FCSTD DOCUMENT  (FreeCAD 0.18R16146 (Git))
Label: Marlon
License: All rights reserved
LicenseURL: http://en.wikipedia.org/wiki/All_rights_reserved
objects: Part::Feature×142, Part::Cylinder×83, Part::FeaturePython×81, Sketcher::SketchObject×72, Part::Compound×70, App::Part×62, Part::Cut×46, PartDesign::Pocket×41, Part::Box×41, PartDesign::FeatureBase×30, PartDesign::Pad×28, Part::MultiFuse×23, App::DocumentObjectGroup×23, Part::Chamfer×6, Part::Fillet×5, PartDesign::PolarPattern×3, Part::Helix×3, Part::Sweep×3, PartDesign::LinearPattern×2, PartDesign::Chamfer×2, +4 more types
note: 751 computed .brp shape members not serialized (recipe doc carries the construction recipe); baked Part::Feature solids carry a one-line shape summary decoded from their .brp

FEATURE [Part::Compound] Compound038  label="3x4-male-pin-header"
  Placement = pos=(-9.21766,-28.5253,0) rot=(0,0,1;0rad)
FEATURE [Part::Compound] Compound040  label="1x8-female-pin-header"
  Placement = pos=(0.513,5.274,0) rot=(0,0,1;0rad)
FEATURE [Part::Compound] Compound021  label="2x18-male-pin-header"
  Placement = pos=(42.6284,-15.145,-2) rot=(0.707107,0.707107,0;3.14159rad)
FEATURE [Part::Compound] Compound045  label="1x8-female-pin-header005"
  Placement = pos=(20.89,-4.94,0) rot=(0,0,1;0rad)
FEATURE [Part::Cylinder] Cylinder003
  Angle = 360
  AttacherType = Attacher::AttachEngine3D
  Height = 10
  Placement = pos=(-27.818,28.246,-6) rot=(0,0,1;0rad)
  Radius = 0.45
FEATURE [Part::FeaturePython] Array003  label="1x8-male-pins-header-1"  # Draft array (typed FeaturePython)
  Angle = 360
  ArrayType = 0
  Axis = (0,0,1)
  Base = -> Cylinder003
  Center = (0,0,0)
  IntervalX = (2.55,0,0)
  IntervalY = (0,1,0)
  IntervalZ = (0,0,1)
  NumberPolar = 1
  NumberX = 8
  NumberY = 1
  NumberZ = 1
FEATURE [Part::Compound] Compound030  label="2x3-male-pin-header001"
  Placement = pos=(13.2632,-10.0364,0) rot=(0,0,1;1.5708rad)
FEATURE [Part::Compound] Compound042  label="1x8-female-pin-header002"
  Placement = pos=(20.89,-17.7,0) rot=(0,0,1;0rad)
FEATURE [Part::Cylinder] Cylinder012005  label="Cylinder017"
  Angle = 360
  AttacherType = Attacher::AttachEngine3D
  Height = 10
  Placement = pos=(-12.5549,-24.4231,-10) rot=(0,0,1;0rad)
  Radius = 0.75
FEATURE [Part::Compound] Compound037  label="2x5-male-pin-header"
  Placement = pos=(22.2091,-27.7375,0) rot=(0,0,1;0rad)
FEATURE [Part::Compound] Compound010  label="capsmd6_3x3-002"
  Placement = pos=(-17.5775,12.9976,0.64) rot=(0,0,1;1.5708rad)
FEATURE [Part::Compound] Compound004  label="Mosfet-P55NF06L002"
  Placement = pos=(-28.19,12.6,3.0595) rot=(0,0,1;3.14159rad)
FEATURE [Part::Cylinder] Cylinder012004  label="Cylinder016"
  Angle = 360
  AttacherType = Attacher::AttachEngine3D
  Height = 10
  Placement = pos=(-13.8056,-26.9244,-10) rot=(0,0,1;0rad)
  Radius = 0.45
FEATURE [Part::Feature] Array003008004001001  label="2x3-male-pins-003"
  Placement = pos=(-1.0239e-06,22.9718,0) rot=(0,0,1;0rad)
  shape: bbox 6 x 3.45 x 10 mm, 18 faces, 6 solids (baked)
FEATURE [Part::Compound] Compound019  label="1x8-male-pin-header003"
  Placement = pos=(-5.867,28.406,-2) rot=(1,0,0;3.14159rad)
FEATURE [Part::Compound] Compound001  label="pcb-terminal-block-female-1x6"
  Placement = pos=(-38.4593,9.365,0) rot=(0,0,1;3.14159rad)
FEATURE [Part::Compound] Compound031  label="2x3-male-pin-header002"
  Placement = pos=(33.6874,-10.0364,0) rot=(0,0,1;1.5708rad)
FEATURE [Sketcher::SketchObject] Sketch  label="ramps_pcb_main_sketch"
  MapMode = 5
  Placement = pos=(0,0,-2) rot=(0,0,1;0rad)
  sketch-geometry (4):
    g0: LineSegment StartX=-51.9275 StartY=30.8824 StartZ=0 EndX=51.9275 EndY=30.8824 EndZ=0
    g1: LineSegment StartX=51.9275 StartY=30.8824 StartZ=0 EndX=51.9275 EndY=-30.8824 EndZ=0
    g2: LineSegment StartX=51.9275 StartY=-30.8824 StartZ=0 EndX=-51.9275 EndY=-30.8824 EndZ=0
    g3: LineSegment StartX=-51.9275 StartY=-30.8824 StartZ=0 EndX=-51.9275 EndY=30.8824 EndZ=0
  constraints (11):
    c: Coincident(g0,g1)
    c: Coincident(g1,g2)
    c: Coincident(g2,g3)
    c: Coincident(g3,g0)
    c: Horizontal(g0)
    c: Horizontal(g2)
    c: Vertical(g1)
    c: Vertical(g3)
    c: Symmetric(g0,g1,g-1)
    c: DistanceX(g0) = 103.855
    c: DistanceY(g1) = -61.7649
FEATURE [Part::Compound] Compound013  label="capsmd6_3x3-005"
  Placement = pos=(-18.7775,0.15555,0.64) rot=(0,0,1;1.5708rad)
FEATURE [Part::Feature] Array003004  label="1x8-male-pins-header-005"
  Placement = pos=(50.0271,-48.4959,0) rot=(0,0,1;0rad)
  shape: bbox 18.75 x 0.9 x 10 mm, 24 faces, 8 solids (baked)
FEATURE [Part::Compound] Compound039  label="3x6-male-pin-header"
  Placement = pos=(22.8472,18.535,0) rot=(0,0,1;0rad)
FEATURE [Part::Compound] Compound043  label="1x8-female-pin-header003"
  Placement = pos=(-19.91,-4.94,0) rot=(0,0,1;0rad)
FEATURE [Part::Compound] Compound012  label="capsmd6_3x3-004"
  Placement = pos=(23.3715,-10.1425,0.64) rot=(0,0,1;1.5708rad)
FEATURE [Part::Compound] Compound035  label="2x4-male-pin-header001"
  Placement = pos=(26.0377,-2.3729,0) rot=(0,0,1;0rad)
FEATURE [Part::Compound] Compound008  label="capsmd4x3-003"
  Placement = pos=(25.4875,12.4224,0.64) rot=(0,0,1;0rad)
FEATURE [Part::Feature] Array003008004001001001  label="2x3-male-pins-004"
  Placement = pos=(20.4194,22.9718,0) rot=(0,0,1;0rad)
  shape: bbox 6 x 3.45 x 10 mm, 18 faces, 6 solids (baked)
FEATURE [Part::Feature] Array003008004001001001002001001  label="1x4-male-pins003"
  Placement = pos=(-3.19063,22.972,0) rot=(0,0,1;0rad)
  shape: bbox 8.55 x 0.9 x 10 mm, 12 faces, 4 solids (baked)
FEATURE [Part::Compound] Compound023  label="1x6-male-pin-header001"
  Placement = pos=(26.0377,5.27434,0) rot=(0,0,1;0rad)
FEATURE [Part::Compound] Compound020  label="1x8-male-pin-header004"
  Placement = pos=(17.1048,28.246,-2) rot=(1,0,0;3.14159rad)
FEATURE [Part::Cylinder] Cylinder002
  Angle = 360
  AttacherType = Attacher::AttachEngine3D
  Height = 10
  Placement = pos=(0.513,5.274,-6) rot=(0,0,1;0rad)
  Radius = 0.45
FEATURE [Part::Compound] Compound028  label="1x18-male-pin-header"
  Placement = pos=(47.7284,-15.145,0) rot=(0,0,1;1.5708rad)
FEATURE [Part::Feature] Array003008004001001001002001  label="1x4-male-pins002"
  Placement = pos=(17.8669,0.000102212,1) rot=(0,0,1;0rad)
  shape: bbox 8.55 x 0.9 x 10 mm, 12 faces, 4 solids (baked)
FEATURE [Part::Compound] Compound022  label="1x3-male-pin-header"
  Placement = pos=(-22.4583,-28.2517,0) rot=(0,0,1;1.5708rad)
FEATURE [Part::Compound] Compound015  label="1x6-male-pin-header"
  Placement = pos=(-18.6297,-20.2499,-2) rot=(1,0,0;3.14159rad)
FEATURE [Part::Feature] Array003008001001  label="2x4-male-pins-003"
  Placement = pos=(19.7813,25.3647,2) rot=(0,0,1;0rad)
  shape: bbox 8.55 x 3.45 x 10 mm, 24 faces, 8 solids (baked)
FEATURE [Part::Feature] Pad001  label="fuse-MF-R1100-final"
  Placement = pos=(-32.826,-15.9347,-3) rot=(0,0,1;1.30969rad)
  shape: bbox 7.645 x 23.57 x 35.78 mm, 54 faces (baked)
FEATURE [Part::Cylinder] Cylinder010
  Angle = 360
  AttacherType = Attacher::AttachEngine3D
  Height = 10
  Placement = pos=(-9.69619,-11.3164,-5) rot=(0,0,1;0rad)
  Radius = 0.45
FEATURE [Part::Feature] Pad002  label="fuse-MR-R500-final"
  Placement = pos=(-29.318,-16.5686,-3) rot=(0,0,1;1.30969rad)
  shape: bbox 5.941 x 17.2 x 29.18 mm, 56 faces (baked)
FEATURE [Part::Feature] Array003001  label="1x8-male-pins-header-2"
  Placement = pos=(21.951,0,0) rot=(0,0,1;0rad)
  shape: bbox 18.75 x 0.9 x 10 mm, 24 faces, 8 solids (baked)
FEATURE [Part::Compound] Compound018  label="1x8-male-pin-header002"
  Placement = pos=(-27.818,28.246,-2) rot=(1,0,0;3.14159rad)
FEATURE [Part::Compound] Compound009  label="capsmd6_3x3-1"
  Placement = pos=(-17.4705,-10.1425,0.64) rot=(0,0,1;1.5708rad)
FEATURE [Part::Compound] Compound017  label="1x8-male-pin-header001"
  Placement = pos=(22.2091,-20.2499,-2) rot=(1,0,0;3.14159rad)
FEATURE [Part::Compound] Compound014  label="capsmd6_3x3-006"
  Placement = pos=(3.5575,12.9976,0.64) rot=(0,0,1;1.5708rad)
FEATURE [Part::Compound] Compound026  label="1x4-male-pin-header002"
  Placement = pos=(-12.8868,23.1413,0) rot=(0,0,1;0rad)
FEATURE [Part::Cylinder] Cylinder007
  Angle = 360
  AttacherType = Attacher::AttachEngine3D
  Height = 10
  Placement = pos=(6.25643,-27.7476,-7) rot=(0,0,1;0rad)
  Radius = 0.45
FEATURE [Part::FeaturePython] Array003008  label="2x4-male-pins-1"  # Draft array (typed FeaturePython)
  Angle = 360
  ArrayType = 0
  Axis = (0,0,1)
  Base = -> Cylinder007
  Center = (0,0,0)
  IntervalX = (2.55,0,0)
  IntervalY = (0,2.55,0)
  IntervalZ = (0,0,1)
  NumberPolar = 1
  NumberX = 4
  NumberY = 2
  NumberZ = 1
FEATURE [Part::Cylinder] Cylinder
  Angle = 360
  AttacherType = Attacher::AttachEngine3D
  Height = 10
  Placement = pos=(-19.91,-17.7,-6) rot=(0,0,1;0rad)
  Radius = 0.45
FEATURE [Part::FeaturePython] Array  label="pololus-xyz-pads-cylinders"  # Draft array (typed FeaturePython)
  Angle = 360
  ArrayType = 0
  Axis = (0,0,1)
  Base = -> Cylinder
  Center = (0,0,0)
  IntervalX = (2.55,0,0)
  IntervalY = (0,12.76,0)
  IntervalZ = (0,0,1)
  NumberPolar = 1
  NumberX = 24
  NumberY = 2
  NumberZ = 1
FEATURE [Part::Compound] Compound003  label="Mosfet-P55NF06L001"
  Placement = pos=(-28.0607,19.4769,3.0595) rot=(0,0,1;3.14159rad)
FEATURE [Part::Feature] Array003008004001001001001  label="2x3-male-pins-005"
  Placement = pos=(40.8436,1.43086e-05,0) rot=(0,0,1;0rad)
  shape: bbox 6 x 3.45 x 10 mm, 18 faces, 6 solids (baked)
FEATURE [Part::Compound] Compound029  label="2x3-male-pin-header"
  Placement = pos=(-7.15619,-10.0464,0) rot=(0,0,1;1.5708rad)
FEATURE [Part::Compound] Compound036  label="2x4-male-pin-header002"
  Placement = pos=(40.2354,-27.7375,0) rot=(0,0,1;0rad)
FEATURE [Part::Compound] Compound006  label="capsmd4x3-1"
  Placement = pos=(35.6275,12.4224,0.64) rot=(0,0,1;0rad)
FEATURE [Part::Feature] Array003008004001001001002001001001  label="1x4-male-pins004"
  Placement = pos=(17.2288,22.972,0) rot=(0,0,1;0rad)
  shape: bbox 8.55 x 0.9 x 10 mm, 12 faces, 4 solids (baked)
FEATURE [Part::Compound] Compound044  label="1x8-female-pin-header004"
  Placement = pos=(0.49,-4.94,0) rot=(0,0,1;0rad)
FEATURE [Part::Feature] Array003003  label="1x8-male-pins-header-004"
  Placement = pos=(27.0553,-48.4959,0) rot=(0,0,1;0rad)
  shape: bbox 18.75 x 0.9 x 10 mm, 24 faces, 8 solids (baked)
FEATURE [Part::Compound] Compound041  label="1x8-female-pin-header001"
  Placement = pos=(0.49,-17.7,0) rot=(0,0,1;0rad)
FEATURE [Part::Compound] Compound032  label="2x3-male-pin-header003"
  Placement = pos=(-7.15619,12.9354,0) rot=(0,0,1;1.5708rad)
FEATURE [Part::Compound] Compound049  label="1x8-female-pin-header009"
  Placement = pos=(0.513,18.034,0) rot=(0,0,1;0rad)
FEATURE [Part::Compound] Compound046  label="1x8-female-pin-header006"
  Placement = pos=(-20.544,5.274,0) rot=(0,0,1;0rad)
FEATURE [Part::Cylinder] Cylinder004
  Angle = 360
  AttacherType = Attacher::AttachEngine3D
  Height = 10
  Placement = pos=(-18.6297,-20.2499,-4) rot=(0,0,1;0rad)
  Radius = 0.45
FEATURE [Part::FeaturePython] Array003005  label="1x6-male-pins-header-6"  # Draft array (typed FeaturePython)
  Angle = 360
  ArrayType = 0
  Axis = (0,0,1)
  Base = -> Cylinder004
  Center = (0,0,0)
  IntervalX = (2.55,0,0)
  IntervalY = (0,1,0)
  IntervalZ = (0,0,1)
  NumberPolar = 1
  NumberX = 6
  NumberY = 1
  NumberZ = 1
FEATURE [Part::Cylinder] Cylinder012
  Angle = 360
  AttacherType = Attacher::AttachEngine3D
  Height = 10
  Placement = pos=(26.0377,5.27434,-3) rot=(0,0,1;0rad)
  Radius = 0.45
FEATURE [Part::FeaturePython] Array003008004001001001002001001002  label="1x6-male-pins"  # Draft array (typed FeaturePython)
  Angle = 360
  ArrayType = 0
  Axis = (0,0,1)
  Base = -> Cylinder012
  Center = (0,0,0)
  IntervalX = (2.55,0,0)
  IntervalY = (0,1,0)
  IntervalZ = (0,0,1)
  NumberPolar = 1
  NumberX = 6
  NumberY = 1
  NumberZ = 1
FEATURE [PartDesign::Pad] Pad  label="ramps_pcb_main"
  Length = 2
  Length2 = 100
  Placement = pos=(0,0,-2) rot=(0,0,1;0rad)
  Profile = -> Sketch
  Type = 0
FEATURE [Sketcher::SketchObject] Sketch001  label="ramps-drills-sketch"
  MapMode = 5
  Support = -> [Pad]
  sketch-geometry (4):
    g0: Circle CenterX=-36.5 CenterY=28.25 CenterZ=0 NormalX=0 NormalY=0 NormalZ=1 AngleXU=0 Radius=1.61
    g1: Circle CenterX=-37.77 CenterY=-20.25 CenterZ=0 NormalX=0 NormalY=0 NormalZ=1 AngleXU=0 Radius=1.61
    g2: Circle CenterX=45.18 CenterY=-20.25 CenterZ=0 NormalX=0 NormalY=0 NormalZ=1 AngleXU=0 Radius=1.61
    g3: LineSegment [constr] StartX=-37.77 StartY=-20.25 StartZ=0 EndX=45.18 EndY=-20.25 EndZ=0
  constraints (11):
    c: Radius(g0) = 1.61
    c: DistanceX(g-1,g0) = -36.5
    c: DistanceY(g-1,g0) = 28.25
    c: Equal(g0,g2)
    c: Equal(g1,g2)
    c: DistanceX(g-1,g1) = -37.77
    c: DistanceY(g-1,g1) = -20.25
    c: Horizontal(g3)
    c: Coincident(g3,g1)
    c: Coincident(g3,g2)
    c: DistanceX(g-1,g2) = 45.18
FEATURE [PartDesign::Pocket] Pocket  label="ramps-drills"
  Length = 5
  Length2 = 100
  Placement = pos=(0,0,-2) rot=(0,0,1;0rad)
  Profile = -> Sketch001
  Type = 1
FEATURE [Sketcher::SketchObject] Sketch002  label="power-connector-pads-sketch"
  MapMode = 5
  Support = -> [Pocket]
  sketch-geometry (7):
    g0: Circle CenterX=-44.473 CenterY=-24.877 CenterZ=0 NormalX=0 NormalY=0 NormalZ=1 AngleXU=0 Radius=0.7
    g1: Circle CenterX=-44.473 CenterY=-9.562 CenterZ=0 NormalX=0 NormalY=0 NormalZ=1 AngleXU=0 Radius=0.7
    g2: Circle CenterX=-44.473 CenterY=-14.667 CenterZ=0 NormalX=0 NormalY=0 NormalZ=1 AngleXU=0 Radius=0.7
    g3: Circle CenterX=-44.473 CenterY=-19.772 CenterZ=0 NormalX=0 NormalY=0 NormalZ=1 AngleXU=0 Radius=0.7
    g4: LineSegment [constr] StartX=-44.473 StartY=-9.562 StartZ=0 EndX=-44.473 EndY=-14.667 EndZ=0
    g5: LineSegment [constr] StartX=-44.473 StartY=-14.667 StartZ=0 EndX=-44.473 EndY=-19.772 EndZ=0
    g6: LineSegment [constr] StartX=-44.473 StartY=-19.772 StartZ=0 EndX=-44.473 EndY=-24.877 EndZ=0
  constraints (18):
    c: Radius(g1) = 0.7
    c: Equal(g1,g3)
    c: Equal(g3,g2)
    c: Equal(g2,g0)
    c: DistanceX(g-1,g1) = -44.473
    c: DistanceY(g-1,g1) = -9.562
    c: Vertical(g4)
    c: Coincident(g4,g1)
    c: Coincident(g4,g2)
    c: DistanceY(g4) = -5.105
    c: Vertical(g5)
    c: Coincident(g5,g2)
    c: Coincident(g5,g3)
    c: Equal(g4,g5)
    c: Coincident(g3,g6)
    c: Vertical(g6)
    c: Coincident(g6,g0)
    c: Equal(g5,g6)
FEATURE [PartDesign::Pocket] Pocket001  label="power-connector-pads"
  Length = 5
  Length2 = 100
  Placement = pos=(0,0,-2) rot=(0,0,1;0rad)
  Profile = -> Sketch002
  Type = 1
FEATURE [Sketcher::SketchObject] Sketch003  label="terminal-pads-sketch"
  MapMode = 5
  Support = -> [Pocket001]
  sketch-geometry (11):
    g0: Circle CenterX=-38.41 CenterY=21.865 CenterZ=0 NormalX=0 NormalY=0 NormalZ=1 AngleXU=0 Radius=0.6
    g1: Circle CenterX=-38.41 CenterY=16.76 CenterZ=0 NormalX=0 NormalY=0 NormalZ=1 AngleXU=0 Radius=0.6
    g2: Circle CenterX=-38.41 CenterY=11.655 CenterZ=0 NormalX=0 NormalY=0 NormalZ=1 AngleXU=0 Radius=0.6
    g3: Circle CenterX=-38.41 CenterY=6.55 CenterZ=0 NormalX=0 NormalY=0 NormalZ=1 AngleXU=0 Radius=0.6
    g4: Circle CenterX=-38.41 CenterY=1.445 CenterZ=0 NormalX=0 NormalY=0 NormalZ=1 AngleXU=0 Radius=0.6
    g5: Circle CenterX=-38.41 CenterY=-3.66 CenterZ=0 NormalX=0 NormalY=0 NormalZ=1 AngleXU=0 Radius=0.6
    g6: LineSegment [constr] StartX=-38.41 StartY=-3.66 StartZ=0 EndX=-38.41 EndY=1.445 EndZ=0
    g7: LineSegment [constr] StartX=-38.41 StartY=6.55 StartZ=0 EndX=-38.41 EndY=1.445 EndZ=0
    g8: LineSegment [constr] StartX=-38.41 StartY=11.655 StartZ=0 EndX=-38.41 EndY=6.55 EndZ=0
    g9: LineSegment [constr] StartX=-38.41 StartY=16.76 StartZ=0 EndX=-38.41 EndY=11.655 EndZ=0
    g10: LineSegment [constr] StartX=-38.41 StartY=21.865 StartZ=0 EndX=-38.41 EndY=16.76 EndZ=0
  constraints (28):
    c: Radius(g5) = 0.6
    c: Equal(g5,g4)
    c: Equal(g4,g3)
    c: Equal(g3,g2)
    c: Equal(g2,g1)
    c: Equal(g1,g0)
    c: DistanceX(g-1,g5) = -38.41
    c: DistanceY(g-1,g5) = -3.66
    c: Vertical(g6)
    c: Coincident(g5,g6)
    c: Coincident(g4,g6)
    c: DistanceY(g6) = 5.105
    c: Vertical(g7)
    c: Coincident(g7,g4)
    c: Coincident(g3,g7)
    c: Vertical(g8)
    c: Equal(g6,g7)
    c: Coincident(g8,g3)
    c: Coincident(g2,g8)
    c: Equal(g7,g8)
    c: Vertical(g9)
    c: Coincident(g9,g2)
    c: Coincident(g1,g9)
    c: Vertical(g10)
    c: Coincident(g10,g1)
    c: Coincident(g0,g10)
    c: Equal(g10,g8)
    c: Equal(g9,g8)
FEATURE [PartDesign::Pocket] Pocket002  label="terminal-pads"
  Length = 5
  Length2 = 100
  Placement = pos=(0,0,-2) rot=(0,0,1;0rad)
  Profile = -> Sketch003
  Type = 1
FEATURE [Sketcher::SketchObject] Sketch004  label="fuse-pads-sketch"
  MapMode = 5
  Support = -> [Pocket002]
  sketch-geometry (6):
    g0: Circle CenterX=-32.826 CenterY=-21.048 CenterZ=0 NormalX=0 NormalY=0 NormalZ=1 AngleXU=0 Radius=0.6
    g1: Circle CenterX=-29.318 CenterY=-21.526 CenterZ=0 NormalX=0 NormalY=0 NormalZ=1 AngleXU=0 Radius=0.6
    g2: Circle CenterX=-29.318 CenterY=-11.316 CenterZ=0 NormalX=0 NormalY=0 NormalZ=1 AngleXU=0 Radius=0.6
    g3: Circle CenterX=-32.826 CenterY=-10.838 CenterZ=0 NormalX=0 NormalY=0 NormalZ=1 AngleXU=0 Radius=0.6
    g4: LineSegment [constr] StartX=-32.826 StartY=-21.048 StartZ=0 EndX=-32.826 EndY=-10.838 EndZ=0
    g5: LineSegment [constr] StartX=-29.318 StartY=-11.316 StartZ=0 EndX=-29.318 EndY=-21.526 EndZ=0
  constraints (16):
    c: Radius(g0) = 0.6
    c: Equal(g0,g1)
    c: Equal(g1,g2)
    c: Equal(g2,g3)
    c: DistanceX(g-1,g0) = -32.826
    c: DistanceY(g-1,g0) = -21.048
    c: Vertical(g4)
    c: Coincident(g4,g0)
    c: Coincident(g4,g3)
    c: Vertical(g5)
    c: Coincident(g5,g2)
    c: Coincident(g1,g5)
    c: DistanceY(g4) = 10.21
    c: DistanceX(g-1,g1) = -29.318
    c: DistanceY(g-1,g1) = -21.526
    c: DistanceY(g5) = -10.21
FEATURE [PartDesign::Pocket] Pocket003  label="fuse-pads"
  Length = 5
  Length2 = 100
  Placement = pos=(0,0,-2) rot=(0,0,1;0rad)
  Profile = -> Sketch004
  Type = 1
FEATURE [Part::Compound] Compound005  label="pushbutton-right-angle"
  Placement = pos=(-16.0943,-24.4244,0) rot=(0,0,1;0rad)
FEATURE [Part::Compound] Compound007  label="capsmd4x3-002"
  Placement = pos=(30.5575,12.4224,0.64) rot=(0,0,1;0rad)
FEATURE [Sketcher::SketchObject] Sketch005  label="mosfet-pads-sketch"
  MapMode = 5
  Support = -> [Pocket003]
  sketch-geometry (15):
    g0: Circle CenterX=-30.754 CenterY=1.765 CenterZ=0 NormalX=0 NormalY=0 NormalZ=1 AngleXU=0 Radius=0.5
    g1: Circle CenterX=-30.754 CenterY=4.305 CenterZ=0 NormalX=0 NormalY=0 NormalZ=1 AngleXU=0 Radius=0.5
    g2: Circle CenterX=-30.754 CenterY=6.845 CenterZ=0 NormalX=0 NormalY=0 NormalZ=1 AngleXU=0 Radius=0.5
    g3: Circle CenterX=-30.73 CenterY=14.85 CenterZ=0 NormalX=0 NormalY=0 NormalZ=1 AngleXU=0 Radius=0.5
    g4: Circle CenterX=-28.19 CenterY=14.85 CenterZ=0 NormalX=0 NormalY=0 NormalZ=1 AngleXU=0 Radius=0.5
    g5: Circle CenterX=-25.65 CenterY=14.85 CenterZ=0 NormalX=0 NormalY=0 NormalZ=1 AngleXU=0 Radius=0.5
    g6: Circle CenterX=-30.73 CenterY=21.87 CenterZ=0 NormalX=0 NormalY=0 NormalZ=1 AngleXU=0 Radius=0.5
    g7: Circle CenterX=-28.19 CenterY=21.87 CenterZ=0 NormalX=0 NormalY=0 NormalZ=1 AngleXU=0 Radius=0.5
    g8: Circle CenterX=-25.65 CenterY=21.87 CenterZ=0 NormalX=0 NormalY=0 NormalZ=1 AngleXU=0 Radius=0.5
    g9: LineSegment [constr] StartX=-30.754 StartY=4.305 StartZ=0 EndX=-30.754 EndY=1.765 EndZ=0
    g10: LineSegment [constr] StartX=-30.754 StartY=6.845 StartZ=0 EndX=-30.754 EndY=4.305 EndZ=0
    g11: LineSegment [constr] StartX=-30.73 StartY=14.85 StartZ=0 EndX=-28.19 EndY=14.85 EndZ=0
    g12: LineSegment [constr] StartX=-28.19 StartY=14.85 StartZ=0 EndX=-25.65 EndY=14.85 EndZ=0
    g13: LineSegment [constr] StartX=-30.73 StartY=21.87 StartZ=0 EndX=-28.19 EndY=21.87 EndZ=0
    g14: LineSegment [constr] StartX=-28.19 StartY=21.87 StartZ=0 EndX=-25.65 EndY=21.87 EndZ=0
  constraints (39):
    c: Radius(g0) = 0.5
    c: Equal(g0,g1)
    c: Equal(g1,g2)
    c: Equal(g2,g3)
    c: Equal(g3,g4)
    c: Equal(g4,g5)
    c: Equal(g5,g8)
    c: Equal(g8,g7)
    c: Equal(g7,g6)
    c: Coincident(g0,g9)
    c: Vertical(g9)
    c: Coincident(g1,g9)
    c: Vertical(g10)
    c: Coincident(g10,g1)
    c: Coincident(g2,g10)
    c: Equal(g9,g10)
    c: Horizontal(g11)
    c: Horizontal(g12)
    c: Coincident(g3,g11)
    c: Coincident(g4,g11)
    c: Coincident(g12,g4)
    c: Coincident(g5,g12)
    c: Equal(g11,g12)
    c: Horizontal(g13)
    c: Coincident(g13,g6)
    c: Coincident(g7,g13)
    c: Horizontal(g14)
    c: Coincident(g14,g7)
    c: Coincident(g14,g8)
    c: DistanceY(g9) = -2.54
    c: DistanceX(g11) = 2.54
    c: DistanceX(g-1,g0) = -30.754
    c: DistanceY(g-1,g0) = 1.765
    c: DistanceX(g13) = 2.54
    c: Equal(g13,g14)
    c: DistanceX(g-1,g5) = -25.65
    c: DistanceY(g-1,g5) = 14.85
    c: DistanceX(g-1,g8) = -25.65
    c: DistanceY(g-1,g8) = 21.87
FEATURE [PartDesign::Pocket] Pocket004  label="mosfet-pads"
  Length = 5
  Length2 = 100
  Placement = pos=(0,0,-2) rot=(0,0,1;0rad)
  Profile = -> Sketch005
  Type = 1
FEATURE [Part::FeaturePython] Array002  label="pololu-E1"  # Draft array (typed FeaturePython)
  Angle = 360
  ArrayType = 0
  Axis = (0,0,1)
  Base = -> Cylinder002
  Center = (0,0,0)
  IntervalX = (2.55,0,0)
  IntervalY = (0,12.76,0)
  IntervalZ = (0,0,1)
  NumberPolar = 1
  NumberX = 8
  NumberY = 2
  NumberZ = 1
FEATURE [Part::Compound] Compound027  label="1x4-male-pin-header003"
  Placement = pos=(7.53261,23.1413,0) rot=(0,0,1;0rad)
FEATURE [Part::Feature] Cut001  label="ramps-1.4-pcb"
  shape: bbox 103.9 x 61.76 x 2 mm, 335 faces (baked)
FEATURE [Part::Cylinder] Cylinder008
  Angle = 360
  AttacherType = Attacher::AttachEngine3D
  Height = 10
  Placement = pos=(22.2091,-25.1951,-10) rot=(0,0,1;0rad)
  Radius = 0.45
FEATURE [Part::FeaturePython] Array003008002  label="2x5-male-pins"  # Draft array (typed FeaturePython)
  Angle = 360
  ArrayType = 0
  Axis = (0,0,1)
  Base = -> Cylinder008
  Center = (0,0,0)
  IntervalX = (2.55,0,0)
  IntervalY = (0,2.55,0)
  IntervalZ = (0,0,1)
  NumberPolar = 1
  NumberX = 5
  NumberY = 2
  NumberZ = 1
  Placement = pos=(1.8577e-11,-2.55242,4) rot=(0,0,1;0rad)
FEATURE [Part::Cylinder] Cylinder009
  Angle = 360
  AttacherType = Attacher::AttachEngine3D
  Height = 10
  Placement = pos=(42.6284,-15.145,-5) rot=(0,0,1;0rad)
  Radius = 0.45
FEATURE [Part::FeaturePython] Array003008003  label="3x18-male-pins"  # Draft array (typed FeaturePython)
  Angle = 360
  ArrayType = 0
  Axis = (0,0,1)
  Base = -> Cylinder009
  Center = (0,0,0)
  IntervalX = (2.55,0,0)
  IntervalY = (0,2.55,0)
  IntervalZ = (0,0,1)
  NumberPolar = 1
  NumberX = 3
  NumberY = 18
  NumberZ = 1
FEATURE [Part::Compound] Compound002  label="Mosfet-P55NF06L"
  Placement = pos=(-33.004,4.305,3.0595) rot=(0,0,1;1.5708rad)
FEATURE [Part::Compound] Compound  label="terminal-block-male-straight-4-ways"
  Links = -> [Compound002]
  Placement = pos=(-43.998,-17.207,0) rot=(0,0,-1;1.5708rad)
FEATURE [Part::Compound] Compound048  label="1x8-female-pin-header008"
  Placement = pos=(-20.544,18.034,0) rot=(0,0,1;0rad)
FEATURE [Part::Compound] Compound034  label="2x4-male-pin-header"
  Placement = pos=(6.25643,-27.7376,0) rot=(0,0,1;0rad)
FEATURE [Part::Cylinder] Cylinder012003  label="Cylinder015"
  Angle = 360
  AttacherType = Attacher::AttachEngine3D
  Height = 10
  Placement = pos=(-18.3489,-26.9244,-10) rot=(0,0,1;0rad)
  Radius = 0.45
FEATURE [Part::Compound] Compound047  label="1x8-female-pin-header007"
  Placement = pos=(-19.91,-17.7,0) rot=(0,0,1;0rad)
FEATURE [Part::Feature] Array003008004001  label="2x3-male-pins-002"
  Placement = pos=(20.4194,1.43086e-05,0) rot=(0,0,1;0rad)
  shape: bbox 6 x 3.45 x 10 mm, 18 faces, 6 solids (baked)
FEATURE [Part::Compound] Compound025  label="1x4-male-pin-header001"
  Placement = pos=(8.17071,0.169402,0) rot=(0,0,1;0rad)
FEATURE [Part::Cylinder] Cylinder011
  Angle = 360
  AttacherType = Attacher::AttachEngine3D
  Height = 10
  Placement = pos=(-9.69619,0.1693,-4) rot=(0,0,1;0rad)
  Radius = 0.45
FEATURE [Part::FeaturePython] Array003008004001001001002  label="1x4-male-pins001"  # Draft array (typed FeaturePython)
  Angle = 360
  ArrayType = 0
  Axis = (0,0,1)
  Base = -> Cylinder011
  Center = (0,0,0)
  IntervalX = (2.55,0,0)
  IntervalY = (0,1,0)
  IntervalZ = (0,0,1)
  NumberPolar = 1
  NumberX = 4
  NumberY = 1
  NumberZ = 1
FEATURE [Part::Feature] Cylinder012001  label="Cylinder013"
  Placement = pos=(22.8472,18.515,-4) rot=(0,0,1;0rad)
  shape: bbox 0.9 x 0.9 x 10 mm, 3 faces (baked)
FEATURE [Part::Cylinder] Cylinder001
  Angle = 360
  AttacherType = Attacher::AttachEngine3D
  Height = 10
  Placement = pos=(-20.544,5.274,-6) rot=(0,0,1;0rad)
  Radius = 0.45
FEATURE [Part::FeaturePython] Array001  label="pololu-E0"  # Draft array (typed FeaturePython)
  Angle = 360
  ArrayType = 0
  Axis = (0,0,1)
  Base = -> Cylinder001
  Center = (0,0,0)
  IntervalX = (2.55,0,0)
  IntervalY = (0,12.76,0)
  IntervalZ = (0,0,1)
  NumberPolar = 1
  NumberX = 8
  NumberY = 2
  NumberZ = 1
FEATURE [Part::Cylinder] Cylinder012002  label="Cylinder014"
  Angle = 360
  AttacherType = Attacher::AttachEngine3D
  Height = 10
  Placement = pos=(-19.5996,-24.4231,-10) rot=(0,0,1;0rad)
  Radius = 0.75
FEATURE [Part::MultiFuse] Fusion  label="push-button-pads"
  Placement = pos=(0,0,4) rot=(0,0,1;0rad)
  Shapes = -> [Cylinder012002,Cylinder012003,Cylinder012005,Cylinder012004]
FEATURE [Part::Feature] Array003008001  label="2x4-male-pins-002"
  Placement = pos=(33.979,6.1607e-05,0) rot=(0,0,1;0rad)
  shape: bbox 8.55 x 3.45 x 10 mm, 24 faces, 8 solids (baked)
FEATURE [Part::Compound] Compound011  label="capsmd6_3x3-003"
  Placement = pos=(2.9505,-10.1425,0.64) rot=(0,0,1;1.5708rad)
FEATURE [Part::Compound] Compound024  label="1x4-male-pin-header"
  Placement = pos=(-9.69619,0.1693,0) rot=(0,0,1;0rad)
FEATURE [Part::FeaturePython] Array003008004001001001002001001003  label="3x6-male-pins"  # Draft array (typed FeaturePython)
  Angle = 360
  ArrayType = 0
  Axis = (0,0,1)
  Base = -> Cylinder012001
  Center = (0,0,0)
  IntervalX = (2.55,0,0)
  IntervalY = (0,2.55,0)
  IntervalZ = (0,0,1)
  NumberPolar = 1
  NumberX = 6
  NumberY = 3
  NumberZ = 1
FEATURE [Part::Cylinder] Cylinder006
  Angle = 360
  AttacherType = Attacher::AttachEngine3D
  Height = 10
  Placement = pos=(-9.21766,-28.5453,-6) rot=(0,0,1;0rad)
  Radius = 0.45
FEATURE [Part::FeaturePython] Array003007  label="3x4-male-pins"  # Draft array (typed FeaturePython)
  Angle = 360
  ArrayType = 0
  Axis = (0,0,1)
  Base = -> Cylinder006
  Center = (0,0,0)
  IntervalX = (2.55,0,0)
  IntervalY = (0,2.55,0)
  IntervalZ = (0,0,1)
  NumberPolar = 1
  NumberX = 4
  NumberY = 3
  NumberZ = 1
FEATURE [Part::Compound] Compound016  label="1x8-male-pin-header"
  Placement = pos=(-0.7627,-20.2499,-2) rot=(1,0,0;3.14159rad)
FEATURE [Part::FeaturePython] Array003008004  label="2x3-male-pins-1"  # Draft array (typed FeaturePython)
  Angle = 360
  ArrayType = 0
  Axis = (0,0,1)
  Base = -> Cylinder010
  Center = (0,0,0)
  IntervalX = (2.55,0,0)
  IntervalY = (0,2.55,0)
  IntervalZ = (0,0,1)
  NumberPolar = 1
  NumberX = 3
  NumberY = 2
  NumberZ = 1
FEATURE [Part::Compound] Compound033  label="2x3-male-pin-header004"
  Placement = pos=(13.2632,12.9354,0) rot=(0,0,1;1.5708rad)
FEATURE [Part::Compound] Compound050  label="ramps-1.4"
  Links = -> [Cut001,Compound,Compound001,Compound003,Compound004,Pad001,Pad002,Compound005,Compound006,Compound007,Compound008,Compound009,Compound010,Compound011,Compound012,Compound013,Compound014,Compound015,Compound016,Compound017,Compound018,Compound019,Compound020,Compound021,Compound022,Compound023,Compound024,Compound025,Compound026,Compound027,Compound028,Compound029,Compound030,Compound031,+18 more]
FEATURE [Part::Cylinder] Cylinder005
  Angle = 360
  AttacherType = Attacher::AttachEngine3D
  Height = 10
  Placement = pos=(-22.4583,-28.2517,-6) rot=(0,0,1;0rad)
  Radius = 0.45
FEATURE [Part::FeaturePython] Array003006  label="1x3-male-pins"  # Draft array (typed FeaturePython)
  Angle = 360
  ArrayType = 0
  Axis = (0,0,1)
  Base = -> Cylinder005
  Center = (0,0,0)
  IntervalX = (1,0,0)
  IntervalY = (0,2.55,0)
  IntervalZ = (0,0,1)
  NumberPolar = 1
  NumberX = 1
  NumberY = 3
  NumberZ = 1
FEATURE [Part::Feature] Array003002  label="1x8-male-pins-header-3"
  Placement = pos=(44.9228,0,0) rot=(0,0,1;0rad)
  shape: bbox 18.75 x 0.9 x 10 mm, 24 faces, 8 solids (baked)
FEATURE [Part::MultiFuse] Fusion001  label="pads"
  Shapes = -> [Array,Fusion,Array001,Array002,Array003,Array003001,Array003002,Array003003,Array003004,Array003005,Array003006,Array003007,Array003008,Array003008001,Array003008002,Array003008003,Array003008004,Array003008004001,Array003008004001001,Array003008004001001001,Array003008004001001001001,Array003008001001,Array003008004001001001002,Array003008004001001001002001,Array003008004001001001002001001,+3 more]
FEATURE [Part::Cut] Cut  label="pcb-with-pads"
  Base = -> Pocket004
  Tool = -> Fusion001
FEATURE [App::DocumentObjectGroup] Group001  label="ramps-pcb-src"
  Group = -> [Pad,Pocket,Pocket001,Pocket002,Pocket003,Pocket004,Array,Array001,Array002,Array003,Array003001,Array003002,Array003003,Array003004,Array003005,Array003006,Array003007,Array003008,Array003008001,Array003008002,Array003008003,Array003008004,Array003008004001,Array003008004001001,Array003008004001001001,Array003008004001001001001,Array003008001001,Array003008004001001001002,+8 more]
FEATURE [App::Part] Part001  label="RAMPS-1.4"
  Group = -> [Fusion,Fusion001,Cylinder006,Cut,Pocket002,Array001,Pad,Pocket003,Cylinder005,Array002,Cylinder012001,Array003008004001,Array003007,Array003008004,Array003008004001001001002001001002,Array,Array003008004001001001002001001003,Array003008004001001001001,Pocket004,Cylinder012004,Cylinder002,Array003001,Array003008001,Sketch002,Cylinder003,Cylinder010,Array003003,Cylinder012005,Sketch005,Sketch003,+85 more]
  License = CC BY 3.0
  LicenseURL = http://creativecommons.org/licenses/by/3.0/
  Origin = -> Origin001
  Placement = pos=(0.5,-4,15) rot=(0,0,1;0rad)
FEATURE [Part::Compound] Compound051  label="1x8-female-pin-header-003"
  Placement = pos=(-27.06,24.084,2) rot=(0,0,1;0rad)
FEATURE [Part::Compound] Compound052  label="1x8-female-pin-header-002"
  Placement = pos=(22.724,-24.176,2) rot=(0,0,1;0rad)
FEATURE [Part::Compound] Compound054  label="2x18-female-pin-header"
  Placement = pos=(45.584,-19.096,2) rot=(0,0,1;1.5708rad)
FEATURE [Part::Feature] Fusion003  label="2x1-male-pin-header-2"
  Placement = pos=(13.9501,1.24,2) rot=(0,0,1;0rad)
  shape: bbox 4.88 x 2.54 x 11.2 mm, 66 faces (baked)
FEATURE [Sketcher::SketchObject] Sketch014  label="mega-chip-sketch"
  MapMode = 5
  sketch-geometry (8):
    g0: LineSegment StartX=-6.5 StartY=7 StartZ=0 EndX=6.5 EndY=7 EndZ=0
    g1: LineSegment StartX=7 StartY=6.5 StartZ=0 EndX=7 EndY=-6.5 EndZ=0
    g2: LineSegment StartX=6.5 StartY=-7 StartZ=0 EndX=-6.5 EndY=-7 EndZ=0
    g3: LineSegment StartX=-7 StartY=-6.5 StartZ=0 EndX=-7 EndY=6.5 EndZ=0
    g4: ArcOfCircle CenterX=-6.5 CenterY=6.5 CenterZ=0 NormalX=0 NormalY=0 NormalZ=1 AngleXU=0 Radius=0.5 StartAngle=1.5708 EndAngle=3.14159
    g5: ArcOfCircle CenterX=6.5 CenterY=6.5 CenterZ=0 NormalX=0 NormalY=0 NormalZ=1 AngleXU=0 Radius=0.5 StartAngle=0 EndAngle=1.5708
    g6: ArcOfCircle CenterX=6.5 CenterY=-6.5 CenterZ=0 NormalX=0 NormalY=0 NormalZ=1 AngleXU=0 Radius=0.5 StartAngle=4.71239 EndAngle=6.28319
    g7: ArcOfCircle CenterX=-6.5 CenterY=-6.5 CenterZ=0 NormalX=0 NormalY=0 NormalZ=1 AngleXU=0 Radius=0.5 StartAngle=3.14159 EndAngle=4.71239
  constraints (19):
    c: Horizontal(g0)
    c: Horizontal(g2)
    c: Vertical(g1)
    c: Vertical(g3)
    c: Tangent(g0,g4)
    c: Tangent(g3,g4)
    c: Tangent(g0,g5)
    c: Tangent(g1,g5)
    c: Tangent(g1,g6)
    c: Tangent(g2,g6)
    c: Tangent(g2,g7)
    c: Tangent(g3,g7)
    c: Radius(g4) = 0.5
    c: Equal(g4,g5)
    c: Equal(g5,g6)
    c: Equal(g6,g7)
    c: Symmetric(g4,g6,g-1)
    c: Equal(g0,g3)
    c: DistanceX(g3,g1) = 14
FEATURE [Part::Feature] LinearPattern001  label="Arduino-mega-pcb"
  shape: bbox 101.5 x 53.17 x 2 mm, 114 faces (baked)
FEATURE [Part::Compound] Compound055  label="1x8-female-pin-header-1"
  Placement = pos=(0.136,-24.176,2) rot=(0,0,1;0rad)
FEATURE [Part::Feature] Fusion002  label="2x1-male-pin-header-1"
  Placement = pos=(13.9501,3.78,2) rot=(0,0,1;0rad)
  shape: bbox 4.88 x 2.54 x 11.2 mm, 66 faces (baked)
FEATURE [Part::Feature] Fusion004  label="jack_DC_2.1mm_PCB-final"
  Placement = pos=(-52.85,-18.51,2) rot=(0.57735,-0.57735,-0.57735;2.0944rad)
  shape: bbox 14.48 x 9.472 x 14.78 mm, 34 faces (baked)
FEATURE [Part::Compound] Compound056  label="USB-2.0-type-B-jack-PCB"
  Placement = pos=(-49.82,11.39,7.25) rot=(0.57735,-0.57735,-0.57735;2.0944rad)
FEATURE [PartDesign::Pad] Pad003  label="mega-chip"
  Length = 0.7
  Length2 = 100
  Profile = -> Sketch014
  Type = 0
FEATURE [Part::Compound] Compound057  label="1x6-female-pin-header"
  Placement = pos=(-17.916,-24.176,2) rot=(0,0,1;0rad)
FEATURE [Part::Feature] Fusion005  label="2x1-male-pin-header-003"
  Placement = pos=(13.9501,-1.3,2) rot=(0,0,1;0rad)
  shape: bbox 4.88 x 2.54 x 11.2 mm, 66 faces (baked)
FEATURE [Part::Compound] Compound053  label="2x3-male-pin-header005"
  Links = -> [Fusion002,Fusion003,Fusion005]
FEATURE [Sketcher::SketchObject] Sketch018  label="mega-pcb-base-sketch"
  MapMode = 5
  sketch-geometry (11):
    g0: LineSegment StartX=-50.7275 StartY=-26.5825 StartZ=0 EndX=-50.7275 EndY=26.5825 EndZ=0
    g1: LineSegment StartX=-50.7275 StartY=26.5825 StartZ=0 EndX=45.6905 EndY=26.5825 EndZ=0
    g2: LineSegment StartX=45.6905 StartY=26.5825 StartZ=0 EndX=48.1905 EndY=24.0825 EndZ=0
    g3: LineSegment StartX=48.1905 StartY=24.0825 StartZ=0 EndX=48.1905 EndY=13.8825 EndZ=0
    g4: LineSegment StartX=48.1905 StartY=13.8825 StartZ=0 EndX=50.7275 EndY=11.3455 EndZ=0
    g5: LineSegment StartX=50.7275 StartY=11.3455 StartZ=0 EndX=50.7275 EndY=-22.8245 EndZ=0
    g6: LineSegment StartX=50.7275 StartY=-22.8245 StartZ=0 EndX=48.1905 EndY=-25.3225 EndZ=0
    g7: LineSegment StartX=48.1905 StartY=-25.3225 StartZ=0 EndX=48.1905 EndY=-26.5825 EndZ=0
    g8: LineSegment StartX=48.1905 StartY=-26.5825 StartZ=0 EndX=-50.7275 EndY=-26.5825 EndZ=0
    g9: LineSegment [constr] StartX=-50.7275 StartY=0 StartZ=0 EndX=50.7275 EndY=0 EndZ=0
    g10: LineSegment [constr] StartX=45.6905 StartY=26.5825 StartZ=0 EndX=49.6905 EndY=26.5825 EndZ=0
  constraints (34):
    c: Vertical(g0)
    c: Coincident(g0,g1)
    c: Horizontal(g1)
    c: Coincident(g1,g2)
    c: Coincident(g2,g3)
    c: Coincident(g3,g4)
    c: Coincident(g4,g5)
    c: Vertical(g5)
    c: Coincident(g5,g6)
    c: Coincident(g6,g7)
    c: Coincident(g7,g8)
    c: Coincident(g8,g0)
    c: Horizontal(g8)
    c: Vertical(g3)
    c: Vertical(g7)
    c: Symmetric(g0,g0,g-1)
    c: Horizontal(g9)
    c: PointOnObject(g9,g-1)
    c: PointOnObject(g9,g0)
    c: PointOnObject(g9,g5)
    c: Symmetric(g9,g9,g-2)
    c: DistanceX(g0,g2) = 98.918
    c: DistanceY(g0) = 53.165
    c: DistanceX(g9) = 101.455
    c: PointOnObject(g6,g3)
    c: DistanceY(g5) = -34.17
    c: DistanceY(g7) = -1.26
    c: DistanceY(g3) = -10.2
    c: Horizontal(g10)
    c: Coincident(g10,g1)
    c: DistanceX(g10) = 4
    c: Angle(g2,g10) = 0.785398
    c: DistanceX(g1,g2) = 2.5
    c: Parallel(g4,g2)
FEATURE [Part::Compound] Compound058  label="1x8-female-pin-header-004"
  Placement = pos=(-5.216,24.084,2) rot=(0,0,1;0rad)
FEATURE [App::DocumentObjectGroup] Group002  label="mega-chip-src"
  Group = -> [Pad003]
FEATURE [Part::Feature] Pad001001  label="mega-chip001"
  Placement = pos=(-0.1505,1.7065,2) rot=(0,0,1;0rad)
  shape: bbox 14 x 14 x 0.7 mm, 10 faces (baked)
FEATURE [PartDesign::Pad] Pad001002  label="mega-pcb-base"
  Length = 2
  Length2 = 100
  Profile = -> Sketch018
  Type = 0
FEATURE [Sketcher::SketchObject] Sketch019  label="drills-sketch"
  MapMode = 5
  Placement = pos=(0,0,2) rot=(0,0,1;0rad)
  Support = -> [Pad001002]
  sketch-geometry (7):
    g0: Circle CenterX=-35.6964 CenterY=24.084 CenterZ=0 NormalX=0 NormalY=0 NormalZ=1 AngleXU=0 Radius=1.6
    g1: LineSegment [constr] StartX=-35.6964 StartY=24.084 StartZ=0 EndX=39.234 EndY=24.084 EndZ=0
    g2: Circle CenterX=39.234 CenterY=24.084 CenterZ=0 NormalX=0 NormalY=0 NormalZ=1 AngleXU=0 Radius=1.6
    g3: Circle CenterX=-36.966 CenterY=-24.176 CenterZ=0 NormalX=0 NormalY=0 NormalZ=1 AngleXU=0 Radius=1.6
    g4: Circle CenterX=15.1 CenterY=-19.1 CenterZ=0 NormalX=0 NormalY=0 NormalZ=1 AngleXU=0 Radius=1.6
    g5: Circle CenterX=15.1 CenterY=8.844 CenterZ=0 NormalX=0 NormalY=0 NormalZ=1 AngleXU=0 Radius=1.6
    g6: Circle CenterX=45.58 CenterY=-24.18 CenterZ=0 NormalX=0 NormalY=0 NormalZ=1 AngleXU=0 Radius=1.6
  constraints (20):
    c: Radius(g0) = 1.6
    c: DistanceX(g-1,g0) = -35.6964
    c: DistanceY(g-1,g0) = 24.084
    c: Horizontal(g1)
    c: Coincident(g1,g0)
    c: Coincident(g2,g1)
    c: Equal(g2,g0)
    c: DistanceX(g-1,g1) = 39.234
    c: Equal(g0,g5)
    c: Equal(g5,g4)
    c: Equal(g4,g6)
    c: Equal(g6,g3)
    c: DistanceX(g-1,g3) = -36.966
    c: DistanceY(g-1,g3) = -24.176
    c: DistanceY(g-1,g5) = 8.844
    c: DistanceX(g-1,g5) = 15.1
    c: DistanceX(g-1,g4) = 15.1
    c: DistanceY(g-1,g4) = -19.1
    c: DistanceX(g-1,g6) = 45.58
    c: DistanceY(g-1,g6) = -24.18
FEATURE [PartDesign::Pocket] Pocket006  label="drills"
  Length = 5
  Length2 = 100
  Profile = -> Sketch019
  Type = 1
FEATURE [Sketcher::SketchObject] Sketch015  label="power-pads-sketch"
  MapMode = 5
  Placement = pos=(0,0,2) rot=(0,0,1;0rad)
  Support = -> [Pocket006]
  sketch-geometry (4):
    g0: Circle CenterX=-45.25 CenterY=-18.41 CenterZ=0 NormalX=0 NormalY=0 NormalZ=1 AngleXU=0 Radius=1.65
    g1: Circle CenterX=-39.25 CenterY=-18.41 CenterZ=0 NormalX=0 NormalY=0 NormalZ=1 AngleXU=0 Radius=1.65
    g2: Circle CenterX=-42.2434 CenterY=-23.3867 CenterZ=0 NormalX=0 NormalY=0 NormalZ=1 AngleXU=0 Radius=1.65
    g3: LineSegment [constr] StartX=-45.25 StartY=-18.41 StartZ=0 EndX=-39.25 EndY=-18.41 EndZ=0
  constraints (9):
    c: Horizontal(g3)
    c: DistanceX(g-1,g3) = -39.25
    c: DistanceY(g-1,g3) = -18.41
    c: DistanceX(g3) = 6
    c: Coincident(g0,g3)
    c: Coincident(g1,g3)
    c: Equal(g0,g1)
    c: Equal(g1,g2)
    c: Radius(g0) = 1.65
FEATURE [PartDesign::Pocket] Pocket014  label="power-pads"
  Length = 5
  Length2 = 100
  Profile = -> Sketch015
  Type = 1
FEATURE [Sketcher::SketchObject] Sketch016  label="usb-pads-sketch"
  MapMode = 5
  Placement = pos=(0,0,2) rot=(0,0,1;0rad)
  Support = -> [Pocket014]
  sketch-geometry (11):
    g0: Circle CenterX=-47.13 CenterY=17.38 CenterZ=0 NormalX=0 NormalY=0 NormalZ=1 AngleXU=0 Radius=1.1
    g1: Circle CenterX=-47.13 CenterY=5.38 CenterZ=0 NormalX=0 NormalY=0 NormalZ=1 AngleXU=0 Radius=1.1
    g2: Circle CenterX=-44.42 CenterY=12.64 CenterZ=0 NormalX=0 NormalY=0 NormalZ=1 AngleXU=0 Radius=0.475
    g3: Circle CenterX=-42.42 CenterY=12.64 CenterZ=0 NormalX=0 NormalY=0 NormalZ=1 AngleXU=0 Radius=0.475
    g4: Circle CenterX=-44.42 CenterY=10.14 CenterZ=0 NormalX=0 NormalY=0 NormalZ=1 AngleXU=0 Radius=0.475
    g5: Circle CenterX=-42.42 CenterY=10.14 CenterZ=0 NormalX=0 NormalY=0 NormalZ=1 AngleXU=0 Radius=0.475
    g6: LineSegment [constr] StartX=-47.13 StartY=17.38 StartZ=0 EndX=-47.13 EndY=5.38 EndZ=0
    g7: LineSegment [constr] StartX=-44.42 StartY=10.14 StartZ=0 EndX=-42.42 EndY=10.14 EndZ=0
    g8: LineSegment [constr] StartX=-42.42 StartY=12.64 StartZ=0 EndX=-42.42 EndY=10.14 EndZ=0
    g9: LineSegment [constr] StartX=-44.42 StartY=12.64 StartZ=0 EndX=-42.42 EndY=12.64 EndZ=0
    g10: LineSegment [constr] StartX=-44.42 StartY=12.64 StartZ=0 EndX=-44.42 EndY=10.14 EndZ=0
  constraints (28):
    c: DistanceY(g-1,g1) = 5.38
    c: DistanceX(g-1,g1) = -47.13
    c: Radius(g1) = 1.1
    c: Equal(g1,g0)
    c: Vertical(g6)
    c: Coincident(g6,g0)
    c: Coincident(g6,g1)
    c: DistanceY(g6) = -12
    c: Equal(g2,g3)
    c: Equal(g3,g4)
    c: Equal(g4,g5)
    c: DistanceX(g-1,g5) = -42.42
    c: Horizontal(g7)
    c: Coincident(g7,g5)
    c: Coincident(g7,g4)
    c: DistanceY(g-1,g5) = 10.14
    c: Radius(g2) = 0.475
    c: DistanceX(g7) = 2
    c: Vertical(g8)
    c: Coincident(g8,g5)
    c: Coincident(g8,g3)
    c: DistanceY(g8) = -2.5
    c: Horizontal(g9)
    c: Coincident(g9,g2)
    c: Coincident(g9,g3)
    c: Vertical(g10)
    c: Coincident(g10,g2)
    c: Coincident(g10,g4)
FEATURE [PartDesign::Pocket] Pocket011  label="usb-pads"
  Length = 5
  Length2 = 100
  Profile = -> Sketch016
  Type = 1
FEATURE [Sketcher::SketchObject] Sketch017  label="male-pins-connectors-sketch"
  MapMode = 5
  Placement = pos=(0,0,2) rot=(0,0,1;0rad)
  Support = -> [Pocket011]
  sketch-geometry (13):
    g0: Circle CenterX=12.6801 CenterY=-1.3 CenterZ=0 NormalX=0 NormalY=0 NormalZ=1 AngleXU=0 Radius=0.5
    g1: Circle CenterX=15.2201 CenterY=-1.3 CenterZ=0 NormalX=0 NormalY=0 NormalZ=1 AngleXU=0 Radius=0.5
    g2: Circle CenterX=15.2201 CenterY=1.24 CenterZ=0 NormalX=0 NormalY=0 NormalZ=1 AngleXU=0 Radius=0.5
    g3: Circle CenterX=12.6801 CenterY=1.24 CenterZ=0 NormalX=0 NormalY=0 NormalZ=1 AngleXU=0 Radius=0.5
    g4: LineSegment [constr] StartX=12.6801 StartY=1.24 StartZ=0 EndX=15.2201 EndY=1.24 EndZ=0
    g5: LineSegment [constr] StartX=15.2201 StartY=1.24 StartZ=0 EndX=15.2201 EndY=-1.3 EndZ=0
    g6: LineSegment [constr] StartX=15.2201 StartY=-1.3 StartZ=0 EndX=12.6801 EndY=-1.3 EndZ=0
    g7: LineSegment [constr] StartX=12.6801 StartY=-1.3 StartZ=0 EndX=12.6801 EndY=1.24 EndZ=0
    g8: Circle CenterX=12.6801 CenterY=3.78 CenterZ=0 NormalX=0 NormalY=0 NormalZ=1 AngleXU=0 Radius=0.5
    g9: Circle CenterX=15.2201 CenterY=3.78 CenterZ=0 NormalX=0 NormalY=0 NormalZ=1 AngleXU=0 Radius=0.5
    g10: LineSegment [constr] StartX=12.6801 StartY=1.24 StartZ=0 EndX=12.6801 EndY=3.78 EndZ=0
    g11: LineSegment [constr] StartX=12.6801 StartY=3.78 StartZ=0 EndX=15.2201 EndY=3.78 EndZ=0
    g12: LineSegment [constr] StartX=15.2201 StartY=3.78 StartZ=0 EndX=15.2201 EndY=1.24 EndZ=0
  constraints (33):
    c: Radius(g0) = 0.5
    c: DistanceX(g-1,g0) = 12.6801
    c: DistanceY(g-1,g0) = -1.3
    c: Coincident(g4,g5)
    c: Coincident(g5,g6)
    c: Coincident(g6,g7)
    c: Coincident(g7,g4)
    c: Horizontal(g4)
    c: Horizontal(g6)
    c: Vertical(g5)
    c: Coincident(g4,g3)
    c: Coincident(g4,g2)
    c: Coincident(g6,g0)
    c: Coincident(g5,g1)
    c: Equal(g3,g2)
    c: Equal(g2,g1)
    c: Equal(g1,g0)
    c: DistanceY(g5) = -2.54
    c: Equal(g5,g6)
    c: Equal(g6,g4)
    c: Equal(g4,g7)
    c: Equal(g8,g9)
    c: Equal(g9,g2)
    c: Coincident(g10,g11)
    c: Horizontal(g11)
    c: Coincident(g11,g12)
    c: Vertical(g10)
    c: Vertical(g12)
    c: Coincident(g8,g10)
    c: Coincident(g11,g9)
    c: Coincident(g2,g12)
    c: Coincident(g10,g3)
    c: Equal(g12,g4)
FEATURE [PartDesign::Pocket] Pocket012  label="male-pins-pads"
  Length = 5
  Length2 = 100
  Profile = -> Sketch017
  Type = 1
FEATURE [Sketcher::SketchObject] Sketch007  label="female-headerx8-1-sketch"
  MapMode = 5
  Placement = pos=(0,0,2) rot=(0,0,1;0rad)
  Support = -> [Pocket012]
  sketch-geometry (15):
    g0: Circle CenterX=-27.06 CenterY=24.084 CenterZ=0 NormalX=0 NormalY=0 NormalZ=1 AngleXU=0 Radius=0.5
    g1: LineSegment [constr] StartX=-27.06 StartY=24.084 StartZ=0 EndX=-24.52 EndY=24.084 EndZ=0
    g2: Circle CenterX=-24.52 CenterY=24.084 CenterZ=0 NormalX=0 NormalY=0 NormalZ=1 AngleXU=0 Radius=0.5
    g3: Circle CenterX=-21.98 CenterY=24.084 CenterZ=0 NormalX=0 NormalY=0 NormalZ=1 AngleXU=0 Radius=0.5
    g4: Circle CenterX=-19.44 CenterY=24.084 CenterZ=0 NormalX=0 NormalY=0 NormalZ=1 AngleXU=0 Radius=0.5
    g5: Circle CenterX=-16.9 CenterY=24.084 CenterZ=0 NormalX=0 NormalY=0 NormalZ=1 AngleXU=0 Radius=0.5
    g6: LineSegment [constr] StartX=-24.52 StartY=24.084 StartZ=0 EndX=-21.98 EndY=24.084 EndZ=0
    g7: LineSegment [constr] StartX=-21.98 StartY=24.084 StartZ=0 EndX=-19.44 EndY=24.084 EndZ=0
    g8: LineSegment [constr] StartX=-19.44 StartY=24.084 StartZ=0 EndX=-16.9 EndY=24.084 EndZ=0
    g9: Circle CenterX=-14.36 CenterY=24.084 CenterZ=0 NormalX=0 NormalY=0 NormalZ=1 AngleXU=0 Radius=0.5
    g10: Circle CenterX=-11.82 CenterY=24.084 CenterZ=0 NormalX=0 NormalY=0 NormalZ=1 AngleXU=0 Radius=0.5
    g11: Circle CenterX=-9.28 CenterY=24.084 CenterZ=0 NormalX=0 NormalY=0 NormalZ=1 AngleXU=0 Radius=0.5
    g12: LineSegment [constr] StartX=-16.9 StartY=24.084 StartZ=0 EndX=-14.36 EndY=24.084 EndZ=0
    g13: LineSegment [constr] StartX=-14.36 StartY=24.084 StartZ=0 EndX=-11.82 EndY=24.084 EndZ=0
    g14: LineSegment [constr] StartX=-11.82 StartY=24.084 StartZ=0 EndX=-9.28 EndY=24.084 EndZ=0
  constraints (38):
    c: Radius(g0) = 0.5
    c: Horizontal(g1)
    c: DistanceX(g1) = 2.54
    c: Coincident(g2,g1)
    c: Horizontal(g6)
    c: Horizontal(g7)
    c: Horizontal(g8)
    c: Horizontal(g12)
    c: Horizontal(g13)
    c: Horizontal(g14)
    c: Coincident(g6,g1)
    c: Coincident(g3,g6)
    c: Coincident(g3,g7)
    c: Coincident(g4,g7)
    c: Coincident(g8,g4)
    c: Coincident(g5,g8)
    c: Coincident(g12,g5)
    c: Coincident(g9,g12)
    c: Coincident(g13,g9)
    c: Coincident(g10,g13)
    c: Coincident(g14,g10)
    c: Coincident(g11,g14)
    c: Equal(g0,g2)
    c: Equal(g2,g3)
    c: Equal(g3,g4)
    c: Equal(g4,g5)
    c: Equal(g5,g9)
    c: Equal(g9,g10)
    c: Equal(g10,g11)
    c: Equal(g1,g6)
    c: Equal(g6,g7)
    c: Equal(g7,g8)
    c: Equal(g8,g12)
    c: Equal(g12,g13)
    c: Equal(g13,g14)
    c: Coincident(g0,g1)
    c: DistanceX(g-1,g0) = -27.06
    c: DistanceY(g-1,g0) = 24.084
FEATURE [PartDesign::Pocket] Pocket005  label="female-headerx8-1"
  Length = 5
  Length2 = 100
  Profile = -> Sketch007
  Type = 1
FEATURE [Sketcher::SketchObject] Sketch008  label="female-headerx8-2-sketch"
  MapMode = 5
  Placement = pos=(0,0,2) rot=(0,0,1;0rad)
  Support = -> [Pocket005]
  sketch-geometry (15):
    g0: Circle CenterX=-5.216 CenterY=24.084 CenterZ=0 NormalX=0 NormalY=0 NormalZ=1 AngleXU=0 Radius=0.5
    g1: LineSegment [constr] StartX=-5.216 StartY=24.084 StartZ=0 EndX=-2.676 EndY=24.084 EndZ=0
    g2: Circle CenterX=-2.676 CenterY=24.084 CenterZ=0 NormalX=0 NormalY=0 NormalZ=1 AngleXU=0 Radius=0.5
    g3: Circle CenterX=-0.136 CenterY=24.084 CenterZ=0 NormalX=0 NormalY=0 NormalZ=1 AngleXU=0 Radius=0.5
    g4: Circle CenterX=2.404 CenterY=24.084 CenterZ=0 NormalX=0 NormalY=0 NormalZ=1 AngleXU=0 Radius=0.5
    g5: Circle CenterX=4.944 CenterY=24.084 CenterZ=0 NormalX=0 NormalY=0 NormalZ=1 AngleXU=0 Radius=0.5
    g6: LineSegment [constr] StartX=-2.676 StartY=24.084 StartZ=0 EndX=-0.136 EndY=24.084 EndZ=0
    g7: LineSegment [constr] StartX=-0.136 StartY=24.084 StartZ=0 EndX=2.404 EndY=24.084 EndZ=0
    g8: LineSegment [constr] StartX=2.404 StartY=24.084 StartZ=0 EndX=4.944 EndY=24.084 EndZ=0
    g9: Circle CenterX=7.484 CenterY=24.084 CenterZ=0 NormalX=0 NormalY=0 NormalZ=1 AngleXU=0 Radius=0.5
    g10: Circle CenterX=10.024 CenterY=24.084 CenterZ=0 NormalX=0 NormalY=0 NormalZ=1 AngleXU=0 Radius=0.5
    g11: Circle CenterX=12.564 CenterY=24.084 CenterZ=0 NormalX=0 NormalY=0 NormalZ=1 AngleXU=0 Radius=0.5
    g12: LineSegment [constr] StartX=4.944 StartY=24.084 StartZ=0 EndX=7.484 EndY=24.084 EndZ=0
    g13: LineSegment [constr] StartX=7.484 StartY=24.084 StartZ=0 EndX=10.024 EndY=24.084 EndZ=0
    g14: LineSegment [constr] StartX=10.024 StartY=24.084 StartZ=0 EndX=12.564 EndY=24.084 EndZ=0
  constraints (38):
    c: Radius(g0) = 0.5
    c: Horizontal(g1)
    c: DistanceX(g1) = 2.54
    c: Coincident(g2,g1)
    c: Horizontal(g6)
    c: Horizontal(g7)
    c: Horizontal(g8)
    c: Horizontal(g12)
    c: Horizontal(g13)
    c: Horizontal(g14)
    c: Coincident(g6,g1)
    c: Coincident(g3,g6)
    c: Coincident(g3,g7)
    c: Coincident(g4,g7)
    c: Coincident(g8,g4)
    c: Coincident(g5,g8)
    c: Coincident(g12,g5)
    c: Coincident(g9,g12)
    c: Coincident(g13,g9)
    c: Coincident(g10,g13)
    c: Coincident(g14,g10)
    c: Coincident(g11,g14)
    c: Equal(g0,g2)
    c: Equal(g2,g3)
    c: Equal(g3,g4)
    c: Equal(g4,g5)
    c: Equal(g5,g9)
    c: Equal(g9,g10)
    c: Equal(g10,g11)
    c: Equal(g1,g6)
    c: Equal(g6,g7)
    c: Equal(g7,g8)
    c: Equal(g8,g12)
    c: Equal(g12,g13)
    c: Equal(g13,g14)
    c: Coincident(g0,g1)
    c: DistanceX(g-1,g0) = -5.216
    c: DistanceY(g-1,g0) = 24.084
FEATURE [PartDesign::Pocket] Pocket013  label="female-headerx8-2"
  Length = 5
  Length2 = 100
  Profile = -> Sketch008
  Type = 1
FEATURE [Sketcher::SketchObject] Sketch009  label="female-headerx8-3-sketch"
  MapMode = 5
  Placement = pos=(0,0,2) rot=(0,0,1;0rad)
  Support = -> [Pocket013]
  sketch-geometry (15):
    g0: Circle CenterX=17.644 CenterY=24.084 CenterZ=0 NormalX=0 NormalY=0 NormalZ=1 AngleXU=0 Radius=0.5
    g1: LineSegment [constr] StartX=17.644 StartY=24.084 StartZ=0 EndX=20.184 EndY=24.084 EndZ=0
    g2: Circle CenterX=20.184 CenterY=24.084 CenterZ=0 NormalX=0 NormalY=0 NormalZ=1 AngleXU=0 Radius=0.5
    g3: Circle CenterX=22.724 CenterY=24.084 CenterZ=0 NormalX=0 NormalY=0 NormalZ=1 AngleXU=0 Radius=0.5
    g4: Circle CenterX=25.264 CenterY=24.084 CenterZ=0 NormalX=0 NormalY=0 NormalZ=1 AngleXU=0 Radius=0.5
    g5: Circle CenterX=27.804 CenterY=24.084 CenterZ=0 NormalX=0 NormalY=0 NormalZ=1 AngleXU=0 Radius=0.5
    g6: LineSegment [constr] StartX=20.184 StartY=24.084 StartZ=0 EndX=22.724 EndY=24.084 EndZ=0
    g7: LineSegment [constr] StartX=22.724 StartY=24.084 StartZ=0 EndX=25.264 EndY=24.084 EndZ=0
    g8: LineSegment [constr] StartX=25.264 StartY=24.084 StartZ=0 EndX=27.804 EndY=24.084 EndZ=0
    g9: Circle CenterX=30.344 CenterY=24.084 CenterZ=0 NormalX=0 NormalY=0 NormalZ=1 AngleXU=0 Radius=0.5
    g10: Circle CenterX=32.884 CenterY=24.084 CenterZ=0 NormalX=0 NormalY=0 NormalZ=1 AngleXU=0 Radius=0.5
    g11: Circle CenterX=35.424 CenterY=24.084 CenterZ=0 NormalX=0 NormalY=0 NormalZ=1 AngleXU=0 Radius=0.5
    g12: LineSegment [constr] StartX=27.804 StartY=24.084 StartZ=0 EndX=30.344 EndY=24.084 EndZ=0
    g13: LineSegment [constr] StartX=30.344 StartY=24.084 StartZ=0 EndX=32.884 EndY=24.084 EndZ=0
    g14: LineSegment [constr] StartX=32.884 StartY=24.084 StartZ=0 EndX=35.424 EndY=24.084 EndZ=0
  constraints (38):
    c: Radius(g0) = 0.5
    c: Horizontal(g1)
    c: DistanceX(g1) = 2.54
    c: Coincident(g2,g1)
    c: Horizontal(g6)
    c: Horizontal(g7)
    c: Horizontal(g8)
    c: Horizontal(g12)
    c: Horizontal(g13)
    c: Horizontal(g14)
    c: Coincident(g6,g1)
    c: Coincident(g3,g6)
    c: Coincident(g3,g7)
    c: Coincident(g4,g7)
    c: Coincident(g8,g4)
    c: Coincident(g5,g8)
    c: Coincident(g12,g5)
    c: Coincident(g9,g12)
    c: Coincident(g13,g9)
    c: Coincident(g10,g13)
    c: Coincident(g14,g10)
    c: Coincident(g11,g14)
    c: Equal(g0,g2)
    c: Equal(g2,g3)
    c: Equal(g3,g4)
    c: Equal(g4,g5)
    c: Equal(g5,g9)
    c: Equal(g9,g10)
    c: Equal(g10,g11)
    c: Equal(g1,g6)
    c: Equal(g6,g7)
    c: Equal(g7,g8)
    c: Equal(g8,g12)
    c: Equal(g12,g13)
    c: Equal(g13,g14)
    c: Coincident(g0,g1)
    c: DistanceX(g-1,g0) = 17.644
    c: DistanceY(g-1,g0) = 24.084
FEATURE [PartDesign::Pocket] Pocket015  label="female-headerx8-3"
  Length = 5
  Length2 = 100
  Profile = -> Sketch009
  Type = 1
FEATURE [Sketcher::SketchObject] Sketch010  label="female-headerx8-4-sketch"
  MapMode = 5
  Placement = pos=(0,0,2) rot=(0,0,1;0rad)
  Support = -> [Pocket015]
  sketch-geometry (11):
    g0: Circle CenterX=-17.916 CenterY=-24.176 CenterZ=0 NormalX=0 NormalY=0 NormalZ=1 AngleXU=0 Radius=0.5
    g1: LineSegment [constr] StartX=-17.916 StartY=-24.176 StartZ=0 EndX=-15.376 EndY=-24.176 EndZ=0
    g2: Circle CenterX=-15.376 CenterY=-24.176 CenterZ=0 NormalX=0 NormalY=0 NormalZ=1 AngleXU=0 Radius=0.5
    g3: Circle CenterX=-12.836 CenterY=-24.176 CenterZ=0 NormalX=0 NormalY=0 NormalZ=1 AngleXU=0 Radius=0.5
    g4: Circle CenterX=-10.296 CenterY=-24.176 CenterZ=0 NormalX=0 NormalY=0 NormalZ=1 AngleXU=0 Radius=0.5
    g5: Circle CenterX=-7.756 CenterY=-24.176 CenterZ=0 NormalX=0 NormalY=0 NormalZ=1 AngleXU=0 Radius=0.5
    g6: LineSegment [constr] StartX=-15.376 StartY=-24.176 StartZ=0 EndX=-12.836 EndY=-24.176 EndZ=0
    g7: LineSegment [constr] StartX=-12.836 StartY=-24.176 StartZ=0 EndX=-10.296 EndY=-24.176 EndZ=0
    g8: LineSegment [constr] StartX=-10.296 StartY=-24.176 StartZ=0 EndX=-7.756 EndY=-24.176 EndZ=0
    g9: Circle CenterX=-5.216 CenterY=-24.176 CenterZ=0 NormalX=0 NormalY=0 NormalZ=1 AngleXU=0 Radius=0.5
    g10: LineSegment [constr] StartX=-7.756 StartY=-24.176 StartZ=0 EndX=-5.216 EndY=-24.176 EndZ=0
  constraints (28):
    c: Radius(g0) = 0.5
    c: Horizontal(g1)
    c: DistanceX(g1) = 2.54
    c: Coincident(g2,g1)
    c: Horizontal(g6)
    c: Horizontal(g7)
    c: Horizontal(g8)
    c: Horizontal(g10)
    c: Coincident(g6,g1)
    c: Coincident(g3,g6)
    c: Coincident(g3,g7)
    c: Coincident(g4,g7)
    c: Coincident(g8,g4)
    c: Coincident(g5,g8)
    c: Coincident(g10,g5)
    c: Coincident(g9,g10)
    c: Equal(g0,g2)
    c: Equal(g2,g3)
    c: Equal(g3,g4)
    c: Equal(g4,g5)
    c: Equal(g5,g9)
    c: Equal(g1,g6)
    c: Equal(g6,g7)
    c: Equal(g7,g8)
    c: Equal(g8,g10)
    c: Coincident(g0,g1)
    c: DistanceX(g-1,g0) = -17.916
    c: DistanceY(g-1,g0) = -24.176
FEATURE [PartDesign::Pocket] Pocket007  label="female-headerx8-4"
  Length = 5
  Length2 = 100
  Profile = -> Sketch010
  Type = 1
FEATURE [Sketcher::SketchObject] Sketch011  label="female-headerx8-5-sketch"
  MapMode = 5
  Placement = pos=(0,0,2) rot=(0,0,1;0rad)
  Support = -> [Pocket007]
  sketch-geometry (15):
    g0: Circle CenterX=0.136 CenterY=-24.176 CenterZ=0 NormalX=0 NormalY=0 NormalZ=1 AngleXU=0 Radius=0.5
    g1: LineSegment [constr] StartX=0.136 StartY=-24.176 StartZ=0 EndX=2.676 EndY=-24.176 EndZ=0
    g2: Circle CenterX=2.676 CenterY=-24.176 CenterZ=0 NormalX=0 NormalY=0 NormalZ=1 AngleXU=0 Radius=0.5
    g3: Circle CenterX=5.216 CenterY=-24.176 CenterZ=0 NormalX=0 NormalY=0 NormalZ=1 AngleXU=0 Radius=0.5
    g4: Circle CenterX=7.756 CenterY=-24.176 CenterZ=0 NormalX=0 NormalY=0 NormalZ=1 AngleXU=0 Radius=0.5
    g5: Circle CenterX=10.296 CenterY=-24.176 CenterZ=0 NormalX=0 NormalY=0 NormalZ=1 AngleXU=0 Radius=0.5
    g6: LineSegment [constr] StartX=2.676 StartY=-24.176 StartZ=0 EndX=5.216 EndY=-24.176 EndZ=0
    g7: LineSegment [constr] StartX=5.216 StartY=-24.176 StartZ=0 EndX=7.756 EndY=-24.176 EndZ=0
    g8: LineSegment [constr] StartX=7.756 StartY=-24.176 StartZ=0 EndX=10.296 EndY=-24.176 EndZ=0
    g9: Circle CenterX=12.836 CenterY=-24.176 CenterZ=0 NormalX=0 NormalY=0 NormalZ=1 AngleXU=0 Radius=0.5
    g10: Circle CenterX=15.376 CenterY=-24.176 CenterZ=0 NormalX=0 NormalY=0 NormalZ=1 AngleXU=0 Radius=0.5
    g11: Circle CenterX=17.916 CenterY=-24.176 CenterZ=0 NormalX=0 NormalY=0 NormalZ=1 AngleXU=0 Radius=0.5
    g12: LineSegment [constr] StartX=10.296 StartY=-24.176 StartZ=0 EndX=12.836 EndY=-24.176 EndZ=0
    g13: LineSegment [constr] StartX=12.836 StartY=-24.176 StartZ=0 EndX=15.376 EndY=-24.176 EndZ=0
    g14: LineSegment [constr] StartX=15.376 StartY=-24.176 StartZ=0 EndX=17.916 EndY=-24.176 EndZ=0
  constraints (38):
    c: Radius(g0) = 0.5
    c: Horizontal(g1)
    c: DistanceX(g1) = 2.54
    c: Coincident(g2,g1)
    c: Horizontal(g6)
    c: Horizontal(g7)
    c: Horizontal(g8)
    c: Horizontal(g12)
    c: Horizontal(g13)
    c: Horizontal(g14)
    c: Coincident(g6,g1)
    c: Coincident(g3,g6)
    c: Coincident(g3,g7)
    c: Coincident(g4,g7)
    c: Coincident(g8,g4)
    c: Coincident(g5,g8)
    c: Coincident(g12,g5)
    c: Coincident(g9,g12)
    c: Coincident(g13,g9)
    c: Coincident(g10,g13)
    c: Coincident(g14,g10)
    c: Coincident(g11,g14)
    c: Equal(g0,g2)
    c: Equal(g2,g3)
    c: Equal(g3,g4)
    c: Equal(g4,g5)
    c: Equal(g5,g9)
    c: Equal(g9,g10)
    c: Equal(g10,g11)
    c: Equal(g1,g6)
    c: Equal(g6,g7)
    c: Equal(g7,g8)
    c: Equal(g8,g12)
    c: Equal(g12,g13)
    c: Equal(g13,g14)
    c: Coincident(g0,g1)
    c: DistanceX(g-1,g0) = 0.136
    c: DistanceY(g-1,g0) = -24.176
FEATURE [PartDesign::Pocket] Pocket008  label="female-headerx8-5"
  Length = 5
  Length2 = 100
  Profile = -> Sketch011
  Type = 1
FEATURE [Sketcher::SketchObject] Sketch012  label="female-headerx8-6-sketch"
  MapMode = 5
  Placement = pos=(0,0,2) rot=(0,0,1;0rad)
  Support = -> [Pocket008]
  sketch-geometry (15):
    g0: Circle CenterX=22.724 CenterY=-24.176 CenterZ=0 NormalX=0 NormalY=0 NormalZ=1 AngleXU=0 Radius=0.5
    g1: LineSegment [constr] StartX=22.724 StartY=-24.176 StartZ=0 EndX=25.264 EndY=-24.176 EndZ=0
    g2: Circle CenterX=25.264 CenterY=-24.176 CenterZ=0 NormalX=0 NormalY=0 NormalZ=1 AngleXU=0 Radius=0.5
    g3: Circle CenterX=27.804 CenterY=-24.176 CenterZ=0 NormalX=0 NormalY=0 NormalZ=1 AngleXU=0 Radius=0.5
    g4: Circle CenterX=30.344 CenterY=-24.176 CenterZ=0 NormalX=0 NormalY=0 NormalZ=1 AngleXU=0 Radius=0.5
    g5: Circle CenterX=32.884 CenterY=-24.176 CenterZ=0 NormalX=0 NormalY=0 NormalZ=1 AngleXU=0 Radius=0.5
    g6: LineSegment [constr] StartX=25.264 StartY=-24.176 StartZ=0 EndX=27.804 EndY=-24.176 EndZ=0
    g7: LineSegment [constr] StartX=27.804 StartY=-24.176 StartZ=0 EndX=30.344 EndY=-24.176 EndZ=0
    g8: LineSegment [constr] StartX=30.344 StartY=-24.176 StartZ=0 EndX=32.884 EndY=-24.176 EndZ=0
    g9: Circle CenterX=35.424 CenterY=-24.176 CenterZ=0 NormalX=0 NormalY=0 NormalZ=1 AngleXU=0 Radius=0.5
    g10: Circle CenterX=37.964 CenterY=-24.176 CenterZ=0 NormalX=0 NormalY=0 NormalZ=1 AngleXU=0 Radius=0.5
    g11: Circle CenterX=40.504 CenterY=-24.176 CenterZ=0 NormalX=0 NormalY=0 NormalZ=1 AngleXU=0 Radius=0.5
    g12: LineSegment [constr] StartX=32.884 StartY=-24.176 StartZ=0 EndX=35.424 EndY=-24.176 EndZ=0
    g13: LineSegment [constr] StartX=35.424 StartY=-24.176 StartZ=0 EndX=37.964 EndY=-24.176 EndZ=0
    g14: LineSegment [constr] StartX=37.964 StartY=-24.176 StartZ=0 EndX=40.504 EndY=-24.176 EndZ=0
  constraints (38):
    c: Radius(g0) = 0.5
    c: Horizontal(g1)
    c: DistanceX(g1) = 2.54
    c: Coincident(g2,g1)
    c: Horizontal(g6)
    c: Horizontal(g7)
    c: Horizontal(g8)
    c: Horizontal(g12)
    c: Horizontal(g13)
    c: Horizontal(g14)
    c: Coincident(g6,g1)
    c: Coincident(g3,g6)
    c: Coincident(g3,g7)
    c: Coincident(g4,g7)
    c: Coincident(g8,g4)
    c: Coincident(g5,g8)
    c: Coincident(g12,g5)
    c: Coincident(g9,g12)
    c: Coincident(g13,g9)
    c: Coincident(g10,g13)
    c: Coincident(g14,g10)
    c: Coincident(g11,g14)
    c: Equal(g0,g2)
    c: Equal(g2,g3)
    c: Equal(g3,g4)
    c: Equal(g4,g5)
    c: Equal(g5,g9)
    c: Equal(g9,g10)
    c: Equal(g10,g11)
    c: Equal(g1,g6)
    c: Equal(g6,g7)
    c: Equal(g7,g8)
    c: Equal(g8,g12)
    c: Equal(g12,g13)
    c: Equal(g13,g14)
    c: Coincident(g0,g1)
    c: DistanceY(g-1,g0) = -24.176
    c: DistanceX(g-1,g0) = 22.724
FEATURE [PartDesign::Pocket] Pocket009  label="female-headerx8-6"
  Length = 5
  Length2 = 100
  Profile = -> Sketch012
  Type = 1
FEATURE [Sketcher::SketchObject] Sketch013  label="female-double-header-sketch"
  MapMode = 5
  Placement = pos=(0,0,2) rot=(0,0,1;0rad)
  Support = -> [Pocket009]
  sketch-geometry (3):
    g0: Circle CenterX=43.044 CenterY=24.084 CenterZ=0 NormalX=0 NormalY=0 NormalZ=1 AngleXU=0 Radius=0.5
    g1: Circle CenterX=45.584 CenterY=24.084 CenterZ=0 NormalX=0 NormalY=0 NormalZ=1 AngleXU=0 Radius=0.5
    g2: LineSegment [constr] StartX=43.044 StartY=24.084 StartZ=0 EndX=45.584 EndY=24.084 EndZ=0
  constraints (8):
    c: Equal(g0,g1)
    c: Radius(g0) = 0.5
    c: Horizontal(g2)
    c: DistanceX(g2) = 2.54
    c: Coincident(g2,g0)
    c: Coincident(g2,g1)
    c: DistanceX(g-1,g0) = 43.044
    c: DistanceY(g-1,g0) = 24.084
FEATURE [PartDesign::Pocket] Pocket010  label="female-double-header-master"
  Length = 5
  Length2 = 100
  Profile = -> Sketch013
  Type = 1
FEATURE [PartDesign::LinearPattern] LinearPattern  label="female-double-header"
  Direction = -> Sketch013 [V_Axis]
  Length = 43.18
  Occurrences = 18
  Originals = -> [Pocket010]
  Reversed = true
FEATURE [App::DocumentObjectGroup] Group003  label="PCB-src"
  Group = -> [Pad001002,Pocket006,Pocket014,Pocket011,Pocket012,Pocket005,Pocket013,Pocket015,Pocket007,Pocket008,Pocket009,Pocket010,LinearPattern]
FEATURE [Part::Compound] Compound060  label="1x8-female-pin-header-005"
  Placement = pos=(17.644,24.084,2) rot=(0,0,1;0rad)
FEATURE [Part::Compound] Compound059  label="Arduino-mega"
  Links = -> [LinearPattern001,Fusion004,Compound056,Pad001001,Compound053,Compound055,Compound052,Compound051,Compound058,Compound060,Compound057,Compound054]
FEATURE [App::Part] Part  label="Arduino-Mega"
  Group = -> [Sketch014,Pad003,Group002,Pocket011,Sketch017,LinearPattern,Sketch008,Sketch013,Sketch019,Sketch016,Pocket009,Pocket015,Sketch015,Sketch009,Pocket014,Sketch012,Pad001002,Pocket012,Pocket008,Pocket005,Pocket010,Pocket013,Pocket007,Sketch011,Pocket006,Sketch007,Sketch018,Sketch010,Group003,Compound054,Fusion002,Pad001001,Compound057,LinearPattern001,Fusion003,Compound055,Compound060,Compound053,+7 more]
  License = CC BY 3.0
  LicenseURL = http://creativecommons.org/licenses/by/3.0/
  Origin = -> Origin
FEATURE [Part::Compound] Compound061  label="Beam_Coupling_5mm_8mm_Right"
  Placement = pos=(11,133.5,360) rot=(0,0,1;0rad)
FEATURE [Sketcher::SketchObject] Sketch025
  MapMode = 5
  Placement = pos=(0,0,0) rot=(1,0,0;1.5708rad)
  sketch-geometry (8):
    g0: LineSegment StartX=-9 StartY=10 StartZ=0 EndX=9 EndY=10 EndZ=0
    g1: LineSegment StartX=10 StartY=9 StartZ=0 EndX=10 EndY=-9 EndZ=0
    g2: LineSegment StartX=9 StartY=-10 StartZ=0 EndX=-9 EndY=-10 EndZ=0
    g3: LineSegment StartX=-10 StartY=-9 StartZ=0 EndX=-10 EndY=9 EndZ=0
    g4: ArcOfCircle CenterX=-9 CenterY=9 CenterZ=0 NormalX=0 NormalY=0 NormalZ=1 AngleXU=0 Radius=1 StartAngle=1.5708 EndAngle=3.14159
    g5: ArcOfCircle CenterX=-9 CenterY=-9 CenterZ=0 NormalX=0 NormalY=0 NormalZ=1 AngleXU=0 Radius=1 StartAngle=3.14159 EndAngle=4.71239
    g6: ArcOfCircle CenterX=9 CenterY=-9 CenterZ=0 NormalX=0 NormalY=0 NormalZ=1 AngleXU=0 Radius=1 StartAngle=4.71239 EndAngle=6.28319
    g7: ArcOfCircle CenterX=9 CenterY=9 CenterZ=0 NormalX=0 NormalY=0 NormalZ=1 AngleXU=0 Radius=1 StartAngle=0 EndAngle=1.5708
  constraints (20):
    c: Horizontal(g0)
    c: Horizontal(g2)
    c: Vertical(g1)
    c: Vertical(g3)
    c: Tangent(g0,g4) = 1.5708
    c: Tangent(g3,g4) = 1.5708
    c: Tangent(g3,g5) = 1.5708
    c: Tangent(g2,g5) = 1.5708
    c: Tangent(g2,g6) = 1.5708
    c: Tangent(g1,g6) = 1.5708
    c: Tangent(g0,g7) = 1.5708
    c: Tangent(g1,g7) = 1.5708
    c: Equal(g7,g4)
    c: Equal(g4,g5)
    c: Equal(g5,g6)
    c: Radius(g7) = 1
    c: DistanceX(g1,g3) = -20
    c: DistanceX(g-1,g1) = 10
    c: DistanceY(g0,g2) = -20
    c: DistanceY(g-1,g0) = 10
FEATURE [PartDesign::Pad] Pad001003
  Length = 445
  Length2 = 100
  Placement = pos=(0,0,0) rot=(1,0,0;1.5708rad)
  Profile = -> Sketch025
  Type = 0
FEATURE [Sketcher::SketchObject] Sketch027
  MapMode = 5
  Placement = pos=(0,-445,9.79e-14) rot=(1,0,0;1.5708rad)
  Support = -> [Pad001003]
  sketch-geometry (17):
    g0: LineSegment StartX=-3.4 StartY=10 StartZ=0 EndX=-3.4 EndY=9.6 EndZ=0
    g1: LineSegment StartX=-3.4 StartY=9.6 StartZ=0 EndX=-3 EndY=9.6 EndZ=0
    g2: LineSegment StartX=-3 StartY=9.6 StartZ=0 EndX=-3 EndY=8.5 EndZ=0
    g3: LineSegment StartX=-3 StartY=8.5 StartZ=0 EndX=-6 EndY=8.5 EndZ=0
    g4: LineSegment StartX=-6 StartY=8.5 StartZ=0 EndX=-6 EndY=7 EndZ=0
    g5: LineSegment StartX=-6 StartY=7 StartZ=0 EndX=-3.35 EndY=4.7 EndZ=0
    g6: LineSegment StartX=-3.35 StartY=4.7 StartZ=0 EndX=-0.65 EndY=4.7 EndZ=0
    g7: LineSegment StartX=-0.65 StartY=4.7 StartZ=0 EndX=0 EndY=4.3 EndZ=0
    g8: LineSegment StartX=0 StartY=4.3 StartZ=0 EndX=0.65 EndY=4.7 EndZ=0
    g9: LineSegment StartX=0.65 StartY=4.7 StartZ=0 EndX=3.35 EndY=4.7 EndZ=0
    g10: LineSegment StartX=3.35 StartY=4.7 StartZ=0 EndX=6 EndY=7 EndZ=0
    g11: LineSegment StartX=6 StartY=7 StartZ=0 EndX=6 EndY=8.5 EndZ=0
    g12: LineSegment StartX=6 StartY=8.5 StartZ=0 EndX=3 EndY=8.5 EndZ=0
    g13: LineSegment StartX=3 StartY=8.5 StartZ=0 EndX=3 EndY=9.6 EndZ=0
    g14: LineSegment StartX=3 StartY=9.6 StartZ=0 EndX=3.4 EndY=9.6 EndZ=0
    g15: LineSegment StartX=3.4 StartY=9.6 StartZ=0 EndX=3.4 EndY=10 EndZ=0
    g16: LineSegment StartX=3.4 StartY=10 StartZ=0 EndX=-3.4 EndY=10 EndZ=0
  constraints (51):
    c: Coincident(g0,g1)
    c: Horizontal(g1)
    c: Coincident(g1,g2)
    c: Vertical(g2)
    c: Coincident(g2,g3)
    c: Horizontal(g3)
    c: Coincident(g3,g4)
    c: Vertical(g4)
    c: Coincident(g4,g5)
    c: Coincident(g5,g6)
    c: Horizontal(g6)
    c: Coincident(g6,g7)
    c: Coincident(g7,g8)
    c: Coincident(g8,g9)
    c: Horizontal(g9)
    c: Coincident(g9,g10)
    c: Coincident(g10,g11)
    c: Coincident(g11,g12)
    c: Horizontal(g12)
    c: Coincident(g12,g13)
    c: Vertical(g13)
    c: Coincident(g13,g14)
    c: Horizontal(g14)
    c: Coincident(g14,g15)
    c: Vertical(g15)
    c: Coincident(g15,g16)
    c: Horizontal(g16)
    c: Vertical(g0)
    c: PointOnObject(g7,g-2)
    c: Coincident(g0,g16)
    c: DistanceX(g2,g12) = 6
    c: DistanceX(g-1,g12) = 3
    c: Vertical(g11)
    c: DistanceY(g4) = -1.5
    c: DistanceY(g11) = 1.5
    c: DistanceY(g13) = 1.1
    c: DistanceY(g2) = -1.1
    c: DistanceY(g15) = 0.4
    c: DistanceY(g0) = -0.4
    c: DistanceY(g-1,g15) = 10
    c: DistanceX(g1) = 0.4
    c: DistanceX(g14) = 0.4
    c: DistanceX(g3) = -3
    c: DistanceX(g12) = -3
    c: DistanceX(g6) = 2.7
    c: DistanceX(g9) = 2.7
    c: DistanceX(g6,g8) = 1.3
    c: DistanceX(g-1,g6) = -0.65
    c: DistanceY(g8) = 0.4
    c: DistanceY(g7) = -0.4
    c: DistanceY(g15,g9) = -5.3
FEATURE [PartDesign::Pocket] Pocket020
  Length = 445
  Length2 = 100
  Placement = pos=(0,0,0) rot=(1,0,0;1.5708rad)
  Profile = -> Sketch027
  Type = 0
FEATURE [PartDesign::PolarPattern] PolarPattern001
  Angle = 360
  Axis = -> Sketch027 [N_Axis]
  Occurrences = 4
  Originals = -> [Pocket020]
  Placement = pos=(0,0,0) rot=(1,0,0;1.5708rad)
FEATURE [Sketcher::SketchObject] Sketch026
  MapMode = 5
  Placement = pos=(0,-445,9.79e-14) rot=(1,0,0;1.5708rad)
  Support = -> [PolarPattern001]
  sketch-geometry (20):
    g0: ArcOfCircle CenterX=0 CenterY=0 CenterZ=0 NormalX=0 NormalY=0 NormalZ=1 AngleXU=0 Radius=2.75 StartAngle=1.06162 EndAngle=2.07997
    g1: ArcOfCircle CenterX=0 CenterY=0 CenterZ=0 NormalX=0 NormalY=0 NormalZ=1 AngleXU=0 Radius=2.75 StartAngle=2.63242 EndAngle=3.65076
    g2: ArcOfCircle CenterX=0 CenterY=0 CenterZ=0 NormalX=0 NormalY=0 NormalZ=1 AngleXU=0 Radius=2.75 StartAngle=4.20322 EndAngle=5.22156
    g3: ArcOfCircle CenterX=0 CenterY=0 CenterZ=0 NormalX=0 NormalY=0 NormalZ=1 AngleXU=0 Radius=2.75 StartAngle=5.77401 EndAngle=6.79236
    g4: LineSegment StartX=-2.40116 StartY=1.3405 StartZ=0 EndX=-3.0052 EndY=1.94454 EndZ=0
    g5: LineSegment StartX=-3.0052 StartY=1.94454 StartZ=0 EndX=-1.94454 EndY=3.0052 EndZ=0
    g6: LineSegment StartX=-1.94454 StartY=3.0052 StartZ=0 EndX=-1.3405 EndY=2.40116 EndZ=0
    g7: LineSegment [constr] StartX=-2.47487 StartY=2.47487 StartZ=0 EndX=0 EndY=0 EndZ=0
    g8: LineSegment [constr] StartX=0 StartY=0 StartZ=0 EndX=-2.47487 EndY=-2.47487 EndZ=0
    g9: LineSegment [constr] StartX=0 StartY=0 StartZ=0 EndX=2.47487 EndY=-2.47487 EndZ=0
    g10: LineSegment [constr] StartX=0 StartY=0 StartZ=0 EndX=2.47487 EndY=2.47487 EndZ=0
    g11: LineSegment StartX=2.40116 StartY=1.3405 StartZ=0 EndX=3.0052 EndY=1.94454 EndZ=0
    g12: LineSegment StartX=3.0052 StartY=1.94454 StartZ=0 EndX=1.94454 EndY=3.0052 EndZ=0
    g13: LineSegment StartX=1.94454 StartY=3.0052 StartZ=0 EndX=1.3405 EndY=2.40116 EndZ=0
    g14: LineSegment StartX=2.40116 StartY=-1.3405 StartZ=0 EndX=3.0052 EndY=-1.94454 EndZ=0
    g15: LineSegment StartX=3.0052 StartY=-1.94454 StartZ=0 EndX=1.94454 EndY=-3.0052 EndZ=0
    g16: LineSegment StartX=1.94454 StartY=-3.0052 StartZ=0 EndX=1.3405 EndY=-2.40116 EndZ=0
    g17: LineSegment StartX=-1.3405 StartY=-2.40116 StartZ=0 EndX=-1.94454 EndY=-3.0052 EndZ=0
    g18: LineSegment StartX=-1.94454 StartY=-3.0052 StartZ=0 EndX=-3.0052 EndY=-1.94454 EndZ=0
    g19: LineSegment StartX=-3.0052 StartY=-1.94454 StartZ=0 EndX=-2.40116 EndY=-1.3405 EndZ=0
  constraints (60):
    c: Coincident(g3,g-1)
    c: Coincident(g0,g-1)
    c: Coincident(g1,g-1)
    c: Coincident(g2,g-1)
    c: Equal(g0,g3)
    c: Equal(g3,g2)
    c: Equal(g2,g1)
    c: Radius(g0) = 2.75
    c: Coincident(g4,g5)
    c: Coincident(g5,g6)
    c: Perpendicular(g5,g6) = 4.71239
    c: Perpendicular(g4,g5) = 4.71239
    c: Coincident(g0,g6)
    c: Coincident(g1,g4)
    c: Coincident(g7,g-1)
    c: Angle(g-2,g7) = 0.785398
    c: PointOnObject(g7,g5)
    c: Parallel(g7,g6)
    c: Coincident(g8,g-1)
    c: Angle(g7,g8) = 1.5708
    c: Coincident(g9,g-1)
    c: Angle(g8,g9) = 1.5708
    c: Coincident(g10,g-1)
    c: Angle(g9,g10) = 1.5708
    c: Coincident(g11,g12)
    c: Coincident(g12,g13)
    c: Perpendicular(g12,g13) = 1.5708
    c: Perpendicular(g11,g12) = 1.5708
    c: Parallel(g10,g13)
    c: PointOnObject(g10,g12)
    c: Equal(g7,g10)
    c: Equal(g10,g8)
    c: Equal(g8,g9)
    c: Distance(g7) = 3.5
    c: Coincident(g0,g13)
    c: Coincident(g11,g3)
    c: Coincident(g14,g15)
    c: Coincident(g15,g16)
    c: Perpendicular(g15,g16) = 4.71239
    c: Perpendicular(g14,g15) = 4.71239
    c: Parallel(g9,g14)
    c: Coincident(g3,g14)
    c: PointOnObject(g9,g15)
    c: Coincident(g16,g2)
    c: Coincident(g17,g18)
    c: Coincident(g18,g19)
    c: Perpendicular(g18,g19) = 4.71239
    c: Perpendicular(g17,g18) = 4.71239
    c: Parallel(g8,g19)
    c: PointOnObject(g8,g18)
    c: Coincident(g19,g1)
    c: Coincident(g2,g17)
    c: Equal(g12,g5)
    c: Equal(g5,g18)
    c: Equal(g18,g15)
    c: Distance(g12) = 1.5
    c: Distance(g11,g10) = 0.75
    c: Distance(g7,g5) = 0.75
    c: Distance(g8,g17) = 0.75
    c: Distance(g9,g14) = 0.75
FEATURE [PartDesign::Pocket] Pocket021
  Length = 445
  Length2 = 100
  Placement = pos=(0,0,0) rot=(1,0,0;1.5708rad)
  Profile = -> Sketch026
  Type = 0
FEATURE [Part::Cylinder] Cylinder012022
  Angle = 360
  AttacherType = Attacher::AttachEngine3D
  Height = 3
  Placement = pos=(4.6,17.8,6.5) rot=(1,0,0;1.5708rad)
  Radius = 6.85
FEATURE [Part::Cylinder] Cylinder012023
  Angle = 360
  AttacherType = Attacher::AttachEngine3D
  Height = 17.5
  Placement = pos=(19,17,6.5) rot=(1,0,0;1.5708rad)
  Radius = 2.45
FEATURE [Part::Box] Box007
  AttacherType = Attacher::AttachEngine3D
  Height = 8.2
  Length = 6
  Placement = pos=(12.5,1.6,1.5) rot=(0,0,1;0rad)
  Width = 13.6
FEATURE [Part::Cylinder] Cylinder012024
  Angle = 360
  AttacherType = Attacher::AttachEngine3D
  Height = 15.8
  Placement = pos=(4.5,16.3,6.5) rot=(1,0,0;1.5708rad)
  Radius = 1.85
FEATURE [Sketcher::SketchObject] Sketch029  label="inner-room-male-sketch"
  MapMode = 5
  Placement = pos=(0,0,0) rot=(1,0,0;1.5708rad)
  sketch-geometry (2):
    g0: ArcOfCircle CenterX=13 CenterY=0 CenterZ=0 NormalX=0 NormalY=0 NormalZ=1 AngleXU=0 Radius=6.45 StartAngle=1.5708 EndAngle=4.71239
    g1: LineSegment StartX=13 StartY=6.45 StartZ=0 EndX=13 EndY=-6.45 EndZ=0
  constraints (8):
    c: Radius(g0) = 6.45
    c: PointOnObject(g0,g-1)
    c: Symmetric(g0,g0,g-1)
    c: DistanceX(g-1,g0) = 13
    c: Vertical(g1)
    c: Coincident(g1,g0)
    c: Coincident(g1,g0)
    c: PointOnObject(g0,g1)
FEATURE [PartDesign::Pad] Pad001005  label="inner-room-male"
  Length = 13
  Length2 = 100
  Midplane = true
  Placement = pos=(0,0,0) rot=(1,0,0;1.5708rad)
  Profile = -> Sketch029
  Type = 0
FEATURE [Part::Box] Box009
  AttacherType = Attacher::AttachEngine3D
  Height = 3
  Length = 11
  Placement = pos=(12.5,3.1,7.1) rot=(1,0,0;0.523599rad)
  Width = 3
FEATURE [Sketcher::SketchObject] Sketch031  label="main-body-sketch"
  MapMode = 5
  Placement = pos=(0,0,0) rot=(1,0,0;1.5708rad)
  sketch-geometry (8):
    g0: Circle [constr] CenterX=13 CenterY=0 CenterZ=0 NormalX=0 NormalY=0 NormalZ=1 AngleXU=0 Radius=2.325
    g1: Circle [constr] CenterX=0 CenterY=0 CenterZ=0 NormalX=0 NormalY=0 NormalZ=1 AngleXU=0 Radius=2.25
    g2: LineSegment [constr] StartX=0.325 StartY=6.25 StartZ=0 EndX=0.325 EndY=-6.25 EndZ=0
    g3: ArcOfCircle CenterX=0.325 CenterY=0 CenterZ=0 NormalX=0 NormalY=0 NormalZ=1 AngleXU=0 Radius=6.25 StartAngle=1.5708 EndAngle=4.71239
    g4: LineSegment [constr] StartX=12.675 StartY=6.25 StartZ=0 EndX=12.675 EndY=-6.25 EndZ=0
    g5: LineSegment StartX=0.325 StartY=6.25 StartZ=0 EndX=12.675 EndY=6.25 EndZ=0
    g6: LineSegment StartX=0.325 StartY=-6.25 StartZ=0 EndX=12.675 EndY=-6.25 EndZ=0
    g7: ArcOfCircle CenterX=12.675 CenterY=0 CenterZ=0 NormalX=0 NormalY=0 NormalZ=1 AngleXU=0 Radius=6.25 StartAngle=4.71239 EndAngle=7.85398
  constraints (24):
    c: PointOnObject(g0,g-1)
    c: Radius(g0) = 2.325
    c: Coincident(g1,g-1)
    c: Radius(g1) = 2.25
    c: DistanceX(g-1,g0) = 13
    c: Vertical(g2)
    c: Coincident(g3,g2)
    c: Coincident(g3,g2)
    c: Radius(g3) = 6.25
    c: PointOnObject(g3,g-1)
    c: DistanceX(g-1,g3) = 0.325
    c: PointOnObject(g3,g2)
    c: Vertical(g4)
    c: Horizontal(g5)
    c: Coincident(g5,g2)
    c: Coincident(g5,g4)
    c: Horizontal(g6)
    c: Coincident(g6,g2)
    c: Coincident(g6,g4)
    c: PointOnObject(g7,g-1)
    c: DistanceX(g7,g0) = 0.325
    c: Coincident(g7,g4)
    c: Coincident(g7,g4)
    c: PointOnObject(g7,g4)
FEATURE [PartDesign::Pad] Pad001007  label="main-body001"
  Length = 16
  Length2 = 100
  Midplane = true
  Placement = pos=(0,0,0) rot=(1,0,0;1.5708rad)
  Profile = -> Sketch031
  Type = 0
FEATURE [Part::Box] Box006
  AttacherType = Attacher::AttachEngine3D
  Height = 9.7
  Length = 10
  Placement = pos=(15.35,1.6,0) rot=(0,0,1;0rad)
  Width = 13.6
FEATURE [Part::Box] Box004
  AttacherType = Attacher::AttachEngine3D
  Height = 10
  Length = 26
  Placement = pos=(-1,3.4,1.5) rot=(0,0,1;0rad)
  Width = 10
FEATURE [Part::Cylinder] Cylinder012025
  Angle = 360
  AttacherType = Attacher::AttachEngine3D
  Height = 3
  Placement = pos=(4.6,2,6.5) rot=(1,0,0;1.5708rad)
  Radius = 6.85
FEATURE [Part::Box] Box005
  AttacherType = Attacher::AttachEngine3D
  Height = 13
  Length = 8
  Placement = pos=(-1,3.4,-1.5) rot=(0,0,1;0rad)
  Width = 10
FEATURE [Part::Feature] Cut003002  label="cable-chain-link-2-ex"
  Placement = pos=(13,4e-15,2e-15) rot=(0,0,1;0rad)
  shape: bbox 24.85 x 16 x 12.5 mm, 29 faces (baked)
FEATURE [Part::Cylinder] Cylinder012026
  Angle = 360
  AttacherType = Attacher::AttachEngine3D
  Height = 17.5
  Placement = pos=(5,17,5.5) rot=(1,0,0;1.5708rad)
  Radius = 5.5
FEATURE [Part::Feature] Cut003001  label="cable-chain-link-1"
  shape: bbox 24.85 x 16 x 12.5 mm, 29 faces (baked)
FEATURE [Part::Box] Box002
  AttacherType = Attacher::AttachEngine3D
  Height = 5
  Length = 9
  Placement = pos=(-0.8,-1,6.4) rot=(0,-1,0;0.610866rad)
  Width = 18
FEATURE [Sketcher::SketchObject] Sketch034  label="top-cutout-1-sketch"
  ExternalGeometry = -> [Pad001007]
  MapMode = 5
  Placement = pos=(0,1.4e-15,6.25) rot=(0,0,1;3.14159rad)
  Support = -> [Pad001007]
  sketch-geometry (11):
    g0: LineSegment [constr] StartX=-6.45 StartY=8 StartZ=0 EndX=9.55 EndY=8 EndZ=0
    g1: LineSegment StartX=9.55 StartY=8 StartZ=0 EndX=9.55 EndY=6.5 EndZ=0
    g2: LineSegment StartX=9.55 StartY=6.5 StartZ=0 EndX=-6.45 EndY=6.5 EndZ=0
    g3: LineSegment StartX=-6.45 StartY=6.5 StartZ=0 EndX=-6.45 EndY=8 EndZ=0
    g4: LineSegment StartX=-6.45 StartY=-6.5 StartZ=0 EndX=9.55 EndY=-6.5 EndZ=0
    g5: LineSegment StartX=9.55 StartY=-6.5 StartZ=0 EndX=9.55 EndY=-9 EndZ=0
    g6: LineSegment StartX=9.55 StartY=-9 StartZ=0 EndX=-6.45 EndY=-9 EndZ=0
    g7: LineSegment StartX=-6.45 StartY=-9 StartZ=0 EndX=-6.45 EndY=-6.5 EndZ=0
    g8: LineSegment StartX=-6.45 StartY=9 StartZ=0 EndX=9.55 EndY=9 EndZ=0
    g9: LineSegment StartX=9.55 StartY=9 StartZ=0 EndX=9.55 EndY=8 EndZ=0
    g10: LineSegment StartX=-6.45 StartY=8 StartZ=0 EndX=-6.45 EndY=9 EndZ=0
  constraints (31):
    c: Coincident(g0,g1)
    c: Coincident(g1,g2)
    c: Coincident(g2,g3)
    c: Coincident(g3,g0)
    c: Horizontal(g0)
    c: Horizontal(g2)
    c: Vertical(g1)
    c: Vertical(g3)
    c: PointOnObject(g0,g-3)
    c: DistanceY(g3) = 1.5
    c: DistanceX(g-1,g2) = -6.45
    c: DistanceX(g2) = -16
    c: Coincident(g4,g5)
    c: Coincident(g5,g6)
    c: Coincident(g6,g7)
    c: Coincident(g7,g4)
    c: Horizontal(g4)
    c: Horizontal(g6)
    c: Vertical(g5)
    c: Vertical(g7)
    c: Coincident(g8,g9)
    c: Coincident(g10,g8)
    c: Horizontal(g8)
    c: Vertical(g9)
    c: Vertical(g10)
    c: Coincident(g10,g0)
    c: Coincident(g9,g0)
    c: DistanceY(g9) = -1
    c: Symmetric(g4,g2,g-1)
    c: Symmetric(g8,g6,g-1)
    c: Symmetric(g1,g4,g-1)
FEATURE [PartDesign::Pocket] Pocket024  label="top-cutout-1"
  Length = 5
  Length2 = 100
  Placement = pos=(0,0,0) rot=(1,0,0;1.5708rad)
  Profile = -> Sketch034
  Type = 1
FEATURE [Part::Box] Box003
  AttacherType = Attacher::AttachEngine3D
  Height = 4
  Length = 5
  Placement = pos=(0,-0.5,0) rot=(0,0,1;0rad)
  Width = 17.5
FEATURE [Part::Box] Box008
  AttacherType = Attacher::AttachEngine3D
  Height = 10
  Length = 8
  Placement = pos=(15.35,3.4,3.5) rot=(0,0,1;0rad)
  Width = 10
FEATURE [Part::Box] Box
  AttacherType = Attacher::AttachEngine3D
  Height = 13
  Length = 24
  Placement = pos=(0,0.1,0) rot=(0,0,1;0rad)
  Width = 16.6
FEATURE [Part::Fillet] Fillet
  Base = -> Box
  Edges = 2 edges r=6.4: [Edge6,Edge8]
FEATURE [Part::Box] Box010
  AttacherType = Attacher::AttachEngine3D
  Height = 3
  Length = 11
  Placement = pos=(12.5,13.7,7.1) rot=(1,0,0;1.0472rad)
  Width = 3
FEATURE [Part::MultiFuse] Fusion011
  Shapes = -> [Box009,Box010,Box004,Box005,Box006,Box007,Box008]
FEATURE [Part::Cut] Cut003004
  Base = -> Box003
  Tool = -> Cylinder012026
FEATURE [Sketcher::SketchObject] Sketch036  label="top-cutout-2-sketch"
  ExternalGeometry = -> [Pocket024]
  MapMode = 5
  Placement = pos=(0,1.4e-15,6.25) rot=(0,0,1;3.14159rad)
  Support = -> [Pocket024]
  sketch-geometry (4):
    g0: LineSegment StartX=7.15 StartY=5 StartZ=0 EndX=-2.85 EndY=5 EndZ=0
    g1: LineSegment StartX=-2.85 StartY=5 StartZ=0 EndX=-2.85 EndY=-5 EndZ=0
    g2: LineSegment StartX=-2.85 StartY=-5 StartZ=0 EndX=7.15 EndY=-5 EndZ=0
    g3: LineSegment StartX=7.15 StartY=-5 StartZ=0 EndX=7.15 EndY=5 EndZ=0
  constraints (12):
    c: Coincident(g0,g1)
    c: Coincident(g1,g2)
    c: Coincident(g2,g3)
    c: Coincident(g3,g0)
    c: Horizontal(g0)
    c: Horizontal(g2)
    c: Vertical(g1)
    c: Vertical(g3)
    c: Symmetric(g0,g2,g-1)
    c: DistanceY(g-3,g0) = -1.5
    c: DistanceX(g0,g-3) = -3.6
    c: DistanceX(g2) = 10
FEATURE [PartDesign::Pocket] Pocket025  label="top-cutout-2"
  Length = 5
  Length2 = 100
  Placement = pos=(0,0,0) rot=(1,0,0;1.5708rad)
  Profile = -> Sketch036
  Type = 1
FEATURE [Sketcher::SketchObject] Sketch035  label="top-cutout-3-sketch"
  ExternalGeometry = -> [Pocket025]
  MapMode = 5
  Placement = pos=(0,1.4e-15,6.25) rot=(0,0,1;3.14159rad)
  Support = -> [Pocket025]
  sketch-geometry (4):
    g0: LineSegment StartX=-23.35 StartY=6.5 StartZ=0 EndX=-10.35 EndY=6.5 EndZ=0
    g1: LineSegment StartX=-10.35 StartY=6.5 StartZ=0 EndX=-10.35 EndY=-6.5 EndZ=0
    g2: LineSegment StartX=-10.35 StartY=-6.5 StartZ=0 EndX=-23.35 EndY=-6.5 EndZ=0
    g3: LineSegment StartX=-23.35 StartY=-6.5 StartZ=0 EndX=-23.35 EndY=6.5 EndZ=0
  constraints (12):
    c: Coincident(g0,g1)
    c: Coincident(g1,g2)
    c: Coincident(g2,g3)
    c: Coincident(g3,g0)
    c: Horizontal(g0)
    c: Horizontal(g2)
    c: Vertical(g1)
    c: Vertical(g3)
    c: Symmetric(g0,g2,g-1)
    c: DistanceX(g0,g-3) = 3.9
    c: DistanceY(g0,g-3) = 1.5
    c: DistanceX(g2) = -13
FEATURE [PartDesign::Pocket] Pocket026  label="top-cutout-3"
  Length = 5
  Length2 = 100
  Placement = pos=(0,0,0) rot=(1,0,0;1.5708rad)
  Profile = -> Sketch035
  Type = 1
FEATURE [Sketcher::SketchObject] Sketch033  label="male-shaft-1-sketch"
  MapMode = 5
  Placement = pos=(0,-6.5,4.4e-15) rot=(1,0,0;1.5708rad)
  Support = -> [Pocket026]
  sketch-geometry (1):
    g0: Circle CenterX=0 CenterY=0 CenterZ=0 NormalX=0 NormalY=0 NormalZ=1 AngleXU=0 Radius=2.25
  constraints (2):
    c: Coincident(g0,g-1)
    c: Radius(g0) = 2.25
FEATURE [PartDesign::Pad] Pad001006  label="male-shaft-1"
  Length = 1.5
  Length2 = 100
  Placement = pos=(0,0,0) rot=(1,0,0;1.5708rad)
  Profile = -> Sketch033
  Type = 0
FEATURE [Sketcher::SketchObject] Sketch032  label="male-shaft-2-sketch"
  MapMode = 5
  Placement = pos=(0,6.5,-4.4e-15) rot=(-1,0,0;1.5708rad)
  Support = -> [Pad001006]
  sketch-geometry (1):
    g0: Circle CenterX=0 CenterY=0 CenterZ=0 NormalX=0 NormalY=0 NormalZ=1 AngleXU=0 Radius=2.25
  constraints (2):
    c: Coincident(g0,g-1)
    c: Radius(g0) = 2.25
FEATURE [PartDesign::Pad] Pad001004  label="male-shaft-2"
  Length = 1.5
  Length2 = 100
  Placement = pos=(0,0,0) rot=(1,0,0;1.5708rad)
  Profile = -> Sketch032
  Type = 0
FEATURE [Sketcher::SketchObject] Sketch006  label="female-shaft-sketch"
  MapMode = 5
  Placement = pos=(0,8,-1.8e-15) rot=(-1,0,0;1.5708rad)
  Support = -> [Pad001004]
  sketch-geometry (1):
    g0: Circle CenterX=13 CenterY=0 CenterZ=0 NormalX=0 NormalY=0 NormalZ=1 AngleXU=0 Radius=2.325
  constraints (3):
    c: PointOnObject(g0,g-1)
    c: DistanceX(g-1,g0) = 13
    c: Radius(g0) = 2.325
FEATURE [PartDesign::Pocket] Pocket023  label="female-shaft"
  Length = 5
  Length2 = 100
  Placement = pos=(0,0,0) rot=(1,0,0;1.5708rad)
  Profile = -> Sketch006
  Type = 1
FEATURE [Sketcher::SketchObject] Sketch030  label="inner-cutout-1-sketch"
  ExternalGeometry = -> [Pocket023]
  MapMode = 5
  Placement = pos=(10.35,0,0) rot=(0.707107,0,0.707107;3.14159rad)
  Support = -> [Pocket023]
  sketch-geometry (4):
    g0: LineSegment StartX=-5.15 StartY=5 StartZ=0 EndX=5.15 EndY=5 EndZ=0
    g1: LineSegment StartX=5.15 StartY=5 StartZ=0 EndX=5.15 EndY=-5 EndZ=0
    g2: LineSegment StartX=5.15 StartY=-5 StartZ=0 EndX=-5.15 EndY=-5 EndZ=0
    g3: LineSegment StartX=-5.15 StartY=-5 StartZ=0 EndX=-5.15 EndY=5 EndZ=0
  constraints (11):
    c: Coincident(g0,g1)
    c: Coincident(g1,g2)
    c: Coincident(g2,g3)
    c: Coincident(g3,g0)
    c: Horizontal(g0)
    c: Horizontal(g2)
    c: Vertical(g1)
    c: Vertical(g3)
    c: Symmetric(g0,g1,g-1)
    c: DistanceX(g0,g-3) = 1.1
    c: DistanceY(g0,g-3) = 1.5
FEATURE [PartDesign::Pocket] Pocket022  label="inner-cutout-1"
  Length = 5
  Length2 = 100
  Placement = pos=(0,0,0) rot=(1,0,0;1.5708rad)
  Profile = -> Sketch030
  Type = 1
FEATURE [Part::Cut] Cut003003  label="cable-chain-link"
  Base = -> Pocket022
  Tool = -> Pad001005
FEATURE [Part::Box] Box001
  AttacherType = Attacher::AttachEngine3D
  Height = 4
  Length = 7
  Placement = pos=(3.2,-1,9.9) rot=(0,0,1;0rad)
  Width = 18
FEATURE [Part::MultiFuse] Fusion010
  Shapes = -> [Box002,Box001,Cylinder012025,Cylinder012023,Cylinder012022]
FEATURE [Part::MultiFuse] Fusion012
  Shapes = -> [Fusion010,Cut003004]
FEATURE [Part::Cut] Cut003005
  Base = -> Fillet
  Tool = -> Fusion012
FEATURE [Part::MultiFuse] Fusion013
  Shapes = -> [Cut003005,Cylinder012024]
FEATURE [Part::Cut] Cut002007  label="pieza"
  Base = -> Fusion013
  Placement = pos=(-4.5,-8,-6.5) rot=(0,0,1;0rad)
  Tool = -> Fusion011
FEATURE [App::Part] Part007  label="cable-chain-link-25_5x16x12_5mm"
  Group = -> [Fillet,Cylinder012022,Cylinder012023,Box007,Cylinder012024,Box009,Fusion010,Box006,Fusion011,Box004,Cylinder012025,Box005,Cylinder012026,Box002,Box003,Fusion012,Box008,Box,Box010,Cut003004,Box001,Fusion013,Cut003005,Cut002007,Pocket022,Pad001004,Pad001005,Pad001006,Sketch029,Sketch030,Pocket023,Pad001007,Sketch031,Pocket024,Sketch032,Sketch033,Sketch034,Pocket025,Sketch035,Sketch006,Pocket026,+4 more]
  License = CC BY 3.0
  LicenseURL = http://creativecommons.org/licenses/by/3.0/
  Origin = -> Origin007
  Placement = pos=(0,35,500) rot=(0,0,1;0rad)
FEATURE [Part::Feature] Pocket021001  label="Pocket029"
  Placement = pos=(267,0,0) rot=(1,0,0;1.5708rad)
  shape: bbox 20 x 445 x 20 mm, 94 faces (baked)
FEATURE [Part::Feature] Pocket021002  label="Pocket030"
  Placement = pos=(0,0,316) rot=(1,0,0;1.5708rad)
  shape: bbox 20 x 445 x 20 mm, 94 faces (baked)
FEATURE [Part::Feature] Pocket021003  label="Pocket031"
  Placement = pos=(267,0,316) rot=(1,0,0;1.5708rad)
  shape: bbox 20 x 445 x 20 mm, 94 faces (baked)
FEATURE [App::Part] Part005  label="T-Slot_2020-6-001"
  Group = -> [Sketch025,Pocket020,Sketch026,Pad001003,Sketch027,PolarPattern001,Pocket021,Pocket021001,Pocket021002,Pocket021003]
  License = CC BY 3.0
  LicenseURL = http://creativecommons.org/licenses/by/3.0/
  Origin = -> Origin005
  Placement = pos=(0,0,-0.5) rot=(1,0,0;-1.5708rad)
FEATURE [Sketcher::SketchObject] Sketch043
  MapMode = 5
  Placement = pos=(0,0,0) rot=(1,0,0;1.5708rad)
  sketch-geometry (8):
    g0: LineSegment StartX=-9 StartY=10 StartZ=0 EndX=9 EndY=10 EndZ=0
    g1: LineSegment StartX=10 StartY=9 StartZ=0 EndX=10 EndY=-9 EndZ=0
    g2: LineSegment StartX=9 StartY=-10 StartZ=0 EndX=-9 EndY=-10 EndZ=0
    g3: LineSegment StartX=-10 StartY=-9 StartZ=0 EndX=-10 EndY=9 EndZ=0
    g4: ArcOfCircle CenterX=-9 CenterY=9 CenterZ=0 NormalX=0 NormalY=0 NormalZ=1 AngleXU=0 Radius=1 StartAngle=1.5708 EndAngle=3.14159
    g5: ArcOfCircle CenterX=-9 CenterY=-9 CenterZ=0 NormalX=0 NormalY=0 NormalZ=1 AngleXU=0 Radius=1 StartAngle=3.14159 EndAngle=4.71239
    g6: ArcOfCircle CenterX=9 CenterY=-9 CenterZ=0 NormalX=0 NormalY=0 NormalZ=1 AngleXU=0 Radius=1 StartAngle=4.71239 EndAngle=6.28319
    g7: ArcOfCircle CenterX=9 CenterY=9 CenterZ=0 NormalX=0 NormalY=0 NormalZ=1 AngleXU=0 Radius=1 StartAngle=0 EndAngle=1.5708
  constraints (20):
    c: Horizontal(g0)
    c: Horizontal(g2)
    c: Vertical(g1)
    c: Vertical(g3)
    c: Tangent(g0,g4) = 1.5708
    c: Tangent(g3,g4) = 1.5708
    c: Tangent(g3,g5) = 1.5708
    c: Tangent(g2,g5) = 1.5708
    c: Tangent(g2,g6) = 1.5708
    c: Tangent(g1,g6) = 1.5708
    c: Tangent(g0,g7) = 1.5708
    c: Tangent(g1,g7) = 1.5708
    c: Equal(g7,g4)
    c: Equal(g4,g5)
    c: Equal(g5,g6)
    c: Radius(g7) = 1
    c: DistanceX(g1,g3) = -20
    c: DistanceX(g-1,g1) = 10
    c: DistanceY(g0,g2) = -20
    c: DistanceY(g-1,g0) = 10
FEATURE [PartDesign::Pad] Pad001008
  Length = 296
  Length2 = 100
  Placement = pos=(0,0,0) rot=(1,0,0;1.5708rad)
  Profile = -> Sketch043
  Type = 0
FEATURE [Sketcher::SketchObject] Sketch042
  MapMode = 5
  Placement = pos=(0,-296,6.51e-14) rot=(1,0,0;1.5708rad)
  Support = -> [Pad001008]
  sketch-geometry (17):
    g0: LineSegment StartX=-3.4 StartY=10 StartZ=0 EndX=-3.4 EndY=9.6 EndZ=0
    g1: LineSegment StartX=-3.4 StartY=9.6 StartZ=0 EndX=-3 EndY=9.6 EndZ=0
    g2: LineSegment StartX=-3 StartY=9.6 StartZ=0 EndX=-3 EndY=8.5 EndZ=0
    g3: LineSegment StartX=-3 StartY=8.5 StartZ=0 EndX=-6 EndY=8.5 EndZ=0
    g4: LineSegment StartX=-6 StartY=8.5 StartZ=0 EndX=-6 EndY=7 EndZ=0
    g5: LineSegment StartX=-6 StartY=7 StartZ=0 EndX=-3.35 EndY=4.7 EndZ=0
    g6: LineSegment StartX=-3.35 StartY=4.7 StartZ=0 EndX=-0.65 EndY=4.7 EndZ=0
    g7: LineSegment StartX=-0.65 StartY=4.7 StartZ=0 EndX=0 EndY=4.3 EndZ=0
    g8: LineSegment StartX=0 StartY=4.3 StartZ=0 EndX=0.65 EndY=4.7 EndZ=0
    g9: LineSegment StartX=0.65 StartY=4.7 StartZ=0 EndX=3.35 EndY=4.7 EndZ=0
    g10: LineSegment StartX=3.35 StartY=4.7 StartZ=0 EndX=6 EndY=7 EndZ=0
    g11: LineSegment StartX=6 StartY=7 StartZ=0 EndX=6 EndY=8.5 EndZ=0
    g12: LineSegment StartX=6 StartY=8.5 StartZ=0 EndX=3 EndY=8.5 EndZ=0
    g13: LineSegment StartX=3 StartY=8.5 StartZ=0 EndX=3 EndY=9.6 EndZ=0
    g14: LineSegment StartX=3 StartY=9.6 StartZ=0 EndX=3.4 EndY=9.6 EndZ=0
    g15: LineSegment StartX=3.4 StartY=9.6 StartZ=0 EndX=3.4 EndY=10 EndZ=0
    g16: LineSegment StartX=3.4 StartY=10 StartZ=0 EndX=-3.4 EndY=10 EndZ=0
  constraints (51):
    c: Coincident(g0,g1)
    c: Horizontal(g1)
    c: Coincident(g1,g2)
    c: Vertical(g2)
    c: Coincident(g2,g3)
    c: Horizontal(g3)
    c: Coincident(g3,g4)
    c: Vertical(g4)
    c: Coincident(g4,g5)
    c: Coincident(g5,g6)
    c: Horizontal(g6)
    c: Coincident(g6,g7)
    c: Coincident(g7,g8)
    c: Coincident(g8,g9)
    c: Horizontal(g9)
    c: Coincident(g9,g10)
    c: Coincident(g10,g11)
    c: Coincident(g11,g12)
    c: Horizontal(g12)
    c: Coincident(g12,g13)
    c: Vertical(g13)
    c: Coincident(g13,g14)
    c: Horizontal(g14)
    c: Coincident(g14,g15)
    c: Vertical(g15)
    c: Coincident(g15,g16)
    c: Horizontal(g16)
    c: Vertical(g0)
    c: PointOnObject(g7,g-2)
    c: Coincident(g0,g16)
    c: DistanceX(g2,g12) = 6
    c: DistanceX(g-1,g12) = 3
    c: Vertical(g11)
    c: DistanceY(g4) = -1.5
    c: DistanceY(g11) = 1.5
    c: DistanceY(g13) = 1.1
    c: DistanceY(g2) = -1.1
    c: DistanceY(g15) = 0.4
    c: DistanceY(g0) = -0.4
    c: DistanceY(g-1,g15) = 10
    c: DistanceX(g1) = 0.4
    c: DistanceX(g14) = 0.4
    c: DistanceX(g3) = -3
    c: DistanceX(g12) = -3
    c: DistanceX(g6) = 2.7
    c: DistanceX(g9) = 2.7
    c: DistanceX(g6,g8) = 1.3
    c: DistanceX(g-1,g6) = -0.65
    c: DistanceY(g8) = 0.4
    c: DistanceY(g7) = -0.4
    c: DistanceY(g15,g9) = -5.3
FEATURE [PartDesign::Pocket] Pocket021004
  Length = 296
  Length2 = 100
  Placement = pos=(0,0,0) rot=(1,0,0;1.5708rad)
  Profile = -> Sketch042
  Type = 0
FEATURE [PartDesign::PolarPattern] PolarPattern002
  Angle = 360
  Axis = -> Sketch042 [N_Axis]
  Occurrences = 4
  Originals = -> [Pocket021004]
  Placement = pos=(0,0,0) rot=(1,0,0;1.5708rad)
FEATURE [Sketcher::SketchObject] Sketch041
  MapMode = 5
  Placement = pos=(0,-296,6.51e-14) rot=(1,0,0;1.5708rad)
  Support = -> [PolarPattern002]
  sketch-geometry (20):
    g0: ArcOfCircle CenterX=0 CenterY=0 CenterZ=0 NormalX=0 NormalY=0 NormalZ=1 AngleXU=0 Radius=2.75 StartAngle=1.06162 EndAngle=2.07997
    g1: ArcOfCircle CenterX=0 CenterY=0 CenterZ=0 NormalX=0 NormalY=0 NormalZ=1 AngleXU=0 Radius=2.75 StartAngle=2.63242 EndAngle=3.65076
    g2: ArcOfCircle CenterX=0 CenterY=0 CenterZ=0 NormalX=0 NormalY=0 NormalZ=1 AngleXU=0 Radius=2.75 StartAngle=4.20322 EndAngle=5.22156
    g3: ArcOfCircle CenterX=0 CenterY=0 CenterZ=0 NormalX=0 NormalY=0 NormalZ=1 AngleXU=0 Radius=2.75 StartAngle=5.77401 EndAngle=6.79236
    g4: LineSegment StartX=-2.40116 StartY=1.3405 StartZ=0 EndX=-3.0052 EndY=1.94454 EndZ=0
    g5: LineSegment StartX=-3.0052 StartY=1.94454 StartZ=0 EndX=-1.94454 EndY=3.0052 EndZ=0
    g6: LineSegment StartX=-1.94454 StartY=3.0052 StartZ=0 EndX=-1.3405 EndY=2.40116 EndZ=0
    g7: LineSegment [constr] StartX=-2.47487 StartY=2.47487 StartZ=0 EndX=0 EndY=0 EndZ=0
    g8: LineSegment [constr] StartX=0 StartY=0 StartZ=0 EndX=-2.47487 EndY=-2.47487 EndZ=0
    g9: LineSegment [constr] StartX=0 StartY=0 StartZ=0 EndX=2.47487 EndY=-2.47487 EndZ=0
    g10: LineSegment [constr] StartX=0 StartY=0 StartZ=0 EndX=2.47487 EndY=2.47487 EndZ=0
    g11: LineSegment StartX=2.40116 StartY=1.3405 StartZ=0 EndX=3.0052 EndY=1.94454 EndZ=0
    g12: LineSegment StartX=3.0052 StartY=1.94454 StartZ=0 EndX=1.94454 EndY=3.0052 EndZ=0
    g13: LineSegment StartX=1.94454 StartY=3.0052 StartZ=0 EndX=1.3405 EndY=2.40116 EndZ=0
    g14: LineSegment StartX=2.40116 StartY=-1.3405 StartZ=0 EndX=3.0052 EndY=-1.94454 EndZ=0
    g15: LineSegment StartX=3.0052 StartY=-1.94454 StartZ=0 EndX=1.94454 EndY=-3.0052 EndZ=0
    g16: LineSegment StartX=1.94454 StartY=-3.0052 StartZ=0 EndX=1.3405 EndY=-2.40116 EndZ=0
    g17: LineSegment StartX=-1.3405 StartY=-2.40116 StartZ=0 EndX=-1.94454 EndY=-3.0052 EndZ=0
    g18: LineSegment StartX=-1.94454 StartY=-3.0052 StartZ=0 EndX=-3.0052 EndY=-1.94454 EndZ=0
    g19: LineSegment StartX=-3.0052 StartY=-1.94454 StartZ=0 EndX=-2.40116 EndY=-1.3405 EndZ=0
  constraints (60):
    c: Coincident(g3,g-1)
    c: Coincident(g0,g-1)
    c: Coincident(g1,g-1)
    c: Coincident(g2,g-1)
    c: Equal(g0,g3)
    c: Equal(g3,g2)
    c: Equal(g2,g1)
    c: Radius(g0) = 2.75
    c: Coincident(g4,g5)
    c: Coincident(g5,g6)
    c: Perpendicular(g5,g6) = 4.71239
    c: Perpendicular(g4,g5) = 4.71239
    c: Coincident(g0,g6)
    c: Coincident(g1,g4)
    c: Coincident(g7,g-1)
    c: Angle(g-2,g7) = 0.785398
    c: PointOnObject(g7,g5)
    c: Parallel(g7,g6)
    c: Coincident(g8,g-1)
    c: Angle(g7,g8) = 1.5708
    c: Coincident(g9,g-1)
    c: Angle(g8,g9) = 1.5708
    c: Coincident(g10,g-1)
    c: Angle(g9,g10) = 1.5708
    c: Coincident(g11,g12)
    c: Coincident(g12,g13)
    c: Perpendicular(g12,g13) = 1.5708
    c: Perpendicular(g11,g12) = 1.5708
    c: Parallel(g10,g13)
    c: PointOnObject(g10,g12)
    c: Equal(g7,g10)
    c: Equal(g10,g8)
    c: Equal(g8,g9)
    c: Distance(g7) = 3.5
    c: Coincident(g0,g13)
    c: Coincident(g11,g3)
    c: Coincident(g14,g15)
    c: Coincident(g15,g16)
    c: Perpendicular(g15,g16) = 4.71239
    c: Perpendicular(g14,g15) = 4.71239
    c: Parallel(g9,g14)
    c: Coincident(g3,g14)
    c: PointOnObject(g9,g15)
    c: Coincident(g16,g2)
    c: Coincident(g17,g18)
    c: Coincident(g18,g19)
    c: Perpendicular(g18,g19) = 4.71239
    c: Perpendicular(g17,g18) = 4.71239
    c: Parallel(g8,g19)
    c: PointOnObject(g8,g18)
    c: Coincident(g19,g1)
    c: Coincident(g2,g17)
    c: Equal(g12,g5)
    c: Equal(g5,g18)
    c: Equal(g18,g15)
    c: Distance(g12) = 1.5
    c: Distance(g11,g10) = 0.75
    c: Distance(g7,g5) = 0.75
    c: Distance(g8,g17) = 0.75
    c: Distance(g9,g14) = 0.75
FEATURE [PartDesign::Pocket] Pocket021005
  Length = 296
  Length2 = 100
  Placement = pos=(0,0,0) rot=(1,0,0;1.5708rad)
  Profile = -> Sketch041
  Type = 0
FEATURE [Part::Feature] Pocket021005001  label="Pocket021006"
  Placement = pos=(0,0,425) rot=(1,0,0;1.5708rad)
  shape: bbox 20 x 296 x 20 mm, 94 faces (baked)
FEATURE [Part::Feature] Pocket021005002  label="Pocket021007"
  Placement = pos=(-267,0,425) rot=(1,0,0;1.5708rad)
  shape: bbox 20 x 296 x 20 mm, 94 faces (baked)
FEATURE [Part::Feature] Pocket021005003  label="Pocket021008"
  Placement = pos=(-267,0,47) rot=(1,0,0;1.5708rad)
  shape: bbox 20 x 296 x 20 mm, 94 faces (baked)
FEATURE [App::Part] Part009  label="T-Slot_2020-6-002"
  Group = -> [Sketch043,Pocket021004,Sketch041,Pad001008,Sketch042,PolarPattern002,Pocket021005,Pocket021005001,Pocket021005002,Pocket021005003]
  License = CC BY 3.0
  LicenseURL = http://creativecommons.org/licenses/by/3.0/
  Origin = -> Origin009
  Placement = pos=(0,10,15) rot=(0,0,1;-3.14159rad)
FEATURE [Sketcher::SketchObject] Sketch046
  MapMode = 5
  Placement = pos=(0,0,0) rot=(1,0,0;1.5708rad)
  sketch-geometry (8):
    g0: LineSegment StartX=-9 StartY=10 StartZ=0 EndX=9 EndY=10 EndZ=0
    g1: LineSegment StartX=10 StartY=9 StartZ=0 EndX=10 EndY=-9 EndZ=0
    g2: LineSegment StartX=9 StartY=-10 StartZ=0 EndX=-9 EndY=-10 EndZ=0
    g3: LineSegment StartX=-10 StartY=-9 StartZ=0 EndX=-10 EndY=9 EndZ=0
    g4: ArcOfCircle CenterX=-9 CenterY=9 CenterZ=0 NormalX=0 NormalY=0 NormalZ=1 AngleXU=0 Radius=1 StartAngle=1.5708 EndAngle=3.14159
    g5: ArcOfCircle CenterX=-9 CenterY=-9 CenterZ=0 NormalX=0 NormalY=0 NormalZ=1 AngleXU=0 Radius=1 StartAngle=3.14159 EndAngle=4.71239
    g6: ArcOfCircle CenterX=9 CenterY=-9 CenterZ=0 NormalX=0 NormalY=0 NormalZ=1 AngleXU=0 Radius=1 StartAngle=4.71239 EndAngle=6.28319
    g7: ArcOfCircle CenterX=9 CenterY=9 CenterZ=0 NormalX=0 NormalY=0 NormalZ=1 AngleXU=0 Radius=1 StartAngle=0 EndAngle=1.5708
  constraints (20):
    c: Horizontal(g0)
    c: Horizontal(g2)
    c: Vertical(g1)
    c: Vertical(g3)
    c: Tangent(g0,g4) = 1.5708
    c: Tangent(g3,g4) = 1.5708
    c: Tangent(g3,g5) = 1.5708
    c: Tangent(g2,g5) = 1.5708
    c: Tangent(g2,g6) = 1.5708
    c: Tangent(g1,g6) = 1.5708
    c: Tangent(g0,g7) = 1.5708
    c: Tangent(g1,g7) = 1.5708
    c: Equal(g7,g4)
    c: Equal(g4,g5)
    c: Equal(g5,g6)
    c: Radius(g7) = 1
    c: DistanceX(g1,g3) = -20
    c: DistanceX(g-1,g1) = 10
    c: DistanceY(g0,g2) = -20
    c: DistanceY(g-1,g0) = 10
FEATURE [PartDesign::Pad] Pad001009
  Length = 247
  Length2 = 100
  Placement = pos=(0,0,0) rot=(1,0,0;1.5708rad)
  Profile = -> Sketch046
  Type = 0
FEATURE [Sketcher::SketchObject] Sketch045
  MapMode = 5
  Placement = pos=(0,-247,5.43e-14) rot=(1,0,0;1.5708rad)
  Support = -> [Pad001009]
  sketch-geometry (17):
    g0: LineSegment StartX=-3.4 StartY=10 StartZ=0 EndX=-3.4 EndY=9.6 EndZ=0
    g1: LineSegment StartX=-3.4 StartY=9.6 StartZ=0 EndX=-3 EndY=9.6 EndZ=0
    g2: LineSegment StartX=-3 StartY=9.6 StartZ=0 EndX=-3 EndY=8.5 EndZ=0
    g3: LineSegment StartX=-3 StartY=8.5 StartZ=0 EndX=-6 EndY=8.5 EndZ=0
    g4: LineSegment StartX=-6 StartY=8.5 StartZ=0 EndX=-6 EndY=7 EndZ=0
    g5: LineSegment StartX=-6 StartY=7 StartZ=0 EndX=-3.35 EndY=4.7 EndZ=0
    g6: LineSegment StartX=-3.35 StartY=4.7 StartZ=0 EndX=-0.65 EndY=4.7 EndZ=0
    g7: LineSegment StartX=-0.65 StartY=4.7 StartZ=0 EndX=0 EndY=4.3 EndZ=0
    g8: LineSegment StartX=0 StartY=4.3 StartZ=0 EndX=0.65 EndY=4.7 EndZ=0
    g9: LineSegment StartX=0.65 StartY=4.7 StartZ=0 EndX=3.35 EndY=4.7 EndZ=0
    g10: LineSegment StartX=3.35 StartY=4.7 StartZ=0 EndX=6 EndY=7 EndZ=0
    g11: LineSegment StartX=6 StartY=7 StartZ=0 EndX=6 EndY=8.5 EndZ=0
    g12: LineSegment StartX=6 StartY=8.5 StartZ=0 EndX=3 EndY=8.5 EndZ=0
    g13: LineSegment StartX=3 StartY=8.5 StartZ=0 EndX=3 EndY=9.6 EndZ=0
    g14: LineSegment StartX=3 StartY=9.6 StartZ=0 EndX=3.4 EndY=9.6 EndZ=0
    g15: LineSegment StartX=3.4 StartY=9.6 StartZ=0 EndX=3.4 EndY=10 EndZ=0
    g16: LineSegment StartX=3.4 StartY=10 StartZ=0 EndX=-3.4 EndY=10 EndZ=0
  constraints (51):
    c: Coincident(g0,g1)
    c: Horizontal(g1)
    c: Coincident(g1,g2)
    c: Vertical(g2)
    c: Coincident(g2,g3)
    c: Horizontal(g3)
    c: Coincident(g3,g4)
    c: Vertical(g4)
    c: Coincident(g4,g5)
    c: Coincident(g5,g6)
    c: Horizontal(g6)
    c: Coincident(g6,g7)
    c: Coincident(g7,g8)
    c: Coincident(g8,g9)
    c: Horizontal(g9)
    c: Coincident(g9,g10)
    c: Coincident(g10,g11)
    c: Coincident(g11,g12)
    c: Horizontal(g12)
    c: Coincident(g12,g13)
    c: Vertical(g13)
    c: Coincident(g13,g14)
    c: Horizontal(g14)
    c: Coincident(g14,g15)
    c: Vertical(g15)
    c: Coincident(g15,g16)
    c: Horizontal(g16)
    c: Vertical(g0)
    c: PointOnObject(g7,g-2)
    c: Coincident(g0,g16)
    c: DistanceX(g2,g12) = 6
    c: DistanceX(g-1,g12) = 3
    c: Vertical(g11)
    c: DistanceY(g4) = -1.5
    c: DistanceY(g11) = 1.5
    c: DistanceY(g13) = 1.1
    c: DistanceY(g2) = -1.1
    c: DistanceY(g15) = 0.4
    c: DistanceY(g0) = -0.4
    c: DistanceY(g-1,g15) = 10
    c: DistanceX(g1) = 0.4
    c: DistanceX(g14) = 0.4
    c: DistanceX(g3) = -3
    c: DistanceX(g12) = -3
    c: DistanceX(g6) = 2.7
    c: DistanceX(g9) = 2.7
    c: DistanceX(g6,g8) = 1.3
    c: DistanceX(g-1,g6) = -0.65
    c: DistanceY(g8) = 0.4
    c: DistanceY(g7) = -0.4
    c: DistanceY(g15,g9) = -5.3
FEATURE [PartDesign::Pocket] Pocket021005004
  Length = 247
  Length2 = 100
  Placement = pos=(0,0,0) rot=(1,0,0;1.5708rad)
  Profile = -> Sketch045
  Type = 0
FEATURE [PartDesign::PolarPattern] PolarPattern003
  Angle = 360
  Axis = -> Sketch045 [N_Axis]
  Occurrences = 4
  Originals = -> [Pocket021005004]
  Placement = pos=(0,0,0) rot=(1,0,0;1.5708rad)
FEATURE [Sketcher::SketchObject] Sketch044
  MapMode = 5
  Placement = pos=(0,-247,5.43e-14) rot=(1,0,0;1.5708rad)
  Support = -> [PolarPattern003]
  sketch-geometry (20):
    g0: ArcOfCircle CenterX=0 CenterY=0 CenterZ=0 NormalX=0 NormalY=0 NormalZ=1 AngleXU=0 Radius=2.75 StartAngle=1.06162 EndAngle=2.07997
    g1: ArcOfCircle CenterX=0 CenterY=0 CenterZ=0 NormalX=0 NormalY=0 NormalZ=1 AngleXU=0 Radius=2.75 StartAngle=2.63242 EndAngle=3.65076
    g2: ArcOfCircle CenterX=0 CenterY=0 CenterZ=0 NormalX=0 NormalY=0 NormalZ=1 AngleXU=0 Radius=2.75 StartAngle=4.20322 EndAngle=5.22156
    g3: ArcOfCircle CenterX=0 CenterY=0 CenterZ=0 NormalX=0 NormalY=0 NormalZ=1 AngleXU=0 Radius=2.75 StartAngle=5.77401 EndAngle=6.79236
    g4: LineSegment StartX=-2.40116 StartY=1.3405 StartZ=0 EndX=-3.0052 EndY=1.94454 EndZ=0
    g5: LineSegment StartX=-3.0052 StartY=1.94454 StartZ=0 EndX=-1.94454 EndY=3.0052 EndZ=0
    g6: LineSegment StartX=-1.94454 StartY=3.0052 StartZ=0 EndX=-1.3405 EndY=2.40116 EndZ=0
    g7: LineSegment [constr] StartX=-2.47487 StartY=2.47487 StartZ=0 EndX=0 EndY=0 EndZ=0
    g8: LineSegment [constr] StartX=0 StartY=0 StartZ=0 EndX=-2.47487 EndY=-2.47487 EndZ=0
    g9: LineSegment [constr] StartX=0 StartY=0 StartZ=0 EndX=2.47487 EndY=-2.47487 EndZ=0
    g10: LineSegment [constr] StartX=0 StartY=0 StartZ=0 EndX=2.47487 EndY=2.47487 EndZ=0
    g11: LineSegment StartX=2.40116 StartY=1.3405 StartZ=0 EndX=3.0052 EndY=1.94454 EndZ=0
    g12: LineSegment StartX=3.0052 StartY=1.94454 StartZ=0 EndX=1.94454 EndY=3.0052 EndZ=0
    g13: LineSegment StartX=1.94454 StartY=3.0052 StartZ=0 EndX=1.3405 EndY=2.40116 EndZ=0
    g14: LineSegment StartX=2.40116 StartY=-1.3405 StartZ=0 EndX=3.0052 EndY=-1.94454 EndZ=0
    g15: LineSegment StartX=3.0052 StartY=-1.94454 StartZ=0 EndX=1.94454 EndY=-3.0052 EndZ=0
    g16: LineSegment StartX=1.94454 StartY=-3.0052 StartZ=0 EndX=1.3405 EndY=-2.40116 EndZ=0
    g17: LineSegment StartX=-1.3405 StartY=-2.40116 StartZ=0 EndX=-1.94454 EndY=-3.0052 EndZ=0
    g18: LineSegment StartX=-1.94454 StartY=-3.0052 StartZ=0 EndX=-3.0052 EndY=-1.94454 EndZ=0
    g19: LineSegment StartX=-3.0052 StartY=-1.94454 StartZ=0 EndX=-2.40116 EndY=-1.3405 EndZ=0
  constraints (60):
    c: Coincident(g3,g-1)
    c: Coincident(g0,g-1)
    c: Coincident(g1,g-1)
    c: Coincident(g2,g-1)
    c: Equal(g0,g3)
    c: Equal(g3,g2)
    c: Equal(g2,g1)
    c: Radius(g0) = 2.75
    c: Coincident(g4,g5)
    c: Coincident(g5,g6)
    c: Perpendicular(g5,g6) = 4.71239
    c: Perpendicular(g4,g5) = 4.71239
    c: Coincident(g0,g6)
    c: Coincident(g1,g4)
    c: Coincident(g7,g-1)
    c: Angle(g-2,g7) = 0.785398
    c: PointOnObject(g7,g5)
    c: Parallel(g7,g6)
    c: Coincident(g8,g-1)
    c: Angle(g7,g8) = 1.5708
    c: Coincident(g9,g-1)
    c: Angle(g8,g9) = 1.5708
    c: Coincident(g10,g-1)
    c: Angle(g9,g10) = 1.5708
    c: Coincident(g11,g12)
    c: Coincident(g12,g13)
    c: Perpendicular(g12,g13) = 1.5708
    c: Perpendicular(g11,g12) = 1.5708
    c: Parallel(g10,g13)
    c: PointOnObject(g10,g12)
    c: Equal(g7,g10)
    c: Equal(g10,g8)
    c: Equal(g8,g9)
    c: Distance(g7) = 3.5
    c: Coincident(g0,g13)
    c: Coincident(g11,g3)
    c: Coincident(g14,g15)
    c: Coincident(g15,g16)
    c: Perpendicular(g15,g16) = 4.71239
    c: Perpendicular(g14,g15) = 4.71239
    c: Parallel(g9,g14)
    c: Coincident(g3,g14)
    c: PointOnObject(g9,g15)
    c: Coincident(g16,g2)
    c: Coincident(g17,g18)
    c: Coincident(g18,g19)
    c: Perpendicular(g18,g19) = 4.71239
    c: Perpendicular(g17,g18) = 4.71239
    c: Parallel(g8,g19)
    c: PointOnObject(g8,g18)
    c: Coincident(g19,g1)
    c: Coincident(g2,g17)
    c: Equal(g12,g5)
    c: Equal(g5,g18)
    c: Equal(g18,g15)
    c: Distance(g12) = 1.5
    c: Distance(g11,g10) = 0.75
    c: Distance(g7,g5) = 0.75
    c: Distance(g8,g17) = 0.75
    c: Distance(g9,g14) = 0.75
FEATURE [PartDesign::Pocket] Pocket021005005
  Length = 247
  Length2 = 100
  Placement = pos=(0,0,0) rot=(1,0,0;1.5708rad)
  Profile = -> Sketch044
  Type = 0
FEATURE [Part::Feature] Pocket021005005001  label="Pocket021005006"
  Placement = pos=(316,0,0) rot=(1,0,0;1.5708rad)
  shape: bbox 20 x 247 x 20 mm, 94 faces (baked)
FEATURE [Part::Feature] Pocket021005005002  label="Pocket021005007"
  Placement = pos=(316,0,425) rot=(1,0,0;1.5708rad)
  shape: bbox 20 x 247 x 20 mm, 94 faces (baked)
FEATURE [Part::Feature] Pocket021005005003  label="Pocket021005008"
  Placement = pos=(0,0,425) rot=(1,0,0;1.5708rad)
  shape: bbox 20 x 247 x 20 mm, 94 faces (baked)
FEATURE [App::Part] Part010  label="T-Slot_2020-6-003"
  Group = -> [Sketch046,Pocket021005004,Sketch044,Pad001009,Sketch045,PolarPattern003,Pocket021005005,Pocket021005005001,Pocket021005005002,Pocket021005005003]
  License = CC BY 3.0
  LicenseURL = http://creativecommons.org/licenses/by/3.0/
  Origin = -> Origin010
  Placement = pos=(10,0,15) rot=(0,0,1;1.5708rad)
FEATURE [Part::Box] Box012  label="Base_000"
  AttacherType = Attacher::AttachEngine3D
  Height = 1.6
  Length = 304
  Placement = pos=(-310,270,3) rot=(1,0,0;1.5708rad)
  Width = 50
FEATURE [Part::Box] Box013  label="Cube002"
  AttacherType = Attacher::AttachEngine3D
  Height = 2
  Length = 13.5
  Placement = pos=(-37.4,270.2,11) rot=(1,0,0;1.5708rad)
  Width = 12.5
FEATURE [Sketcher::SketchObject] Sketch047  label="pololu-pcb-main-sketch"
  MapMode = 5
  sketch-geometry (4):
    g0: LineSegment StartX=-10.16 StartY=7.62 StartZ=0 EndX=10.16 EndY=7.62 EndZ=0
    g1: LineSegment StartX=10.16 StartY=7.62 StartZ=0 EndX=10.16 EndY=-7.62 EndZ=0
    g2: LineSegment StartX=10.16 StartY=-7.62 StartZ=0 EndX=-10.16 EndY=-7.62 EndZ=0
    g3: LineSegment StartX=-10.16 StartY=-7.62 StartZ=0 EndX=-10.16 EndY=7.62 EndZ=0
  constraints (11):
    c: Coincident(g0,g1)
    c: Coincident(g1,g2)
    c: Coincident(g2,g3)
    c: Coincident(g3,g0)
    c: Horizontal(g0)
    c: Horizontal(g2)
    c: Vertical(g1)
    c: Vertical(g3)
    c: Symmetric(g0,g1,g-1)
    c: DistanceX(g0) = 20.32
    c: DistanceY(g3) = 15.24
FEATURE [PartDesign::Pad] Pad001010  label="pololu-pcb-main"
  Length = 1.65
  Length2 = 100
  Profile = -> Sketch047
  Type = 0
FEATURE [Sketcher::SketchObject] Sketch048  label="pololu-pcb-pad-master-sketch"
  MapMode = 5
  Placement = pos=(0,0,1.65) rot=(0,0,1;0rad)
  Support = -> [Pad001010]
  sketch-geometry (2):
    g0: Circle CenterX=-8.89 CenterY=-6.35 CenterZ=0 NormalX=0 NormalY=0 NormalZ=1 AngleXU=0 Radius=0.39
    g1: Circle CenterX=-8.89 CenterY=6.35 CenterZ=0 NormalX=0 NormalY=0 NormalZ=1 AngleXU=0 Radius=0.39
  constraints (5):
    c: Radius(g0) = 0.39
    c: Equal(g0,g1)
    c: DistanceY(g-1,g0) = -6.35
    c: DistanceX(g-1,g0) = -8.89
    c: Symmetric(g1,g0,g-1)
FEATURE [PartDesign::Pocket] Pocket021005005004  label="pololu-pcb-pad-master"
  Length = 5
  Length2 = 100
  Profile = -> Sketch048
  Type = 1
FEATURE [PartDesign::LinearPattern] LinearPattern002  label="pololu-pcb-pads"
  Direction = -> Sketch048 [H_Axis]
  Length = 17.78
  Occurrences = 8
  Originals = -> [Pocket021005005004]
FEATURE [App::DocumentObjectGroup] Group010  label="pololu-pcb-src"
  Group = -> [Pad001010,Pocket021005005004,LinearPattern002]
FEATURE [Part::Feature] LinearPattern003  label="pololu-pcb"
  shape: bbox 20.32 x 15.24 x 1.65 mm, 22 faces (baked)
FEATURE [Sketcher::SketchObject] Sketch049  label="drv-chip-sketch"
  MapMode = 5
  Placement = pos=(-1.016,-1.778,1.651) rot=(0,0,1;0rad)
  sketch-geometry (4):
    g0: LineSegment StartX=-2.54 StartY=2.54 StartZ=0 EndX=2.54 EndY=2.54 EndZ=0
    g1: LineSegment StartX=2.54 StartY=2.54 StartZ=0 EndX=2.54 EndY=-2.54 EndZ=0
    g2: LineSegment StartX=2.54 StartY=-2.54 StartZ=0 EndX=-2.54 EndY=-2.54 EndZ=0
    g3: LineSegment StartX=-2.54 StartY=-2.54 StartZ=0 EndX=-2.54 EndY=2.54 EndZ=0
  constraints (11):
    c: Coincident(g0,g1)
    c: Coincident(g1,g2)
    c: Coincident(g2,g3)
    c: Coincident(g3,g0)
    c: Horizontal(g0)
    c: Horizontal(g2)
    c: Vertical(g1)
    c: Vertical(g3)
    c: Symmetric(g0,g1,g-1)
    c: Equal(g3,g0)
    c: DistanceX(g0) = 5.08
FEATURE [PartDesign::Pad] Pad001011  label="drv-chip"
  Length = 0.89
  Length2 = 100
  Placement = pos=(-1.016,-1.778,1.651) rot=(0,0,1;0rad)
  Profile = -> Sketch049
  Type = 0
FEATURE [App::DocumentObjectGroup] Group011  label="drv-chip-src"
  Group = -> [Pad001011]
FEATURE [Part::Feature] Pad002001  label="drv-chip001"
  Placement = pos=(-1.016,-1.778,1.651) rot=(0,0,1;0rad)
  shape: bbox 5.08 x 5.08 x 0.89 mm, 6 faces (baked)
FEATURE [Sketcher::SketchObject] Sketch050  label="potentiometer-base-sketch"
  MapMode = 5
  sketch-geometry (4):
    g0: LineSegment StartX=-1.524 StartY=1.905 StartZ=0 EndX=1.524 EndY=1.905 EndZ=0
    g1: LineSegment StartX=1.524 StartY=1.905 StartZ=0 EndX=1.524 EndY=-1.905 EndZ=0
    g2: LineSegment StartX=1.524 StartY=-1.905 StartZ=0 EndX=-1.524 EndY=-1.905 EndZ=0
    g3: LineSegment StartX=-1.524 StartY=-1.905 StartZ=0 EndX=-1.524 EndY=1.905 EndZ=0
  constraints (11):
    c: Coincident(g0,g1)
    c: Coincident(g1,g2)
    c: Coincident(g2,g3)
    c: Coincident(g3,g0)
    c: Horizontal(g0)
    c: Horizontal(g2)
    c: Vertical(g1)
    c: Vertical(g3)
    c: Symmetric(g0,g1,g-1)
    c: DistanceX(g2) = -3.048
    c: DistanceY(g3) = 3.81
FEATURE [PartDesign::Pad] Pad002002  label="potentiometer-base"
  Length = 0.66
  Length2 = 100
  Profile = -> Sketch050
  Type = 0
FEATURE [Sketcher::SketchObject] Sketch051  label="potentiometer-screw-main-sketch"
  MapMode = 5
  Placement = pos=(0,0,0.66) rot=(0,0,1;0rad)
  sketch-geometry (1):
    g0: Circle CenterX=0 CenterY=0 CenterZ=0 NormalX=0 NormalY=0 NormalZ=1 AngleXU=0 Radius=1.5
  constraints (2):
    c: Coincident(g0,g-1)
    c: Radius(g0) = 1.5
FEATURE [PartDesign::Pad] Pad002003  label="potentiometer-screw-main"
  Length = 0.64
  Length2 = 100
  Placement = pos=(0,0,0.66) rot=(0,0,1;0rad)
  Profile = -> Sketch051
  Type = 0
FEATURE [Sketcher::SketchObject] Sketch052  label="potentiometer-screw-cross-sketch"
  MapMode = 5
  Placement = pos=(0,0,1.3) rot=(0,0,1;0rad)
  Support = -> [Pad002003]
  sketch-geometry (12):
    g0: LineSegment StartX=0.19 StartY=1.015 StartZ=0 EndX=-0.19 EndY=1.015 EndZ=0
    g1: LineSegment StartX=-0.19 StartY=1.015 StartZ=0 EndX=-0.19 EndY=0.19 EndZ=0
    g2: LineSegment StartX=-0.19 StartY=0.19 StartZ=0 EndX=-1.015 EndY=0.19 EndZ=0
    g3: LineSegment StartX=-1.015 StartY=0.19 StartZ=0 EndX=-1.015 EndY=-0.19 EndZ=0
    g4: LineSegment StartX=-1.015 StartY=-0.19 StartZ=0 EndX=-0.19 EndY=-0.19 EndZ=0
    g5: LineSegment StartX=-0.19 StartY=-0.19 StartZ=0 EndX=-0.19 EndY=-1.015 EndZ=0
    g6: LineSegment StartX=-0.19 StartY=-1.015 StartZ=0 EndX=0.19 EndY=-1.015 EndZ=0
    g7: LineSegment StartX=0.19 StartY=-1.015 StartZ=0 EndX=0.19 EndY=-0.19 EndZ=0
    g8: LineSegment StartX=0.19 StartY=-0.19 StartZ=0 EndX=1.015 EndY=-0.19 EndZ=0
    g9: LineSegment StartX=1.015 StartY=-0.19 StartZ=0 EndX=1.015 EndY=0.19 EndZ=0
    g10: LineSegment StartX=1.015 StartY=0.19 StartZ=0 EndX=0.19 EndY=0.19 EndZ=0
    g11: LineSegment StartX=0.19 StartY=0.19 StartZ=0 EndX=0.19 EndY=1.015 EndZ=0
  constraints (34):
    c: Coincident(g0,g1)
    c: Coincident(g1,g2)
    c: Coincident(g2,g3)
    c: Vertical(g1)
    c: Equal(g2,g1)
    c: Vertical(g3)
    c: Horizontal(g0)
    c: Equal(g3,g0)
    c: Symmetric(g0,g0,g-2)
    c: Symmetric(g2,g3,g-1)
    c: DistanceX(g0) = -0.38
    c: DistanceX(g2) = -0.825
    c: Coincident(g4,g5)
    c: Coincident(g5,g6)
    c: Coincident(g6,g7)
    c: Coincident(g7,g8)
    c: Coincident(g8,g9)
    c: Coincident(g9,g10)
    c: Coincident(g10,g11)
    c: Vertical(g11)
    c: Vertical(g9)
    c: Vertical(g7)
    c: Vertical(g5)
    c: Horizontal(g10)
    c: Horizontal(g8)
    c: Horizontal(g6)
    c: Horizontal(g4)
    c: Coincident(g4,g3)
    c: Coincident(g11,g0)
    c: Symmetric(g10,g1,g-2)
    c: Symmetric(g9,g2,g-2)
    c: Symmetric(g7,g4,g-2)
    c: Symmetric(g1,g4,g-1)
    c: Symmetric(g6,g0,g-1)
FEATURE [PartDesign::Pocket] Pocket021005005005  label="potentiometer-screw-cross"
  Length = 5
  Length2 = 100
  Placement = pos=(0,0,0.66) rot=(0,0,1;0rad)
  Profile = -> Sketch052
  Type = 1
FEATURE [Part::Feature] Pad002002001  label="potentiometer-base001"
  shape: bbox 3.048 x 3.81 x 0.66 mm, 6 faces (baked)
FEATURE [Part::Feature] Pocket001001  label="potentiometer-screw-cross001"
  Placement = pos=(0,0,0.66) rot=(0,0,1;0rad)
  shape: bbox 3 x 3 x 0.64 mm, 15 faces (baked)
FEATURE [Part::Compound] Compound063  label="pololu-potentiometer"
  Links = -> [Pad002002001,Pocket001001]
  Placement = pos=(7.62,0.889,1.651) rot=(0,0,1;0rad)
FEATURE [App::DocumentObjectGroup] Group012  label="potentiometer-src"
  Group = -> [Pad002002,Pad002003,Pocket021005005005,Compound063]
FEATURE [Part::Compound] Compound064  label="pololu-potentiometer001"
  Placement = pos=(7.62,0.889,1.651) rot=(0,0,1;0rad)
FEATURE [Part::Feature] Pad002002002  label="heat-sink-8x6x5mm001"
  Placement = pos=(-1.0165,-1.7757,2.54) rot=(0.57735,0.57735,0.57735;2.0944rad)
  shape: bbox 8 x 6.38 x 4.83 mm, 22 faces (baked)
FEATURE [Part::Compound] Compound065  label="1x8-male-pin-header005"
  Placement = pos=(-8.89,-6.35,0) rot=(1,0,0;3.14159rad)
FEATURE [Part::Compound] Compound066  label="1x8-male-pin-header006"
  Placement = pos=(-8.89,6.35,0) rot=(1,0,0;3.14159rad)
FEATURE [Part::Compound] Compound067  label="pololu-A500_001"
  Links = -> [LinearPattern003,Pad002001,Compound064,Pad002002002,Compound065,Compound066]
  Placement = pos=(-34.4,226.2,36) rot=(0,0,1;1.5708rad)
FEATURE [Part::Feature] Fusion001001  label="Motor-with-connector-final"
  Placement = pos=(11,133.5,428) rot=(0,1,0;3.14159rad)
  shape: bbox 48 x 42.3 x 60.1 mm, 110 faces (baked)
FEATURE [Sketcher::SketchObject] Sketch065
  MapMode = 5
  sketch-geometry (9):
    g0: Circle [constr] CenterX=0 CenterY=0 CenterZ=0 NormalX=0 NormalY=0 NormalZ=1 AngleXU=0 Radius=3.95
    g1: LineSegment StartX=-3.90416 StartY=0.6 StartZ=0 EndX=-3.90416 EndY=-0.6 EndZ=0
    g2: LineSegment StartX=-3.90416 StartY=0.6 StartZ=0 EndX=-0.6 EndY=3.90416 EndZ=0
    g3: LineSegment StartX=-0.6 StartY=3.90416 StartZ=0 EndX=0.6 EndY=3.90416 EndZ=0
    g4: LineSegment StartX=0.6 StartY=3.90416 StartZ=0 EndX=3.90416 EndY=0.6 EndZ=0
    g5: LineSegment StartX=3.90416 StartY=0.6 StartZ=0 EndX=3.90416 EndY=-0.6 EndZ=0
    g6: LineSegment StartX=3.90416 StartY=-0.6 StartZ=0 EndX=0.6 EndY=-3.90416 EndZ=0
    g7: LineSegment StartX=0.6 StartY=-3.90416 StartZ=0 EndX=-0.6 EndY=-3.90416 EndZ=0
    g8: LineSegment StartX=-0.6 StartY=-3.90416 StartZ=0 EndX=-3.90416 EndY=-0.6 EndZ=0
  constraints (29):
    c: Coincident(g0,g-1)
    c: Radius(g0) = 3.95
    c: PointOnObject(g1,g0)
    c: PointOnObject(g1,g0)
    c: Vertical(g1)
    c: Coincident(g2,g1)
    c: PointOnObject(g2,g0)
    c: Coincident(g3,g2)
    c: PointOnObject(g3,g0)
    c: Horizontal(g3)
    c: Coincident(g3,g4)
    c: PointOnObject(g4,g0)
    c: Coincident(g4,g5)
    c: PointOnObject(g5,g0)
    c: Vertical(g5)
    c: Coincident(g5,g6)
    c: PointOnObject(g6,g0)
    c: Coincident(g6,g7)
    c: PointOnObject(g7,g0)
    c: Horizontal(g7)
    c: Coincident(g7,g8)
    c: Coincident(g8,g1)
    c: Equal(g3,g5)
    c: Equal(g5,g7)
    c: Equal(g7,g1)
    c: Equal(g2,g4)
    c: Equal(g4,g6)
    c: Equal(g6,g8)
    c: DistanceY(g5,g5) = 1.2
FEATURE [Part::Helix] Helix001
  Angle = 0
  AttacherType = Attacher::AttachEngine3D
  Height = 335
  LocalCoord = 0
  Pitch = 8
  Radius = 2
  Style = 1
FEATURE [Part::Sweep] Sweep001
  Frenet = true
  Sections = -> [Sketch065]
  Solid = true
  Spine = -> Helix001
  Transition = 1
FEATURE [Part::Cylinder] Cylinder012029001003
  Angle = 360
  AttacherType = Attacher::AttachEngine3D
  Height = 335
  Radius = 3.3
FEATURE [Part::MultiFuse] Fusion001002
  Placement = pos=(11,0,0) rot=(0,0,1;0rad)
  Shapes = -> [Cylinder012029001003,Sweep001]
FEATURE [App::Part] Part006  label="Thread"
  Group = -> [Helix001,Sketch065,Cylinder012029001003,Sweep001,Fusion001002]
  License = CC BY 3.0
  LicenseURL = http://creativecommons.org/licenses/by/3.0/
  Origin = -> Origin006
  Placement = pos=(0,133.5,32) rot=(0,0,1;0rad)
FEATURE [Part::Feature] Compound067001  label="pololu-A500_002"
  Placement = pos=(-34.4,205.1,36) rot=(0,0,1;1.5708rad)
  shape: bbox 15.24 x 20.32 x 15.57 mm, 647 faces, 37 solids (baked)
FEATURE [Part::Feature] Compound067002  label="pololu-A500_003"
  Placement = pos=(-57.3,225.5,36) rot=(0,0,1;1.5708rad)
  shape: bbox 15.24 x 20.32 x 15.57 mm, 647 faces, 37 solids (baked)
FEATURE [Part::Feature] Compound067002001  label="pololu-A500_004"
  Placement = pos=(-57.3,205.1,36) rot=(0,0,1;1.5708rad)
  shape: bbox 15.24 x 20.32 x 15.57 mm, 647 faces, 37 solids (baked)
FEATURE [Part::Feature] Compound067002002  label="pololu-A500_005"
  Placement = pos=(-57.3,184.7,36) rot=(0,0,1;1.5708rad)
  shape: bbox 15.24 x 20.32 x 15.57 mm, 647 faces, 37 solids (baked)
FEATURE [App::Part] Part014  label="pololu-A500"
  Group = -> [Sketch047,Pocket021005005004,Pad001010,LinearPattern002,Sketch048,Group010,Pad001011,Sketch049,Group011,Pocket001001,Sketch050,Pad002002001,Pad002003,Compound063,Sketch051,Sketch052,Pocket021005005005,Pad002002,Group012,Pad002001,LinearPattern003,Compound065,Compound064,Compound066,Pad002002002,Compound067,Compound067001,Compound067002,Compound067002001,Compound067002002]
  License = CC BY 3.0
  LicenseURL = http://creativecommons.org/licenses/by/3.0/
  Origin = -> Origin014
  Placement = pos=(215,42,-10) rot=(0,0,1;1.5708rad)
FEATURE [Part::Feature] Box015001001  label="Cube005"
  Placement = pos=(-12,255,3.2) rot=(0,0,1;0rad)
  shape: bbox 21 x 21 x 2 mm, 6 faces (baked)
FEATURE [Part::Box] Box011  label="Cube"
  AttacherType = Attacher::AttachEngine3D
  Height = 1.6
  Length = 334
  Placement = pos=(-325,-9,3.4) rot=(0,0,1;0rad)
  Width = 277
FEATURE [Part::Box] Box015001002  label="Cube006"
  AttacherType = Attacher::AttachEngine3D
  Height = 2
  Length = 21
  Placement = pos=(-12,-9,3.2) rot=(0,0,1;0rad)
  Width = 21
FEATURE [Part::Feature] Box015001003  label="Cube007"
  Placement = pos=(-325,255,3.2) rot=(0,0,1;0rad)
  shape: bbox 21 x 21 x 2 mm, 6 faces (baked)
FEATURE [Part::Feature] Box015001  label="Cube004"
  Placement = pos=(-325,-9,3.2) rot=(0,0,1;0rad)
  shape: bbox 21 x 21 x 2 mm, 6 faces (baked)
FEATURE [Part::Feature] Part__Feature  label="SHF8"
  Placement = pos=(-6,0,0) rot=(0,0,1;0rad)
  shape: bbox 42 x 24 x 10 mm, 87 faces (baked)
FEATURE [Part::Feature] Part__Feature001  label="SHF009"
  Placement = pos=(-8,0,0) rot=(0,0,1;0rad)
  shape: bbox 22.8 x 7.577 x 7.577 mm, 30 faces (baked)
FEATURE [App::Part] SHF8  label="SHF8_001"
  Group = -> [Part__Feature,Part__Feature001]
  License = CC BY 3.0
  LicenseURL = http://creativecommons.org/licenses/by/3.0/
  Origin = -> Origin016
  Placement = pos=(0,44,25) rot=(0,0,-1;1.5708rad)
FEATURE [Part::Feature] Part__Feature002  label="SHF010"
  Placement = pos=(-7,0,0) rot=(0,0,1;0rad)
  shape: bbox 22.8 x 7.577 x 7.577 mm, 30 faces (baked)
FEATURE [Part::Feature] Part__Feature003  label="SHF011"
  Placement = pos=(-6,0,0) rot=(0,0,1;0rad)
  shape: bbox 42 x 24 x 10 mm, 87 faces (baked)
FEATURE [App::Part] SHF009  label="SHF8_002"
  Group = -> [Part__Feature003,Part__Feature002]
  License = CC BY 3.0
  LicenseURL = http://creativecommons.org/licenses/by/3.0/
  Origin = -> Origin017
  Placement = pos=(0,223,35) rot=(0.707107,0.707107,0;-3.14159rad)
FEATURE [Part::Feature] Part__Feature004  label="SHF012"
  Placement = pos=(-7,0,0) rot=(0,0,1;0rad)
  shape: bbox 22.8 x 7.577 x 7.577 mm, 30 faces (baked)
FEATURE [Part::Feature] Part__Feature005  label="SHF013"
  Placement = pos=(-6,0,0) rot=(0,0,1;0rad)
  shape: bbox 42 x 24 x 10 mm, 87 faces (baked)
FEATURE [App::Part] SHF010  label="SHF8_003"
  Group = -> [Part__Feature005,Part__Feature004]
  License = CC BY 3.0
  LicenseURL = http://creativecommons.org/licenses/by/3.0/
  Origin = -> Origin018
  Placement = pos=(0,223,430) rot=(0.707107,0.707107,0;-3.14159rad)
FEATURE [Part::Feature] Part__Feature006  label="SHF014"
  Placement = pos=(-8,0,0) rot=(0,0,1;0rad)
  shape: bbox 22.8 x 7.577 x 7.577 mm, 30 faces (baked)
FEATURE [Part::Feature] Part__Feature007  label="SHF015"
  Placement = pos=(-6,0,0) rot=(0,0,1;0rad)
  shape: bbox 42 x 24 x 10 mm, 87 faces (baked)
FEATURE [App::Part] SHF011  label="SHF8_004"
  Group = -> [Part__Feature007,Part__Feature006]
  License = CC BY 3.0
  LicenseURL = http://creativecommons.org/licenses/by/3.0/
  Origin = -> Origin019
  Placement = pos=(0,44,420) rot=(0,0,-1;1.5708rad)
FEATURE [Part::Cylinder] Cylinder012029  label="Rod_Right_1"
  Angle = 360
  AttacherType = Attacher::AttachEngine3D
  Height = 400
  Placement = pos=(0,50,28) rot=(0,0,1;0rad)
  Radius = 4
FEATURE [Part::Feature] Cylinder012029001001  label="Rod_Right_2"
  Placement = pos=(0,217,28) rot=(0,0,1;0rad)
  shape: bbox 8 x 8 x 400 mm, 3 faces (baked)
FEATURE [App::Part] Part026  label="Rails_Right"
  Group = -> [Cylinder012029,Cylinder012029001001]
  License = CC BY 3.0
  LicenseURL = http://creativecommons.org/licenses/by/3.0/
  Origin = -> Origin030
FEATURE [Part::Feature] Part__Feature008  label="Full Graphic Smart Controller"
  Placement = pos=(245,-16,60) rot=(0.57735,0.57735,0.57735;2.0944rad)
  shape: bbox 34.7 x 102.9 x 86.75 mm, 117 faces (baked)
FEATURE [Part::Feature] Part__Feature009  label="LMH8UU_"
  Placement = pos=(0,50,0) rot=(-1,0,0;1.5708rad)
  shape: bbox 20 x 32 x 23 mm, 46 faces (baked)
FEATURE [Part::Feature] Part__Feature009002  label="nakretka tr08"
  Placement = pos=(0,0,0) rot=(-1,0,0;1.5708rad)
  shape: bbox 21.75 x 21.75 x 14.8 mm, 17 faces (baked)
FEATURE [Part::Feature] Part__Feature009003  label="napinacz nakretki tr8"
  Placement = pos=(0,0,23.8) rot=(0,0.707107,-0.707107;3.14159rad)
  shape: bbox 13.75 x 13.75 x 15 mm, 13 faces (baked)
FEATURE [Part::Feature] Part__Feature009004  label="sprezyna nakretka tr 8"
  Placement = pos=(0,0,1.3) rot=(0,0,1;0rad)
  shape: bbox 11.8 x 11.79 x 19.8 mm, 5 faces (baked)
FEATURE [App::Part] TR08  label="TR08_001"
  Group = -> [Part__Feature009002,Part__Feature009003,Part__Feature009004]
  License = CC BY 3.0
  LicenseURL = http://creativecommons.org/licenses/by/3.0/
  Origin = -> Origin032
  Placement = pos=(11,120.5,2) rot=(1,0,0;-3.14159rad)
FEATURE [Part::Feature] Part__Feature009005  label="Power Inlet with Switch_STEP"
  shape: bbox 11.05 x 0.48 x 23.77 mm, 286 faces (baked)
FEATURE [Part::Feature] Part__Feature009006  label="Power Inlet with Switch_STEP001"
  shape: bbox 14.48 x 27.86 x 20.83 mm, 80 faces (baked)
FEATURE [Part::Feature] Part__Feature009007  label="Power Inlet with Switch_STEP002"
  shape: bbox 58.82 x 28.06 x 49.35 mm, 135 faces (baked)
FEATURE [App::Part] Power_Inlet_with_Switch_STEP
  Group = -> [Part__Feature009005,Part__Feature009006,Part__Feature009007]
  License = CC BY 3.0
  LicenseURL = http://creativecommons.org/licenses/by/3.0/
  Origin = -> Origin033
  Placement = pos=(-248,266,28) rot=(0,1,0;-3.14159rad)
FEATURE [Part::Box] Box015001005  label="Cube009"
  AttacherType = Attacher::AttachEngine3D
  Height = 28
  Length = 55
  Placement = pos=(-275.5,267,14) rot=(0,0,1;0rad)
  Width = 4
FEATURE [Part::Fillet] Fillet001
  Base = -> Box015001005
  Edges = 4 edges r=1: [Edge2,Edge4,Edge6,Edge8]
FEATURE [Part::Feature] Compound062001  label="Nyloc-nut-M-004"
  Placement = pos=(0,6,0) rot=(0,1,0;3.14159rad)
  shape: bbox 6.35 x 6.35 x 3.86 mm, 36 faces, 2 solids (baked)
FEATURE [Part::Feature] Compound062001001  label="Nyloc-nut-M-003"
  Placement = pos=(0,30,0) rot=(0,1,0;3.14159rad)
  shape: bbox 6.35 x 6.35 x 3.86 mm, 36 faces, 2 solids (baked)
FEATURE [Part::Feature] Compound062001001001  label="Nyloc-nut-M-002"
  Placement = pos=(0,173,0) rot=(0,1,0;3.14159rad)
  shape: bbox 6.35 x 6.35 x 3.86 mm, 36 faces, 2 solids (baked)
FEATURE [Part::Feature] Compound062001001002  label="Nyloc-nut-M-001"
  Placement = pos=(0,197,0) rot=(0,1,0;3.14159rad)
  shape: bbox 6.35 x 6.35 x 3.86 mm, 36 faces, 2 solids (baked)
FEATURE [Part::Feature] Compound062001001003  label="Nyloc-nut-M-005"
  Placement = pos=(11,93.5,0) rot=(0.965926,0.258819,0;3.14159rad)
  shape: bbox 6.35 x 6.35 x 3.86 mm, 36 faces, 2 solids (baked)
FEATURE [Part::Feature] Compound062001001003001  label="Nyloc-nut-M-006"
  Placement = pos=(11,109.5,0) rot=(0.965926,0.258819,0;3.14159rad)
  shape: bbox 6.35 x 6.35 x 3.86 mm, 36 faces, 2 solids (baked)
FEATURE [Part::Feature] Compound062001001003001001  label="Nyloc-nut-M-007"
  Placement = pos=(19,101.5,0) rot=(1,0,0;3.14159rad)
  shape: bbox 6.35 x 6.35 x 3.86 mm, 36 faces, 2 solids (baked)
FEATURE [Part::Feature] Compound062001001003001001001  label="Nyloc-nut-M-008"
  Placement = pos=(3,101.5,0) rot=(1,0,0;3.14159rad)
  shape: bbox 6.35 x 6.35 x 3.86 mm, 36 faces, 2 solids (baked)
FEATURE [Part::Cylinder] Cylinder012006  label="Cilindro"
  Angle = 360
  AttacherType = Attacher::AttachEngine3D
  Height = 7.6
  Placement = pos=(6.1,0,0) rot=(0,0,1;0rad)
  Radius = 0.6
FEATURE [Part::Feature] Cut002001  label="Polea"
  Placement = pos=(0,0,0) rot=(1,0,0;3.14159rad)
  shape: bbox 18 x 18 x 14.6 mm, 50 faces (baked)
FEATURE [Part::Feature] Pocket017  label="TornilloM3"
  Placement = pos=(0.5,0,-15) rot=(0,0,1;0rad)
  shape: bbox 6 x 3 x 3 mm, 12 faces (baked)
FEATURE [Part::FeaturePython] Array003008004001001001002001001004  # Draft array (typed FeaturePython)
  Angle = 360
  ArrayType = 1
  Axis = (0,0,1)
  Base = -> Cylinder012006
  Center = (0,0,0)
  IntervalX = (1,0,0)
  IntervalY = (0,1,0)
  IntervalZ = (0,0,1)
  NumberPolar = 20
  NumberX = 2
  NumberY = 2
  NumberZ = 1
FEATURE [Part::Cylinder] Cylinder012007  label="Cilindro002"
  Angle = 360
  AttacherType = Attacher::AttachEngine3D
  Height = 1
  Radius = 9
FEATURE [Part::Chamfer] Chamfer
  Base = -> Cylinder012007
  Edges = 1 edges r=0.5: [Edge1]
FEATURE [Part::Cylinder] Cylinder012008  label="Cilindro004"
  Angle = 360
  AttacherType = Attacher::AttachEngine3D
  Height = 14.6
  Radius = 2.5
FEATURE [Part::Cylinder] Cylinder012009  label="Cilindro003"
  Angle = 360
  AttacherType = Attacher::AttachEngine3D
  Height = 6
  Placement = pos=(0,0,8.6) rot=(0,0,1;0rad)
  Radius = 9
FEATURE [Part::Chamfer] Chamfer001
  Base = -> Cylinder012009
  Edges = 1 edges r=0.5: [Edge3]
FEATURE [Part::Cylinder] Cylinder012010  label="Cilindro006"
  Angle = 360
  AttacherType = Attacher::AttachEngine3D
  Height = 6
  Placement = pos=(3,0,2.6) rot=(0,1,0;1.5708rad)
  Radius = 1.5
FEATURE [Part::Chamfer] Chamfer002
  Base = -> Cylinder012010
  Edges = 2 edges r=0.25: [Edge1,Edge3]
FEATURE [Sketcher::SketchObject] Sketch022
  ExternalGeometry = -> [Chamfer002]
  MapMode = 5
  Placement = pos=(9,0,0) rot=(0.57735,0.57735,0.57735;2.0944rad)
  Support = -> [Chamfer002]
  sketch-geometry (9):
    g0: LineSegment StartX=-1 StartY=3.17735 StartZ=0 EndX=0 EndY=3.7547 EndZ=0
    g1: LineSegment StartX=0 StartY=3.7547 StartZ=0 EndX=1 EndY=3.17735 EndZ=0
    g2: LineSegment StartX=1 StartY=3.17735 StartZ=0 EndX=1 EndY=2.02265 EndZ=0
    g3: LineSegment StartX=1 StartY=2.02265 StartZ=0 EndX=0 EndY=1.4453 EndZ=0
    g4: LineSegment StartX=0 StartY=1.4453 StartZ=0 EndX=-1 EndY=2.02265 EndZ=0
    g5: LineSegment StartX=-1 StartY=2.02265 StartZ=0 EndX=-1 EndY=3.17735 EndZ=0
    g6: LineSegment [constr] StartX=0 StartY=2.6 StartZ=0 EndX=0 EndY=3.7547 EndZ=0
    g7: LineSegment [constr] StartX=0 StartY=2.6 StartZ=0 EndX=0 EndY=1.4453 EndZ=0
    g8: LineSegment [constr] StartX=0 StartY=2.6 StartZ=0 EndX=-1 EndY=3.17735 EndZ=0
  constraints (24):
    c: Coincident(g0,g1)
    c: Coincident(g1,g2)
    c: Coincident(g2,g3)
    c: Coincident(g3,g4)
    c: Coincident(g4,g5)
    c: Coincident(g5,g0)
    c: Vertical(g5)
    c: Vertical(g2)
    c: Equal(g0,g1)
    c: Equal(g1,g2)
    c: Equal(g2,g3)
    c: Equal(g3,g4)
    c: Equal(g4,g5)
    c: Coincident(g8,g-3)
    c: Coincident(g8,g6)
    c: Coincident(g8,g7)
    c: Coincident(g8,g0)
    c: Coincident(g6,g0)
    c: Coincident(g7,g3)
    c: Equal(g6,g8)
    c: Equal(g8,g7)
    c: Vertical(g6)
    c: Vertical(g7)
    c: DistanceX(g4,g2) = 2
FEATURE [PartDesign::Pocket] Pocket018  label="Tornillo"
  Length = 2.5
  Length2 = 100
  Profile = -> Sketch022
  Type = 0
FEATURE [Part::Cylinder] Cylinder012011  label="Cilindro001"
  Angle = 360
  AttacherType = Attacher::AttachEngine3D
  Height = 7.6
  Radius = 6.1
FEATURE [Part::Cut] Cut002004
  Base = -> Cylinder012011
  Placement = pos=(0,0,1) rot=(0,0,1;0rad)
  Tool = -> Array003008004001001001002001001004
FEATURE [Part::MultiFuse] Fusion007
  Shapes = -> [Cut002004,Chamfer,Chamfer001]
FEATURE [Part::Cut] Cut002003
  Base = -> Fusion007
  Tool = -> Cylinder012008
FEATURE [Part::Cylinder] Cylinder012012  label="Cilindro005"
  Angle = 360
  AttacherType = Attacher::AttachEngine3D
  Height = 9
  Placement = pos=(1,0,12) rot=(0,1,0;1.5708rad)
  Radius = 1.5
FEATURE [Part::Cut] Cut002002
  Base = -> Cut002003
  Tool = -> Cylinder012012
FEATURE [App::Part] Part003  label="GT2-20T"
  Group = -> [Cylinder012006,Fusion007,Array003008004001001001002001001004,Cylinder012007,Cut002003,Chamfer,Cut002004,Cylinder012008,Cylinder012009,Cylinder012011,Cylinder012012,Chamfer001,Cut002002,Cut002001,Chamfer002,Sketch022,Cylinder012010,Pocket018,Pocket017]
  License = CC BY 3.0
  LicenseURL = http://creativecommons.org/licenses/by/3.0/
  Origin = -> Origin003
  Placement = pos=(0,0,-60) rot=(0,1,0;3.14159rad)
FEATURE [Part::Feature] Part__Feature009008  label="y_carriage_SC8LUU_right"
  Placement = pos=(-21,260,-14) rot=(0.57735,0.57735,-0.57735;2.0944rad)
  shape: bbox 22 x 58 x 34 mm, 43 faces (baked)
FEATURE [Part::FeaturePython] Clone  label="LMH8UU_001"  # Draft clone (typed FeaturePython)
  AttacherType = Attacher::AttachEngine3D
  Fuse = false
  Objects = -> [Part__Feature009]
  Placement = pos=(20,51,0) rot=(-1,0,0;1.5708rad)
  Scale = (1,1,1)
FEATURE [Part::FeaturePython] Clone001  label="LMH8UU_002"  # Draft clone (typed FeaturePython)
  AttacherType = Attacher::AttachEngine3D
  Fuse = false
  Objects = -> [Clone]
  Placement = pos=(20,218,0) rot=(-1,0,0;1.5708rad)
  Scale = (1,1,1)
FEATURE [Part::Compound] Compound062001001003001001012  label="extruder-motor002"
  Placement = pos=(109.65,-100.5,-442) rot=(0,0,1;0rad)
FEATURE [Sketcher::SketchObject] Sketch114  label="bottom-part-sketch002"
  MapMode = 5
  sketch-geometry (8):
    g0: LineSegment StartX=-16.65 StartY=-21.15 StartZ=0 EndX=16.65 EndY=-21.15 EndZ=0
    g1: LineSegment StartX=21.15 StartY=-16.65 StartZ=0 EndX=21.15 EndY=16.65 EndZ=0
    g2: LineSegment StartX=16.65 StartY=21.15 StartZ=0 EndX=-16.65 EndY=21.15 EndZ=0
    g3: LineSegment StartX=-21.15 StartY=16.65 StartZ=0 EndX=-21.15 EndY=-16.65 EndZ=0
    g4: ArcOfCircle CenterX=0 CenterY=0 CenterZ=0 NormalX=0 NormalY=0 NormalZ=1 AngleXU=0 Radius=26.9174 StartAngle=2.2377 EndAngle=2.47468
    g5: ArcOfCircle CenterX=0 CenterY=0 CenterZ=0 NormalX=0 NormalY=0 NormalZ=1 AngleXU=0 Radius=26.9174 StartAngle=3.8085 EndAngle=4.04548
    g6: ArcOfCircle CenterX=0 CenterY=0 CenterZ=0 NormalX=0 NormalY=0 NormalZ=1 AngleXU=0 Radius=26.9174 StartAngle=5.3793 EndAngle=5.61628
    g7: ArcOfCircle CenterX=0 CenterY=0 CenterZ=0 NormalX=0 NormalY=0 NormalZ=1 AngleXU=0 Radius=26.9174 StartAngle=0.666908 EndAngle=0.903888
  constraints (29):
    c: Horizontal(g0)
    c: Horizontal(g2)
    c: Vertical(g1)
    c: Vertical(g3)
    c: PointOnObject(g0,g4)
    c: PointOnObject(g0,g4)
    c: PointOnObject(g1,g4)
    c: PointOnObject(g1,g4)
    c: Coincident(g4,g2)
    c: Coincident(g7,g2)
    c: Equal(g4,g5)
    c: Coincident(g4,g3)
    c: Coincident(g5,g3)
    c: Coincident(g4,g5)
    c: Equal(g5,g6)
    c: PointOnObject(g5,g0)
    c: PointOnObject(g6,g0)
    c: Coincident(g5,g6)
    c: Equal(g6,g7)
    c: PointOnObject(g6,g1)
    c: PointOnObject(g7,g1)
    c: Coincident(g6,g7)
    c: Equal(g3,g2)
    c: Equal(g2,g1)
    c: Equal(g1,g0)
    c: DistanceX(g3,g1) = 42.3
    c: DistanceX(g2) = -33.3
    c: DistanceY(g2) = 21.15
    c: DistanceX(g1) = 21.15
FEATURE [PartDesign::Pad] Pad002002014  label="bottom-slice002"
  Length = 9.6
  Length2 = 100
  Profile = -> Sketch114
  Type = 0
FEATURE [Sketcher::SketchObject] Sketch115  label="middle-part-sketch002"
  ExternalGeometry = -> [Pad002002014]
  MapMode = 5
  Placement = pos=(0,0,9.6) rot=(0,0,1;0rad)
  Support = -> [Pad002002014]
  sketch-geometry (9):
    g0: LineSegment StartX=-21 StartY=-13.75 StartZ=0 EndX=-21 EndY=13.75 EndZ=0
    g1: LineSegment StartX=-21 StartY=13.75 StartZ=0 EndX=-13.75 EndY=21 EndZ=0
    g2: LineSegment StartX=-13.75 StartY=21 StartZ=0 EndX=13.75 EndY=21 EndZ=0
    g3: LineSegment [constr] StartX=-21 StartY=13.75 StartZ=0 EndX=-9 EndY=13.75 EndZ=0
    g4: LineSegment StartX=13.75 StartY=21 StartZ=0 EndX=21 EndY=13.75 EndZ=0
    g5: LineSegment StartX=21 StartY=13.75 StartZ=0 EndX=21 EndY=-13.75 EndZ=0
    g6: LineSegment StartX=21 StartY=-13.75 StartZ=0 EndX=13.75 EndY=-21 EndZ=0
    g7: LineSegment StartX=13.75 StartY=-21 StartZ=0 EndX=-13.75 EndY=-21 EndZ=0
    g8: LineSegment StartX=-13.75 StartY=-21 StartZ=0 EndX=-21 EndY=-13.75 EndZ=0
  constraints (24):
    c: Coincident(g0,g1)
    c: Coincident(g1,g2)
    c: Horizontal(g2)
    c: Symmetric(g0,g0,g-1)
    c: Symmetric(g1,g2,g-2)
    c: Horizontal(g3)
    c: Coincident(g3,g0)
    c: DistanceX(g3) = 12
    c: Angle(g3,g1) = 0.785398
    c: DistanceY(g0) = 27.5
    c: Coincident(g4,g5)
    c: Vertical(g5)
    c: Coincident(g5,g6)
    c: Coincident(g6,g7)
    c: Horizontal(g7)
    c: Coincident(g7,g8)
    c: Coincident(g8,g0)
    c: Symmetric(g1,g7,g-1)
    c: Coincident(g4,g2)
    c: Symmetric(g4,g0,g-2)
    c: Symmetric(g0,g5,g-2)
    c: Symmetric(g6,g7,g-2)
    c: DistanceX(g-1,g0) = -21
    c: Equal(g0,g2)
FEATURE [PartDesign::Pad] Pad002002015  label="middle-slice002"
  Length = 22.75
  Length2 = 100
  Profile = -> Sketch115
  Type = 0
FEATURE [Sketcher::SketchObject] Sketch116  label="top-part-sketch002"
  MapMode = 5
  Placement = pos=(0,0,32.35) rot=(0,0,1;0rad)
  Support = -> [Pad002002015]
  sketch-geometry (8):
    g0: LineSegment StartX=-16.65 StartY=-21.15 StartZ=0 EndX=16.65 EndY=-21.15 EndZ=0
    g1: LineSegment StartX=21.15 StartY=-16.65 StartZ=0 EndX=21.15 EndY=16.65 EndZ=0
    g2: LineSegment StartX=16.65 StartY=21.15 StartZ=0 EndX=-16.65 EndY=21.15 EndZ=0
    g3: LineSegment StartX=-21.15 StartY=16.65 StartZ=0 EndX=-21.15 EndY=-16.65 EndZ=0
    g4: ArcOfCircle CenterX=0 CenterY=0 CenterZ=0 NormalX=0 NormalY=0 NormalZ=1 AngleXU=0 Radius=26.9174 StartAngle=2.2377 EndAngle=2.47468
    g5: ArcOfCircle CenterX=0 CenterY=0 CenterZ=0 NormalX=0 NormalY=0 NormalZ=1 AngleXU=0 Radius=26.9174 StartAngle=3.8085 EndAngle=4.04548
    g6: ArcOfCircle CenterX=0 CenterY=0 CenterZ=0 NormalX=0 NormalY=0 NormalZ=1 AngleXU=0 Radius=26.9174 StartAngle=5.3793 EndAngle=5.61628
    g7: ArcOfCircle CenterX=0 CenterY=0 CenterZ=0 NormalX=0 NormalY=0 NormalZ=1 AngleXU=0 Radius=26.9174 StartAngle=0.666908 EndAngle=0.903888
  constraints (29):
    c: Horizontal(g0)
    c: Horizontal(g2)
    c: Vertical(g1)
    c: Vertical(g3)
    c: PointOnObject(g0,g4)
    c: PointOnObject(g0,g4)
    c: PointOnObject(g1,g4)
    c: PointOnObject(g1,g4)
    c: Coincident(g4,g2)
    c: Coincident(g7,g2)
    c: Equal(g4,g5)
    c: Coincident(g4,g3)
    c: Coincident(g5,g3)
    c: Coincident(g4,g5)
    c: Equal(g5,g6)
    c: PointOnObject(g5,g0)
    c: PointOnObject(g6,g0)
    c: Coincident(g5,g6)
    c: Equal(g6,g7)
    c: PointOnObject(g6,g1)
    c: PointOnObject(g7,g1)
    c: Coincident(g6,g7)
    c: Equal(g3,g2)
    c: Equal(g2,g1)
    c: Equal(g1,g0)
    c: DistanceX(g3,g1) = 42.3
    c: DistanceX(g2) = -33.3
    c: DistanceY(g2) = 21.15
    c: DistanceX(g1) = 21.15
FEATURE [PartDesign::Pad] Pad002002016  label="top-slice002"
  Length = 7.75
  Length2 = 100
  Profile = -> Sketch116
  Type = 0
FEATURE [Sketcher::SketchObject] Sketch117  label="top-drills-sketch002"
  MapMode = 5
  Placement = pos=(0,0,40.1) rot=(0,0,1;0rad)
  Support = -> [Pad002002016]
  sketch-geometry (6):
    g0: LineSegment [constr] StartX=-15.5 StartY=15.5 StartZ=0 EndX=15.5 EndY=15.5 EndZ=0
    g1: LineSegment [constr] StartX=-15.5 StartY=15.5 StartZ=0 EndX=-15.5 EndY=-15.5 EndZ=0
    g2: Circle CenterX=-15.5 CenterY=15.5 CenterZ=0 NormalX=0 NormalY=0 NormalZ=1 AngleXU=0 Radius=1.225
    g3: Circle CenterX=15.5 CenterY=15.5 CenterZ=0 NormalX=0 NormalY=0 NormalZ=1 AngleXU=0 Radius=1.225
    g4: Circle CenterX=15.5 CenterY=-15.5 CenterZ=0 NormalX=0 NormalY=0 NormalZ=1 AngleXU=0 Radius=1.225
    g5: Circle CenterX=-15.5 CenterY=-15.5 CenterZ=0 NormalX=0 NormalY=0 NormalZ=1 AngleXU=0 Radius=1.225
  constraints (15):
    c: Horizontal(g0)
    c: Symmetric(g0,g0,g-2)
    c: Vertical(g1)
    c: Symmetric(g1,g1,g-1)
    c: Equal(g0,g1)
    c: DistanceX(g0) = 31
    c: Coincident(g1,g0)
    c: Radius(g2) = 1.225
    c: Coincident(g2,g0)
    c: Equal(g5,g4)
    c: Equal(g4,g3)
    c: Equal(g3,g2)
    c: Coincident(g3,g0)
    c: Coincident(g5,g1)
    c: Symmetric(g4,g1,g-2)
FEATURE [PartDesign::Pocket] Pocket021005005019001001001001004002022  label="top-drills002"
  Length = 4.5
  Length2 = 100
  Profile = -> Sketch117
  Type = 0
FEATURE [Sketcher::SketchObject] Sketch118  label="shaft-base-sketch002"
  MapMode = 5
  Placement = pos=(0,0,40.1) rot=(0,0,1;0rad)
  Support = -> [Pocket021005005019001001001001004002022]
  sketch-geometry (2):
    g0: Circle CenterX=0 CenterY=0 CenterZ=0 NormalX=0 NormalY=0 NormalZ=1 AngleXU=0 Radius=11
    g1: Circle CenterX=0 CenterY=0 CenterZ=0 NormalX=0 NormalY=0 NormalZ=1 AngleXU=0 Radius=5
  constraints (4):
    c: Coincident(g0,g-1)
    c: Radius(g0) = 11
    c: Coincident(g1,g-1)
    c: Radius(g1) = 5
FEATURE [PartDesign::Pad] Pad002002017  label="shaft-base002"
  Length = 2
  Length2 = 100
  Profile = -> Sketch118
  Type = 0
FEATURE [Sketcher::SketchObject] Sketch119  label="shaft-1-sketch002"
  MapMode = 5
  Placement = pos=(0,0,40.1) rot=(0,0,1;0rad)
  Support = -> [Pad002002017]
  sketch-geometry (1):
    g0: Circle CenterX=0 CenterY=0 CenterZ=0 NormalX=0 NormalY=0 NormalZ=1 AngleXU=0 Radius=2.5
  constraints (2):
    c: Coincident(g0,g-1)
    c: Radius(g0) = 2.5
FEATURE [PartDesign::Pad] Pad002002018  label="shaft-005"
  Length = 20
  Length2 = 100
  Profile = -> Sketch119
  Type = 0
FEATURE [Sketcher::SketchObject] Sketch120  label="shaft-2-sketch002"
  ExternalGeometry = -> [Pad002002018]
  MapMode = 5
  Placement = pos=(0,0,60.1) rot=(0,0,1;0rad)
  Support = -> [Pad002002018]
  sketch-geometry (4):
    g0: LineSegment StartX=-2 StartY=1.5 StartZ=0 EndX=-2 EndY=-1.5 EndZ=0
    g1: LineSegment StartX=-2 StartY=1.5 StartZ=0 EndX=-2.5 EndY=1.5 EndZ=0
    g2: LineSegment StartX=-2.5 StartY=1.5 StartZ=0 EndX=-2.5 EndY=-1.5 EndZ=0
    g3: LineSegment StartX=-2.5 StartY=-1.5 StartZ=0 EndX=-2 EndY=-1.5 EndZ=0
  constraints (12):
    c: Vertical(g0)
    c: Symmetric(g0,g0,g-1)
    c: PointOnObject(g0,g-3)
    c: Coincident(g1,g2)
    c: Coincident(g2,g3)
    c: Horizontal(g3)
    c: Horizontal(g1)
    c: Coincident(g1,g0)
    c: Coincident(g0,g3)
    c: Vertical(g2)
    c: Tangent(g2,g-3)
    c: DistanceX(g1) = -0.5
FEATURE [PartDesign::Pocket] Pocket021005005019001001001001004002023  label="shaft-006"
  Length = 17
  Length2 = 100
  Profile = -> Sketch120
  Type = 0
FEATURE [Sketcher::SketchObject] Sketch121  label="bottom-drills-sketch002"
  MapMode = 5
  Placement = pos=(0,0,0) rot=(1,0,0;3.14159rad)
  Support = -> [Pocket021005005019001001001001004002023]
  sketch-geometry (7):
    g0: LineSegment [constr] StartX=-15.5 StartY=15.5 StartZ=0 EndX=15.5 EndY=15.5 EndZ=0
    g1: LineSegment [constr] StartX=-15.5 StartY=15.5 StartZ=0 EndX=-15.5 EndY=-15.5 EndZ=0
    g2: Circle CenterX=-15.5 CenterY=15.5 CenterZ=0 NormalX=0 NormalY=0 NormalZ=1 AngleXU=0 Radius=1.5
    g3: Circle CenterX=15.5 CenterY=15.5 CenterZ=0 NormalX=0 NormalY=0 NormalZ=1 AngleXU=0 Radius=1.5
    g4: Circle CenterX=15.5 CenterY=-15.5 CenterZ=0 NormalX=0 NormalY=0 NormalZ=1 AngleXU=0 Radius=1.5
    g5: Circle CenterX=-15.5 CenterY=-15.5 CenterZ=0 NormalX=0 NormalY=0 NormalZ=1 AngleXU=0 Radius=1.5
    g6: Circle CenterX=0 CenterY=0 CenterZ=0 NormalX=0 NormalY=0 NormalZ=1 AngleXU=0 Radius=4.5
  constraints (17):
    c: Horizontal(g0)
    c: Vertical(g1)
    c: Coincident(g1,g0)
    c: Symmetric(g0,g0,g-2)
    c: Symmetric(g0,g1,g-1)
    c: Equal(g1,g0)
    c: DistanceX(g0) = 31
    c: Coincident(g2,g0)
    c: Radius(g2) = 1.5
    c: Coincident(g5,g1)
    c: Coincident(g0,g3)
    c: Equal(g3,g2)
    c: Equal(g2,g5)
    c: Equal(g5,g4)
    c: Symmetric(g4,g1,g-2)
    c: Coincident(g6,g-1)
    c: Radius(g6) = 4.5
FEATURE [PartDesign::Pocket] Pocket021005005019001001001001004002024  label="bottom-drills002"
  Length = 3
  Length2 = 100
  Profile = -> Sketch121
  Type = 0
FEATURE [Part::Chamfer] Chamfer003008001001016  label="motor-no-connector002"
  Base = -> Pocket021005005019001001001001004002024
  Edges = 1 edges r=0.4: [Edge102]
FEATURE [Sketcher::SketchObject] Sketch122  label="connector-support-sketch002"
  ExternalGeometry = -> [Chamfer003008001001016]
  MapMode = 5
  Placement = pos=(0,0,0) rot=(1,0,0;3.14159rad)
  Support = -> [Chamfer003008001001016]
  sketch-geometry (4):
    g0: LineSegment StartX=21.15 StartY=8.2 StartZ=0 EndX=25.45 EndY=8.2 EndZ=0
    g1: LineSegment StartX=25.45 StartY=8.2 StartZ=0 EndX=25.45 EndY=-8.2 EndZ=0
    g2: LineSegment StartX=25.45 StartY=-8.2 StartZ=0 EndX=21.15 EndY=-8.2 EndZ=0
    g3: LineSegment StartX=21.15 StartY=-8.2 StartZ=0 EndX=21.15 EndY=8.2 EndZ=0
  constraints (12):
    c: Coincident(g0,g1)
    c: Coincident(g1,g2)
    c: Coincident(g2,g3)
    c: Coincident(g3,g0)
    c: Horizontal(g0)
    c: Horizontal(g2)
    c: Vertical(g1)
    c: Vertical(g3)
    c: Symmetric(g0,g2,g-1)
    c: PointOnObject(g0,g-3)
    c: DistanceY(g1) = -16.4
    c: DistanceX(g0) = 4.3
FEATURE [PartDesign::Pad] Pad002002019  label="connector-motor002"
  Length = 3.6
  Length2 = 100
  Profile = -> Sketch122
  Reversed = true
  Type = 0
FEATURE [Sketcher::SketchObject] Sketch123  label="connector-slot-sketch002"
  ExternalGeometry = -> [Pad002002019]
  MapMode = 5
  Placement = pos=(21.15,0,0) rot=(0.57735,0.57735,0.57735;2.0944rad)
  Support = -> [Pad002002019]
  sketch-geometry (4):
    g0: LineSegment StartX=-8.2 StartY=9.6 StartZ=0 EndX=8.2 EndY=9.6 EndZ=0
    g1: LineSegment StartX=8.2 StartY=9.6 StartZ=0 EndX=8.2 EndY=3.6 EndZ=0
    g2: LineSegment StartX=8.2 StartY=3.6 StartZ=0 EndX=-8.2 EndY=3.6 EndZ=0
    g3: LineSegment StartX=-8.2 StartY=3.6 StartZ=0 EndX=-8.2 EndY=9.6 EndZ=0
  constraints (11):
    c: Coincident(g0,g1)
    c: Coincident(g1,g2)
    c: Coincident(g2,g3)
    c: Coincident(g3,g0)
    c: Horizontal(g0)
    c: Horizontal(g2)
    c: Vertical(g1)
    c: Vertical(g3)
    c: Coincident(g2,g-3)
    c: Coincident(g1,g-3)
    c: PointOnObject(g0,g-4)
FEATURE [PartDesign::Pocket] Pocket021005005019001001001001004002025  label="connector-slot002"
  Length = 1
  Length2 = 100
  Profile = -> Sketch123
  Type = 0
FEATURE [Sketcher::SketchObject] Sketch124  label="connector-main-body-sketch002"
  MapMode = 5
  Placement = pos=(0,0,0) rot=(0.57735,0.57735,0.57735;2.0944rad)
  sketch-geometry (4):
    g0: LineSegment StartX=-7.5 StartY=3.05 StartZ=0 EndX=7.5 EndY=3.05 EndZ=0
    g1: LineSegment StartX=7.5 StartY=3.05 StartZ=0 EndX=7.5 EndY=-3.05 EndZ=0
    g2: LineSegment StartX=7.5 StartY=-3.05 StartZ=0 EndX=-7.5 EndY=-3.05 EndZ=0
    g3: LineSegment StartX=-7.5 StartY=-3.05 StartZ=0 EndX=-7.5 EndY=3.05 EndZ=0
  constraints (11):
    c: Coincident(g0,g1)
    c: Coincident(g1,g2)
    c: Coincident(g2,g3)
    c: Coincident(g3,g0)
    c: Horizontal(g0)
    c: Horizontal(g2)
    c: Vertical(g1)
    c: Vertical(g3)
    c: Symmetric(g0,g1,g-1)
    c: DistanceX(g0) = 15
    c: DistanceY(g1) = -6.1
FEATURE [PartDesign::Pad] Pad002002020  label="connector-main-body002"
  Length = 6.7
  Length2 = 100
  Placement = pos=(0,0,0) rot=(0.57735,0.57735,0.57735;2.0944rad)
  Profile = -> Sketch124
  Type = 0
FEATURE [Sketcher::SketchObject] Sketch125  label="connector-cutout-1-sketch002"
  MapMode = 5
  Placement = pos=(6.7,0,0) rot=(0.57735,0.57735,0.57735;2.0944rad)
  Support = -> [Pad002002020]
  sketch-geometry (8):
    g0: LineSegment StartX=-6.5 StartY=1.85 StartZ=0 EndX=-3.22738 EndY=1.85 EndZ=0
    g1: LineSegment StartX=6.5 StartY=1.85 StartZ=0 EndX=6.5 EndY=-1.85 EndZ=0
    g2: LineSegment StartX=6.5 StartY=-1.85 StartZ=0 EndX=-6.5 EndY=-1.85 EndZ=0
    g3: LineSegment StartX=-6.5 StartY=-1.85 StartZ=0 EndX=-6.5 EndY=1.85 EndZ=0
    g4: LineSegment StartX=-3.22738 StartY=1.85 StartZ=0 EndX=-3.22738 EndY=3.85 EndZ=0
    g5: LineSegment StartX=-3.22738 StartY=3.85 StartZ=0 EndX=3.22738 EndY=3.85 EndZ=0
    g6: LineSegment StartX=3.22738 StartY=3.85 StartZ=0 EndX=3.22738 EndY=1.85 EndZ=0
    g7: LineSegment StartX=3.22738 StartY=1.85 StartZ=0 EndX=6.5 EndY=1.85 EndZ=0
  constraints (21):
    c: Coincident(g7,g1)
    c: Coincident(g1,g2)
    c: Coincident(g2,g3)
    c: Coincident(g3,g0)
    c: Horizontal(g0)
    c: Horizontal(g2)
    c: Vertical(g1)
    c: Vertical(g3)
    c: Symmetric(g0,g1,g-1)
    c: DistanceX(g2) = -13
    c: DistanceY(g1) = -3.7
    c: Vertical(g4)
    c: Coincident(g4,g5)
    c: Horizontal(g5)
    c: Coincident(g5,g6)
    c: Vertical(g6)
    c: Symmetric(g4,g5,g-2)
    c: Coincident(g0,g4)
    c: Coincident(g7,g6)
    c: Tangent(g0,g7)
    c: DistanceY(g6) = -2
FEATURE [PartDesign::Pocket] Pocket021005005019001001001001004002026  label="connector-cutout-003"
  Length = 4.6
  Length2 = 100
  Placement = pos=(0,0,0) rot=(0.57735,0.57735,0.57735;2.0944rad)
  Profile = -> Sketch125
  Type = 0
FEATURE [Part::Box] Box015001010  label="pin-master002"
  AttacherType = Attacher::AttachEngine3D
  Height = 0.5
  Length = 4
  Width = 0.5
FEATURE [Part::FeaturePython] Array003008004001001001002001001007  label="pins002"  # Draft array (typed FeaturePython)
  Angle = 360
  ArrayType = 0
  Axis = (0,0,1)
  Base = -> Box015001010
  Center = (0,0,0)
  IntervalX = (1,0,0)
  IntervalY = (0,2,0)
  IntervalZ = (0,0,1)
  NumberPolar = 1
  NumberX = 1
  NumberY = 6
  NumberZ = 1
  Placement = pos=(2,-5.3,0) rot=(0,0,1;0rad)
FEATURE [Part::MultiFuse] Fusion001008  label="connector002"
  Placement = pos=(20.15,1e-15,6.65) rot=(0,0,1;0rad)
  Shapes = -> [Pocket021005005019001001001001004002026,Array003008004001001001002001001007]
FEATURE [App::DocumentObjectGroup] Group019  label="connector-src002"
  Group = -> [Pad002002020,Pocket021005005019001001001001004002026,Array003008004001001001002001001007]
FEATURE [Part::MultiFuse] Fusion001009  label="Motor-with-connector002"
  Shapes = -> [Pocket021005005019001001001001004002025,Fusion001008]
FEATURE [Part::Feature] Fusion001010  label="Motor-with-connector-final002"
  Placement = pos=(0,0,3.75) rot=(0,1,0;3.14159rad)
  shape: bbox 48 x 42.3 x 60.1 mm, 110 faces (baked)
FEATURE [Part::Feature] Shape  label="y_axis_SK8"
  Placement = pos=(0,0,0) rot=(-1,0,0;1.5708rad)
  shape: bbox 42 x 14 x 33 mm, 45 faces, 2 solids (baked)
FEATURE [Part::FeaturePython] Clone004  label="y_axis_SK8_right_front"  # Draft clone (typed FeaturePython)
  AttacherType = Attacher::AttachEngine3D
  Fuse = false
  Objects = -> [Shape]
  Placement = pos=(-32,-7,0) rot=(-1,0,0;1.5708rad)
  Scale = (1,1,1)
FEATURE [Part::FeaturePython] Clone005  label="y_axis_SK8_right_back"  # Draft clone (typed FeaturePython)
  AttacherType = Attacher::AttachEngine3D
  Fuse = false
  Objects = -> [Shape]
  Placement = pos=(-32,260,0) rot=(-1,0,0;1.5708rad)
  Scale = (1,1,1)
FEATURE [Part::Cylinder] Cylinder012029001016  label="y_rod_right"
  Angle = 360
  AttacherType = Attacher::AttachEngine3D
  Height = 281
  Placement = pos=(-23,274,-14) rot=(1,0,0;1.5708rad)
  Radius = 4
FEATURE [Part::Box] Box022  label="Cube017"
  AttacherType = Attacher::AttachEngine3D
  Height = 3.75
  Length = 65
  Placement = pos=(-25,-25,-40.1) rot=(0,0,1;0rad)
  Width = 65
FEATURE [App::Part] Part048  label="Steppers"
  Group = -> [Compound062001001003001001012,Group019,Pad002002018,Fusion001008,Pocket021005005019001001001001004002023,Pocket021005005019001001001001004002025,Pad002002015,Box015001010,Pad002002017,Sketch121,Sketch122,Sketch118,Chamfer003008001001016,Pad002002019,Sketch117,Pad002002016,Pad002002014,Sketch125,Sketch123,Pad002002020,Sketch114,Sketch119,Sketch124,Sketch120,Pocket021005005019001001001001004002022,+9 more]
  License = CC BY 3.0
  LicenseURL = http://creativecommons.org/licenses/by/3.0/
  Origin = -> Origin060
  Placement = pos=(-31.15,235.85,40.1) rot=(0,0,1;0rad)
FEATURE [Part::FeaturePython] Clone007  label="M3x10-Screw_001"  # WARN: FeaturePython — macro-defined, semantics opaque (R4)
  AttacherType = Attacher::AttachEngine3D
  Fuse = false
  Placement = pos=(11,0,0) rot=(0,0,1;0rad)
  Scale = (1,1,1)
FEATURE [Part::FeaturePython] Clone008  label="M3x10-Screw_002"  # WARN: FeaturePython — macro-defined, semantics opaque (R4)
  AttacherType = Attacher::AttachEngine3D
  Fuse = false
  Placement = pos=(11,16,0) rot=(0,0,1;0rad)
  Scale = (1,1,1)
FEATURE [Part::FeaturePython] Clone009  label="M3x10-Screw_003"  # WARN: FeaturePython — macro-defined, semantics opaque (R4)
  AttacherType = Attacher::AttachEngine3D
  Fuse = false
  Placement = pos=(19,8,0) rot=(0,0,1;0rad)
  Scale = (1,1,1)
FEATURE [Part::FeaturePython] Clone010  label="M3x10-Screw_004"  # WARN: FeaturePython — macro-defined, semantics opaque (R4)
  AttacherType = Attacher::AttachEngine3D
  Fuse = false
  Placement = pos=(3,8,0) rot=(0,0,1;0rad)
  Scale = (1,1,1)
FEATURE [App::Part] Part033  label="TR8_right_Screews"
  Group = -> [Clone008,Clone007,Clone009,Clone010]
  License = CC BY 3.0
  LicenseURL = http://creativecommons.org/licenses/by/3.0/
  Origin = -> Origin039
  Placement = pos=(0,93.5,-1) rot=(0,0,1;0rad)
FEATURE [Part::FeaturePython] Clone011  label="M3x8-Screw_001"  # WARN: FeaturePython — macro-defined, semantics opaque (R4)
  AttacherType = Attacher::AttachEngine3D
  Fuse = false
  Placement = pos=(0,6,0) rot=(0,0,1;0rad)
  Scale = (1,1,1)
FEATURE [Part::FeaturePython] Clone012  label="M3x8-Screw_002"  # WARN: FeaturePython — macro-defined, semantics opaque (R4)
  AttacherType = Attacher::AttachEngine3D
  Fuse = false
  Placement = pos=(0,30,0) rot=(0,0,1;0rad)
  Scale = (1,1,1)
FEATURE [Part::FeaturePython] Clone013  label="M3x8-Screw_003"  # WARN: FeaturePython — macro-defined, semantics opaque (R4)
  AttacherType = Attacher::AttachEngine3D
  Fuse = false
  Placement = pos=(0,173,0) rot=(0,0,1;0rad)
  Scale = (1,1,1)
FEATURE [Part::FeaturePython] Clone014  label="M3x8-Screw_004"  # WARN: FeaturePython — macro-defined, semantics opaque (R4)
  AttacherType = Attacher::AttachEngine3D
  Fuse = false
  Placement = pos=(0,197,0) rot=(0,0,1;0rad)
  Scale = (1,1,1)
FEATURE [App::Part] Part049  label="LMH8UU_right_Screews"
  Group = -> [Clone013,Clone012,Clone014,Clone011]
  License = CC BY 3.0
  LicenseURL = http://creativecommons.org/licenses/by/3.0/
  Origin = -> Origin061
  Placement = pos=(0,0,-3) rot=(0,0,1;0rad)
FEATURE [Part::FeaturePython] Clone015  label="M5x14-Screw_001"  # WARN: FeaturePython — macro-defined, semantics opaque (R4)
  AttacherType = Attacher::AttachEngine3D
  Fuse = false
  Placement = pos=(0,6,0) rot=(0,0,1;0rad)
  Scale = (1,1,1)
FEATURE [Part::FeaturePython] Clone016  label="M5x14-Screw_002"  # WARN: FeaturePython — macro-defined, semantics opaque (R4)
  AttacherType = Attacher::AttachEngine3D
  Fuse = false
  Placement = pos=(0,173,0) rot=(0,0,1;0rad)
  Scale = (1,1,1)
FEATURE [Part::FeaturePython] Clone017  label="M5x14-Screw_003"  # WARN: FeaturePython — macro-defined, semantics opaque (R4)
  AttacherType = Attacher::AttachEngine3D
  Fuse = false
  Placement = pos=(0,205,0) rot=(0,0,1;0rad)
  Scale = (1,1,1)
FEATURE [Part::FeaturePython] Clone018  label="M5x14-Screw_004"  # WARN: FeaturePython — macro-defined, semantics opaque (R4)
  AttacherType = Attacher::AttachEngine3D
  Fuse = false
  Placement = pos=(0,205,385) rot=(0,1,0;3.14159rad)
  Scale = (1,1,1)
FEATURE [Part::FeaturePython] Clone019  label="M5x14-Screw_005"  # WARN: FeaturePython — macro-defined, semantics opaque (R4)
  AttacherType = Attacher::AttachEngine3D
  Fuse = false
  Placement = pos=(0,173,385) rot=(0,1,0;3.14159rad)
  Scale = (1,1,1)
FEATURE [Part::FeaturePython] Clone020  label="M5x14-Screw_006"  # WARN: FeaturePython — macro-defined, semantics opaque (R4)
  AttacherType = Attacher::AttachEngine3D
  Fuse = false
  Placement = pos=(0,38,0) rot=(0,0,1;0rad)
  Scale = (1,1,1)
FEATURE [Part::FeaturePython] Clone021  label="M5x14-Screw_007"  # WARN: FeaturePython — macro-defined, semantics opaque (R4)
  AttacherType = Attacher::AttachEngine3D
  Fuse = false
  Placement = pos=(0,38,385) rot=(0,1,0;3.14159rad)
  Scale = (1,1,1)
FEATURE [Part::FeaturePython] Clone022  label="M5x14-Screw_008"  # WARN: FeaturePython — macro-defined, semantics opaque (R4)
  AttacherType = Attacher::AttachEngine3D
  Fuse = false
  Placement = pos=(0,6,385) rot=(0,1,0;3.14159rad)
  Scale = (1,1,1)
FEATURE [App::Part] Part025
  Group = -> [Clone016,Clone021,Clone020,Clone018,Clone019,Clone015,Clone017,Clone022]
  License = CC BY 3.0
  LicenseURL = http://creativecommons.org/licenses/by/3.0/
  Origin = -> Origin029
  Placement = pos=(0,28,35) rot=(0,0,1;0rad)
FEATURE [Part::FeaturePython] Clone023  label="3-way_corner_bracket_001"  # WARN: FeaturePython — macro-defined, semantics opaque (R4)
  AttacherType = Attacher::AttachEngine3D
  Fuse = false
  Placement = pos=(-10,10,450) rot=(1,0,0;3.14159rad)
  Scale = (1,1,1)
FEATURE [Part::FeaturePython] Clone024  label="3-way_corner_bracket_002"  # WARN: FeaturePython — macro-defined, semantics opaque (R4)
  AttacherType = Attacher::AttachEngine3D
  Fuse = false
  Placement = pos=(10,326,450) rot=(0.707107,-0.707107,0;3.14159rad)
  Scale = (1,1,1)
FEATURE [Part::FeaturePython] Clone025  label="3-way_corner_bracket_003"  # WARN: FeaturePython — macro-defined, semantics opaque (R4)
  AttacherType = Attacher::AttachEngine3D
  Fuse = false
  Placement = pos=(257,-10,450) rot=(0.707107,0.707107,0;3.14159rad)
  Scale = (1,1,1)
FEATURE [Part::FeaturePython] Clone026  label="3-way_corner_bracket_004"  # WARN: FeaturePython — macro-defined, semantics opaque (R4)
  AttacherType = Attacher::AttachEngine3D
  Fuse = false
  Placement = pos=(277,306,450) rot=(0,1,0;3.14159rad)
  Scale = (1,1,1)
FEATURE [App::Part] Part052  label="3-way_corner_bracket"
  License = CC BY 3.0
  LicenseURL = http://creativecommons.org/licenses/by/3.0/
  Origin = -> Origin065
FEATURE [Part::FeaturePython] Clone027  label="2020_L_Internal_Joint_001"  # WARN: FeaturePython — macro-defined, semantics opaque (R4)
  AttacherType = Attacher::AttachEngine3D
  Fuse = false
  Placement = pos=(0,10,19.75) rot=(0,1,0;1.5708rad)
  Scale = (1,1,1)
FEATURE [Part::FeaturePython] Clone028  label="2020_L_Internal_Joint_002"  # WARN: FeaturePython — macro-defined, semantics opaque (R4)
  AttacherType = Attacher::AttachEngine3D
  Fuse = false
  Placement = pos=(0,10,19.75) rot=(0,1,0;1.5708rad)
  Scale = (1,1,1)
FEATURE [Part::FeaturePython] Clone029  label="2020_L_Internal_Joint_003"  # WARN: FeaturePython — macro-defined, semantics opaque (R4)
  AttacherType = Attacher::AttachEngine3D
  Fuse = false
  Placement = pos=(10,0,19.75) rot=(0.57735,0.57735,-0.57735;2.0944rad)
  Scale = (1,1,1)
FEATURE [Part::FeaturePython] Clone030  label="2020_L_Internal_Joint_004"  # WARN: FeaturePython — macro-defined, semantics opaque (R4)
  AttacherType = Attacher::AttachEngine3D
  Fuse = false
  Placement = pos=(0,10,19.75) rot=(0,1,0;1.5708rad)
  Scale = (1,1,1)
FEATURE [App::Part] Part053  label="2020_Internal_L_joint"
  Group = -> [Clone028,Clone029,Clone027,Clone030]
  License = CC BY 3.0
  LicenseURL = http://creativecommons.org/licenses/by/3.0/
  Origin = -> Origin066
FEATURE [App::Part] Part011  label="Basic_Frame"
  Group = -> [Part005,Part009,Part010,Part052,Part053,Clone024,Clone025,Clone023,Clone026]
  License = CC BY 3.0
  LicenseURL = http://creativecommons.org/licenses/by/3.0/
  Origin = -> Origin011
  Placement = pos=(0,0,0) rot=(0,0,1;1.5708rad)
FEATURE [Part::Cylinder] Cylinder012029001024
  Angle = 360
  AttacherType = Attacher::AttachEngine3D
  Height = 6
  Placement = pos=(-248,271,8) rot=(1,0,0;1.5708rad)
  Radius = 1.5
FEATURE [Part::Cylinder] Cylinder012029001025
  Angle = 360
  AttacherType = Attacher::AttachEngine3D
  Height = 6
  Placement = pos=(-248,271,48) rot=(1,0,0;1.5708rad)
  Radius = 1.5
FEATURE [Part::FeaturePython] Screw003  label="M3x10-Screw005"  # Fasteners workbench fastener (typed FeaturePython)
  Placement = pos=(-288.5,270.55,17) rot=(-1,0,0;1.5708rad)
  diameter = 4
  invert = false
  length = 3
  matchOuter = false
  offset = 0
  thread = false
  type = 15
FEATURE [Part::FeaturePython] Nut  label="Nut_000"  # Fasteners workbench fastener (typed FeaturePython)
  Placement = pos=(-288.5,264.8,17) rot=(1,0,0;1.5708rad)
  diameter = 4
  invert = false
  matchOuter = false
  offset = 0
  thread = false
  type = 4
FEATURE [Mesh::Feature] _757035  label="1757035"
  Placement = pos=(-46,-11,27) rot=(-0.57735,-0.57735,-0.57735;2.0944rad)
FEATURE [App::Part] Part012  label="RAMPS"
  Group = -> [Part,Part001,Part014,Part__Feature008,_757035]
  License = CC BY 3.0
  LicenseURL = http://creativecommons.org/licenses/by/3.0/
  Origin = -> Origin012
  Placement = pos=(-42,215,10) rot=(0,0,-1;1.5708rad)
FEATURE [Part::Feature] Cut003024  label="L_000"
  Placement = pos=(-177,124,-8.1) rot=(0,0,1;1.5708rad)
  shape: bbox 17 x 20 x 20 mm, 20 faces (baked)
FEATURE [PartDesign::FeatureBase] Clone035  label="L_001"
  BaseFeature = -> Cut003024
  Placement = pos=(-177,124,-8.1) rot=(0,0,1;1.5708rad)
FEATURE [Part::Cylinder] Cylinder012029001026
  Angle = 360
  AttacherType = Attacher::AttachEngine3D
  Height = 6
  Placement = pos=(-288.5,271,17) rot=(1,0,0;1.5708rad)
  Radius = 1.5
FEATURE [Part::Cylinder] Cylinder012029001027
  Angle = 360
  AttacherType = Attacher::AttachEngine3D
  Height = 6
  Placement = pos=(-207.5,271,17) rot=(1,0,0;1.5708rad)
  Radius = 1.5
FEATURE [Part::Cylinder] Cylinder012029001028
  Angle = 360
  AttacherType = Attacher::AttachEngine3D
  Height = 6
  Placement = pos=(-96.5,271,17) rot=(1,0,0;1.5708rad)
  Radius = 1.5
FEATURE [PartDesign::FeatureBase] Clone039  label="Screw_002"
  BaseFeature = -> Screw003
  Placement = pos=(-207.5,270.55,17) rot=(-1,0,0;1.5708rad)
FEATURE [PartDesign::FeatureBase] Clone040  label="Screw_003"
  BaseFeature = -> Screw003
  Placement = pos=(-96.5,270.55,17) rot=(-1,0,0;1.5708rad)
FEATURE [PartDesign::FeatureBase] Clone041  label="Nut_001"
  BaseFeature = -> Nut
  Placement = pos=(-288.5,264.8,17) rot=(1,0,0;1.5708rad)
FEATURE [PartDesign::FeatureBase] Clone042  label="Nut_002"
  BaseFeature = -> Nut
  Placement = pos=(-207.5,264.8,17) rot=(1,0,0;1.5708rad)
FEATURE [PartDesign::FeatureBase] Clone043  label="Nut_003"
  BaseFeature = -> Nut
  Placement = pos=(-96.5,264.8,17) rot=(1,0,0;1.5708rad)
FEATURE [Part::FeaturePython] Washer  label="Washer_000"  # Fasteners workbench fastener (typed FeaturePython)
  Placement = pos=(-288.5,265.4,17) rot=(1,0,0;1.5708rad)
  diameter = 4
  invert = false
  matchOuter = false
  offset = 0
  type = 0
FEATURE [PartDesign::FeatureBase] Clone044  label="Washer_001i"
  BaseFeature = -> Washer
  Placement = pos=(-288.5,265.4,17) rot=(1,0,0;1.5708rad)
FEATURE [PartDesign::FeatureBase] Clone045  label="Washer_002i"
  BaseFeature = -> Washer
  Placement = pos=(-207.5,265.4,17) rot=(1,0,0;1.5708rad)
FEATURE [PartDesign::FeatureBase] Clone046  label="Washer_003i"
  BaseFeature = -> Washer
  Placement = pos=(-96.5,265.4,17) rot=(1,0,0;1.5708rad)
FEATURE [Part::Box] Box015001022  label="Cube019"
  AttacherType = Attacher::AttachEngine3D
  Height = 2
  Length = 5.5
  Placement = pos=(-11.5,270.2,46) rot=(1,0,0;1.5708rad)
  Width = 7
FEATURE [Part::Box] Box015001023  label="Cube020"
  AttacherType = Attacher::AttachEngine3D
  Height = 2
  Length = 2.5
  Placement = pos=(-8.5,270.2,41) rot=(1,0,0;1.5708rad)
  Width = 12
FEATURE [Part::Box] Box015001024  label="Cube021"
  AttacherType = Attacher::AttachEngine3D
  Height = 2
  Length = 5.5
  Placement = pos=(-310,270.2,46) rot=(1,0,0;1.5708rad)
  Width = 7
FEATURE [Part::Box] Box015001025  label="Cube022"
  AttacherType = Attacher::AttachEngine3D
  Height = 2
  Length = 2.5
  Placement = pos=(-310,270.2,41) rot=(1,0,0;1.5708rad)
  Width = 12
FEATURE [Part::MultiFuse] Fusion001012
  Shapes = -> [Box015001025,Box013,Fillet001,Cylinder012029001024,Cylinder012029001025,Cylinder012029001026,Cylinder012029001028,Box015001024,Box015001023,Box015001022,Cylinder012029001027]
FEATURE [Part::Cut] Cut003025
  Base = -> Box012
  Tool = -> Fusion001012
FEATURE [App::DocumentObjectGroup] Group027  label="Shapes_Back_Panel"
  Group = -> [Cut003025]
FEATURE [Part::Box] Box015001026  label="Cube023"
  AttacherType = Attacher::AttachEngine3D
  Height = 2
  Length = 10
  Placement = pos=(-253,265,3.2) rot=(0,0,1;0rad)
  Width = 3
FEATURE [Part::MultiFuse] Fusion001013
  Shapes = -> [Box015001,Box015001001,Box015001002,Box015001003,Box015001026]
FEATURE [Part::Cut] Cut003026
  Base = -> Box011
  Tool = -> Fusion001013
FEATURE [App::DocumentObjectGroup] Group029  label="Shapes_Bottom_Panel"
  Group = -> [Cut003026]
FEATURE [PartDesign::FeatureBase] Clone049  label="Washer_004i"
  BaseFeature = -> Washer
  Placement = pos=(-248,266,48) rot=(1,0,0;1.5708rad)
FEATURE [PartDesign::FeatureBase] Clone050  label="Washer_005i"
  BaseFeature = -> Washer
  Placement = pos=(-248,266,8) rot=(1,0,0;1.5708rad)
FEATURE [PartDesign::FeatureBase] Clone052  label="Nut_007"
  BaseFeature = -> Nut
  Placement = pos=(-288.5,264.8,17) rot=(1,0,0;1.5708rad)
FEATURE [PartDesign::FeatureBase] Clone053  label="Nut_008"
  BaseFeature = -> Nut
  Placement = pos=(-288.5,264.8,17) rot=(1,0,0;1.5708rad)
FEATURE [PartDesign::FeatureBase] Clone070  label="Washer_005e"
  BaseFeature = -> Washer
  Placement = pos=(-248,270.55,8) rot=(1,0,0;1.5708rad)
FEATURE [PartDesign::FeatureBase] Clone071  label="Washer_004e"
  BaseFeature = -> Washer
  Placement = pos=(-248,270.55,48) rot=(1,0,0;1.5708rad)
FEATURE [PartDesign::FeatureBase] Clone072  label="Washer_001e"
  BaseFeature = -> Washer
  Placement = pos=(-288.5,270.55,17) rot=(1,0,0;1.5708rad)
FEATURE [PartDesign::FeatureBase] Clone073  label="Washer_002e"
  BaseFeature = -> Washer
  Placement = pos=(-207.5,270.55,17) rot=(1,0,0;1.5708rad)
FEATURE [PartDesign::FeatureBase] Clone074  label="Washer_003e"
  BaseFeature = -> Washer
  Placement = pos=(-96.5,270.55,17) rot=(1,0,0;1.5708rad)
FEATURE [App::DocumentObjectGroup] Group026  label="Back_Fasteners_Panel"
  Group = -> [Clone035,Cut003024,Clone043,Clone042,Clone041,Clone040,Clone039,Clone044,Clone045,Screw003,Nut,Washer,Clone049,Clone050,Clone052,Clone053,Clone070,Clone071,Clone072,Clone073,Clone074,Clone046]
FEATURE [App::DocumentObjectGroup] Group021  label="Back_Panel"
  Group = -> [Group026,Group027]
FEATURE [Part::FeaturePython] Screw004  label="M3x10-Screw004"  # Fasteners workbench fastener (typed FeaturePython)
  Placement = pos=(-288.5,257,2.85) rot=(1,0,0;3.14159rad)
  diameter = 1
  invert = false
  length = 2
  matchOuter = false
  offset = 0
  thread = false
  type = 20
FEATURE [PartDesign::FeatureBase] Clone075  label="Screw_006"
  BaseFeature = -> Screw004
  Placement = pos=(-288.5,257,2.85) rot=(1,0,0;3.14159rad)
FEATURE [Part::FeaturePython] Nut001  label="M3-Nut"  # Fasteners workbench fastener (typed FeaturePython)
  Placement = pos=(-288.5,256.8,8.55) rot=(1,0,0;0rad)
  diameter = 4
  invert = false
  matchOuter = false
  offset = 0
  thread = false
  type = 4
FEATURE [PartDesign::FeatureBase] Clone048  label="Nut_006"
  BaseFeature = -> Nut001
  Placement = pos=(-288.5,256.8,8.55) rot=(1,0,0;0rad)
FEATURE [Part::FeaturePython] Washer001  label="M3-Washer"  # Fasteners workbench fastener (typed FeaturePython)
  Placement = pos=(-288.5,257,8) rot=(1,0,0;0rad)
  diameter = 4
  invert = false
  matchOuter = false
  offset = 0
  type = 0
FEATURE [PartDesign::FeatureBase] Clone051  label="Washer_006i"
  BaseFeature = -> Washer001
  Placement = pos=(-288.5,257,8) rot=(0,0,1;0rad)
FEATURE [PartDesign::FeatureBase] Clone069  label="Washer_006e"
  BaseFeature = -> Washer001
  Placement = pos=(-288.5,257,2.85) rot=(0,0,1;0rad)
FEATURE [PartDesign::FeatureBase] Clone076  label="Nut_009"
  BaseFeature = -> Screw004
  Placement = pos=(-207.5,257,2.85) rot=(1,0,0;3.14159rad)
FEATURE [PartDesign::FeatureBase] Clone077  label="Nut_010"
  BaseFeature = -> Screw004
  Placement = pos=(-96.5,257,2.85) rot=(1,0,0;3.14159rad)
FEATURE [PartDesign::FeatureBase] Clone078
  BaseFeature = -> Nut001
  Placement = pos=(-207.5,256.8,8.55) rot=(1,0,0;0rad)
FEATURE [PartDesign::FeatureBase] Clone079
  BaseFeature = -> Nut001
  Placement = pos=(-96.5,256.8,8.55) rot=(1,0,0;0rad)
FEATURE [PartDesign::FeatureBase] Clone080
  BaseFeature = -> Clone051
  Placement = pos=(-207.5,257,8) rot=(0,0,1;0rad)
FEATURE [PartDesign::FeatureBase] Clone081
  BaseFeature = -> Clone051
  Placement = pos=(-96.5,257,8) rot=(0,0,1;0rad)
FEATURE [PartDesign::FeatureBase] Clone082
  BaseFeature = -> Clone069
  Placement = pos=(-207.5,257,2.85) rot=(0,0,1;0rad)
FEATURE [PartDesign::FeatureBase] Clone083
  BaseFeature = -> Clone069
  Placement = pos=(-96.5,257,2.85) rot=(0,0,1;0rad)
FEATURE [App::DocumentObjectGroup] Group028  label="Bottom_Fasteners_Panel"
  Group = -> [Clone075,Screw004,Clone069,Clone051,Clone048,Nut001,Washer001,Clone076,Clone077,Clone078,Clone079,Clone080,Clone081,Clone082,Clone083]
FEATURE [App::DocumentObjectGroup] Group022  label="Bottom_Panel"
  Group = -> [Group028,Group029]
FEATURE [App::DocumentObjectGroup] Group020  label="Panels"
  Group = -> [Group021,Group022]
FEATURE [Part::Box] Box015001027  label="Cube024"
  AttacherType = Attacher::AttachEngine3D
  Height = 40
  Length = 90
  Placement = pos=(-294,29,5) rot=(0,0,1;0rad)
  Width = 170
FEATURE [App::Part] Part056  label="Power Suppy"
  Group = -> [Box015001027]
  License = CC BY 3.0
  LicenseURL = http://creativecommons.org/licenses/by/3.0/
  Origin = -> Origin069
FEATURE [Part::Feature] Part__Feature018  label="Header 3 pin v5"
  Placement = pos=(31.41,0,-3.01) rot=(0,-1,0;1.5708rad)
  shape: bbox 5.9 x 7 x 10.16 mm, 44 faces (baked)
FEATURE [Part::Feature] Part__Feature042  label="COMPOUND005"
  shape: bbox 1.7 x 0.6509 x 1.7 mm, 7 faces (baked)
FEATURE [Part::Feature] Part__Feature023  label="BL-LS0805UWC v004"
  Placement = pos=(26.5,0.0068546,-2.40685) rot=(-1,0,0;1.5708rad)
  shape: bbox 0.1999 x 0.199 x 0.1999 mm, 6 faces (baked)
FEATURE [Part::Feature] Part__Feature040  label="COMPOUND003"
  shape: bbox 1.795 x 0.7 x 1.795 mm, 3 faces (baked)
FEATURE [Part::Feature] Part__Feature045  label="COMPOUND008"
  shape: bbox 1.7 x 0.6509 x 1.7 mm, 7 faces (baked)
FEATURE [Part::Feature] Part__Feature019  label="Header 3 pin v006"
  Placement = pos=(30.512,0,-3.01) rot=(0,-1,0;1.5708rad)
  shape: bbox 0.6 x 9.1 x 0.6 mm, 10 faces (baked)
FEATURE [Part::Feature] Part__Feature028  label="RES0805 v004"
  Placement = pos=(27,0.005,-0.255) rot=(-1,0,0;1.5708rad)
  shape: bbox 0.4 x 0.5 x 1.25 mm, 15 faces (baked)
FEATURE [Part::Feature] Part__Feature020  label="Header 3 pin v007"
  Placement = pos=(30.512,0,-3.01) rot=(0,-1,0;1.5708rad)
  shape: bbox 0.6 x 9.1 x 0.6 mm, 10 faces (baked)
FEATURE [Part::Feature] Part__Feature032  label="RES0805 v008"
  Placement = pos=(12.5,-1.605,-0.245) rot=(1,0,0;1.5708rad)
  shape: bbox 0.4 x 0.5 x 1.25 mm, 15 faces (baked)
FEATURE [Part::Feature] Part__Feature030  label="RES0805 v006"
  Placement = pos=(12.5,-1.605,-0.245) rot=(1,0,0;1.5708rad)
  shape: bbox 1.2 x 0.05 x 1.25 mm, 6 faces (baked)
FEATURE [Part::Feature] Part__Feature029  label="RES0805 v005"
  Placement = pos=(12.5,-1.605,-0.245) rot=(1,0,0;1.5708rad)
  shape: bbox 1.9 x 0.4 x 1.25 mm, 10 faces (baked)
FEATURE [Part::Feature] Part__Feature034  label="RES0805 v010"
  Placement = pos=(12.5,-1.605,-6.045) rot=(1,0,0;1.5708rad)
  shape: bbox 1.2 x 0.05 x 1.25 mm, 6 faces (baked)
FEATURE [Part::Feature] Part__Feature044  label="COMPOUND007"
  shape: bbox 1.7 x 0.6509 x 1.7 mm, 7 faces (baked)
FEATURE [Part::Feature] Part__Feature039  label="COMPOUND002"
  shape: bbox 1.795 x 0.7 x 1.795 mm, 3 faces (baked)
FEATURE [Part::Feature] Part__Feature036  label="RES0805 v012"
  Placement = pos=(12.5,-1.605,-6.045) rot=(1,0,0;1.5708rad)
  shape: bbox 0.4 x 0.5 x 1.25 mm, 15 faces (baked)
FEATURE [Part::Feature] Part__Feature026  label="RES0805 v002"
  Placement = pos=(27,0.005,-0.255) rot=(-1,0,0;1.5708rad)
  shape: bbox 1.2 x 0.05 x 1.25 mm, 6 faces (baked)
FEATURE [Part::Feature] Part__Feature027  label="RES0805 v003"
  Placement = pos=(27,0.005,-0.255) rot=(-1,0,0;1.5708rad)
  shape: bbox 0.4 x 0.5 x 1.25 mm, 15 faces (baked)
FEATURE [Part::Feature] Part__Feature037  label="COMPOUND"
  shape: bbox 24.5 x 14.7 x 6.01 mm, 397 faces (baked)
FEATURE [Part::Feature] Part__Feature025  label="RES0805 v1"
  Placement = pos=(27,0.005,-0.255) rot=(-1,0,0;1.5708rad)
  shape: bbox 1.9 x 0.4 x 1.25 mm, 10 faces (baked)
FEATURE [Part::Feature] Part__Feature033  label="RES0805 v009"
  Placement = pos=(12.5,-1.605,-6.045) rot=(1,0,0;1.5708rad)
  shape: bbox 1.9 x 0.4 x 1.25 mm, 10 faces (baked)
FEATURE [Part::Feature] Part__Feature021  label="Header 3 pin v008"
  Placement = pos=(30.512,0,-3.01) rot=(0,-1,0;1.5708rad)
  shape: bbox 0.6 x 9.1 x 0.6 mm, 10 faces (baked)
FEATURE [Part::Feature] Part__Feature043  label="COMPOUND006"
  shape: bbox 1.7 x 0.6509 x 1.7 mm, 7 faces (baked)
FEATURE [Part::Feature] Part__Feature024  label="BL-LS0805UWC v005"
  Placement = pos=(26.5,0.0068546,-2.40685) rot=(-1,0,0;1.5708rad)
  shape: bbox 1.8 x 0.301 x 1.25 mm, 30 faces (baked)
FEATURE [Part::Feature] Part__Feature041  label="COMPOUND004"
  shape: bbox 1.795 x 0.7 x 1.795 mm, 3 faces (baked)
FEATURE [Part::Feature] Part__Feature035  label="RES0805 v011"
  Placement = pos=(12.5,-1.605,-6.045) rot=(1,0,0;1.5708rad)
  shape: bbox 0.4 x 0.5 x 1.25 mm, 15 faces (baked)
FEATURE [Part::Feature] Part__Feature022  label="BL-LS0805UWC v3"
  Placement = pos=(26.5,0.0068546,-2.40685) rot=(-1,0,0;1.5708rad)
  shape: bbox 1.4 x 0.499 x 1.25 mm, 11 faces (baked)
FEATURE [Part::Feature] Part__Feature031  label="RES0805 v007"
  Placement = pos=(12.5,-1.605,-0.245) rot=(1,0,0;1.5708rad)
  shape: bbox 0.4 x 0.5 x 1.25 mm, 15 faces (baked)
FEATURE [Part::Feature] Part__Feature038  label="COMPOUND001"
  shape: bbox 33 x 1.6 x 10.1 mm, 24 faces (baked)
FEATURE [App::Part] Part057  label="TCST2103"
  Group = -> [Part__Feature045,Part__Feature033,Part__Feature030,Part__Feature024,Part__Feature028,Part__Feature029,Part__Feature026,Part__Feature027,Part__Feature025,Part__Feature031,Part__Feature032,Part__Feature039,Part__Feature041,Part__Feature023,Part__Feature034,Part__Feature037,Part__Feature035,Part__Feature018,Part__Feature022,Part__Feature020,Part__Feature021,Part__Feature019,Part__Feature036,+5 more]
  License = CC BY 3.0
  LicenseURL = http://creativecommons.org/licenses/by/3.0/
  Origin = -> Origin070
  Placement = pos=(2,161,31) rot=(0.57735,0.57735,0.57735;2.0944rad)
FEATURE [App::DocumentObjectGroup] Group  label="Electronics"
  Group = -> [Part007,Part012,Power_Inlet_with_Switch_STEP,Part056,Part057]
FEATURE [Part::Feature] Chamfer003008001001021  label="coupling-final001"
  shape: bbox 28.44 x 28.71 x 24.7 mm, 28 faces (baked)
FEATURE [Part::Cylinder] Cylinder012029001029  label="setscrew-body001"
  Angle = 360
  AttacherType = Attacher::AttachEngine3D
  Height = 6.2
  Radius = 1.95
FEATURE [Part::Feature] Chamfer003008001001022  label="setscrew-bottom-003"
  Placement = pos=(-3.54198,-1.28918,3.95) rot=(0.443713,0.633687,-0.633687;3.97682rad)
  shape: bbox 7.092 x 5.717 x 3.9 mm, 12 faces (baked)
FEATURE [Part::Cylinder] Cylinder012029001030  label="top-setscrew-2-cylinder002"
  Angle = 360
  AttacherType = Attacher::AttachEngine3D
  Height = 15
  Placement = pos=(0,0,20.8) rot=(0.37144,0.656518,0.656518;2.4303rad)
  Radius = 1.95
FEATURE [Sketcher::SketchObject] Sketch126  label="hexa-sketch001"
  MapMode = 5
  Placement = pos=(0,0,6.2) rot=(0,0,1;0rad)
  Support = -> [Cylinder012029001029]
  sketch-geometry (8):
    g0: LineSegment StartX=-1.1 StartY=-0.635085 StartZ=0 EndX=-1.1 EndY=0.635085 EndZ=0
    g1: LineSegment StartX=-1.1 StartY=0.635085 StartZ=0 EndX=0 EndY=1.27017 EndZ=0
    g2: LineSegment [constr] StartX=-1.1 StartY=0.635085 StartZ=0 EndX=0 EndY=1e-16 EndZ=0
    g3: LineSegment [constr] StartX=0 StartY=1.27017 StartZ=0 EndX=0 EndY=0 EndZ=0
    g4: LineSegment StartX=-1.1 StartY=-0.635085 StartZ=0 EndX=0 EndY=-1.27017 EndZ=0
    g5: LineSegment StartX=0 StartY=-1.27017 StartZ=0 EndX=1.1 EndY=-0.635085 EndZ=0
    g6: LineSegment StartX=1.1 StartY=-0.635085 StartZ=0 EndX=1.1 EndY=0.635085 EndZ=0
    g7: LineSegment StartX=1.1 StartY=0.635085 StartZ=0 EndX=0 EndY=1.27017 EndZ=0
  constraints (21):
    c: Vertical(g0)
    c: Coincident(g0,g1)
    c: Symmetric(g0,g0,g-1)
    c: Coincident(g2,g-1)
    c: Coincident(g2,g0)
    c: Angle(g-2,g2) = 1.0472
    c: Vertical(g3)
    c: Coincident(g3,g-1)
    c: Coincident(g3,g1)
    c: Equal(g3,g2)
    c: Coincident(g0,g4)
    c: PointOnObject(g4,g-2)
    c: Coincident(g4,g5)
    c: Coincident(g5,g6)
    c: Vertical(g6)
    c: Coincident(g6,g7)
    c: Coincident(g7,g1)
    c: Symmetric(g5,g6,g-1)
    c: Symmetric(g0,g6,g-2)
    c: Symmetric(g4,g1,g-1)
    c: DistanceX(g0,g6) = 2.2
FEATURE [Part::Cylinder] Cylinder012029001031  label="bottom-setscrew-2-cylinder001"
  Angle = 360
  AttacherType = Attacher::AttachEngine3D
  Height = 15
  Placement = pos=(0,0,3.95) rot=(0.443713,0.633687,0.633687;2.30637rad)
  Radius = 1.95
FEATURE [Part::Feature] Chamfer003008001001024  label="setscrew-bottom-004"
  Placement = pos=(0,3.9163,3.95) rot=(-1,0,0;1.5708rad)
  shape: bbox 3.9 x 6.2 x 3.9 mm, 12 faces (baked)
FEATURE [Sketcher::SketchObject] Sketch127  label="thread-section-sketch001"
  MapMode = 5
  Placement = pos=(0,0,0) rot=(1,0,0;1.5708rad)
  sketch-geometry (4):
    g0: LineSegment StartX=0 StartY=0 StartZ=0 EndX=10 EndY=0 EndZ=0
    g1: LineSegment StartX=10 StartY=0 StartZ=0 EndX=10 EndY=0.3 EndZ=0
    g2: LineSegment StartX=10 StartY=0.3 StartZ=0 EndX=0 EndY=0.3 EndZ=0
    g3: LineSegment StartX=0 StartY=0.3 StartZ=0 EndX=0 EndY=0 EndZ=0
  constraints (11):
    c: Coincident(g0,g1)
    c: Coincident(g1,g2)
    c: Coincident(g2,g3)
    c: Coincident(g3,g0)
    c: Horizontal(g0)
    c: Horizontal(g2)
    c: Vertical(g1)
    c: Vertical(g3)
    c: Coincident(g0,g-1)
    c: DistanceX(g2) = -10
    c: DistanceY(g1) = 0.3
FEATURE [Part::Feature] Chamfer003008001001025  label="setscrew-top-003"
  Placement = pos=(-0.399844,2.05702,20.85) rot=(-0.990855,-0.095409,0.095409;1.57998rad)
  shape: bbox 4.973 x 6.792 x 3.9 mm, 12 faces (baked)
FEATURE [Part::Cylinder] Cylinder012029001032  label="main-body002"
  Angle = 360
  AttacherType = Attacher::AttachEngine3D
  Height = 24.7
  Radius = 9.4
FEATURE [Part::Cylinder] Cylinder012029001033  label="vertical-5mm-drill-cylinder001"
  Angle = 360
  AttacherType = Attacher::AttachEngine3D
  Height = 30
  Placement = pos=(0,0,-3) rot=(0,0,1;0rad)
  Radius = 2.5
FEATURE [Part::Helix] Helix002  label="thread-path001"
  Angle = 0
  AttacherType = Attacher::AttachEngine3D
  Height = 9.1
  LocalCoord = 0
  Pitch = 1.5
  Radius = 10
  Style = 1
FEATURE [Part::Sweep] Sweep002  label="flexible-part-male001"
  Frenet = true
  Placement = pos=(0,0,7.35) rot=(0,0,1;0rad)
  Sections = -> [Sketch127]
  Solid = true
  Spine = -> Helix002 [Edge1]
  Transition = 1
FEATURE [Part::Cut] Cut003028  label="main-body-flexible-part001"
  Base = -> Cylinder012029001032
  Tool = -> Sweep002
FEATURE [Part::Cylinder] Cylinder012029001034  label="bottom-setscrew-1-cylinder001"
  Angle = 360
  AttacherType = Attacher::AttachEngine3D
  Height = 15
  Placement = pos=(0,0,3.95) rot=(1,0,0;1.5708rad)
  Radius = 1.95
FEATURE [Part::Cut] Cut003030  label="vertical-5mm-drill001"
  Base = -> Cut003028
  Tool = -> Cylinder012029001033
FEATURE [Part::Cylinder] Cylinder012029001035  label="vertical-drill-8mm-cylinder001"
  Angle = 360
  AttacherType = Attacher::AttachEngine3D
  Height = 17.6
  Placement = pos=(0,0,-1) rot=(0,0,1;0rad)
  Radius = 4
FEATURE [Part::Cut] Cut003027  label="vertical-8mm-drill001"
  Base = -> Cut003030
  Tool = -> Cylinder012029001035
FEATURE [PartDesign::Pocket] Pocket021005005019001001001001004002027  label="hexa001"
  Length = 3.2
  Length2 = 100
  Profile = -> Sketch126
  Type = 0
FEATURE [PartDesign::Chamfer] Chamfer003008001001019
  Base = -> Pocket021005005019001001001001004002027 [Edge3]
  Size = 0.1
FEATURE [Part::Feature] Chamfer003008001001026  label="setscrew-top-004"
  Placement = pos=(-1.79621,-1.07927,20.85) rot=(-0.363517,-0.657964,0.659499;2.43094rad)
  shape: bbox 7.303 x 6.582 x 4.01 mm, 12 faces (baked)
FEATURE [Part::Compound] Compound062001001003001001013  label="coupling-compound001"
  Links = -> [Chamfer003008001001024,Chamfer003008001001022,Chamfer003008001001025,Chamfer003008001001026,Chamfer003008001001021]
FEATURE [Part::Cylinder] Cylinder012029001036  label="top-setscrew-1-cylinder002"
  Angle = 360
  AttacherType = Attacher::AttachEngine3D
  Height = 15
  Placement = pos=(0,0,20.8) rot=(0.990855,0.095409,0.095409;1.57998rad)
  Radius = 1.95
FEATURE [Part::MultiFuse] Fusion001014  label="setscrew-cylinders001"
  Placement = pos=(0,0,0) rot=(0,0,1;3.14159rad)
  Shapes = -> [Cylinder012029001034,Cylinder012029001030,Cylinder012029001036,Cylinder012029001031]
FEATURE [Part::Cut] Cut003029  label="horizontal-drills001"
  Base = -> Cut003027
  Tool = -> Fusion001014
FEATURE [Part::Chamfer] Chamfer003008001001023
  Base = -> Cut003029
  Edges = 2 edges r=0.4: [Edge47,Edge70]
FEATURE [App::DocumentObjectGroup] Group030  label="coupling-src001"
  Group = -> [Chamfer003008001001023,Helix002]
FEATURE [PartDesign::Chamfer] Chamfer003008001001027
  Base = -> Chamfer003008001001019 [Edge3]
  Size = 0.1
FEATURE [App::DocumentObjectGroup] Group031  label="setscrew-src001"
  Group = -> [Cylinder012029001029,Pocket021005005019001001001001004002027,Chamfer003008001001019,Chamfer003008001001027]
FEATURE [App::Part] Part059  label="beam-coupling-5mm-8mm001"
  Group = -> [Chamfer003008001001019,Cylinder012029001029,Sketch126,Pocket021005005019001001001001004002027,Chamfer003008001001027,Group031,Fusion001014,Cut003027,Sweep002,Cylinder012029001030,Cylinder012029001031,Sketch127,Chamfer003008001001023,Cylinder012029001032,Cylinder012029001033,Helix002,Cut003029,Cut003028,Cylinder012029001034,Cut003030,Cylinder012029001035,Cylinder012029001036,Group030,+6 more]
  License = CC BY 3.0
  LicenseURL = http://creativecommons.org/licenses/by/3.0/
  Origin = -> Origin073
  Placement = pos=(0,133.5,360) rot=(0,0,1;0rad)
FEATURE [Part::Compound] Compound062001001003001001014  label="extruder-motor003"
  Placement = pos=(109.65,-100.5,-442) rot=(0,0,1;0rad)
FEATURE [Sketcher::SketchObject] Sketch128  label="bottom-part-sketch003"
  MapMode = 5
  sketch-geometry (8):
    g0: LineSegment StartX=-16.65 StartY=-21.15 StartZ=0 EndX=16.65 EndY=-21.15 EndZ=0
    g1: LineSegment StartX=21.15 StartY=-16.65 StartZ=0 EndX=21.15 EndY=16.65 EndZ=0
    g2: LineSegment StartX=16.65 StartY=21.15 StartZ=0 EndX=-16.65 EndY=21.15 EndZ=0
    g3: LineSegment StartX=-21.15 StartY=16.65 StartZ=0 EndX=-21.15 EndY=-16.65 EndZ=0
    g4: ArcOfCircle CenterX=0 CenterY=0 CenterZ=0 NormalX=0 NormalY=0 NormalZ=1 AngleXU=0 Radius=26.9174 StartAngle=2.2377 EndAngle=2.47468
    g5: ArcOfCircle CenterX=0 CenterY=0 CenterZ=0 NormalX=0 NormalY=0 NormalZ=1 AngleXU=0 Radius=26.9174 StartAngle=3.8085 EndAngle=4.04548
    g6: ArcOfCircle CenterX=0 CenterY=0 CenterZ=0 NormalX=0 NormalY=0 NormalZ=1 AngleXU=0 Radius=26.9174 StartAngle=5.3793 EndAngle=5.61628
    g7: ArcOfCircle CenterX=0 CenterY=0 CenterZ=0 NormalX=0 NormalY=0 NormalZ=1 AngleXU=0 Radius=26.9174 StartAngle=0.666908 EndAngle=0.903888
  constraints (29):
    c: Horizontal(g0)
    c: Horizontal(g2)
    c: Vertical(g1)
    c: Vertical(g3)
    c: PointOnObject(g0,g4)
    c: PointOnObject(g0,g4)
    c: PointOnObject(g1,g4)
    c: PointOnObject(g1,g4)
    c: Coincident(g4,g2)
    c: Coincident(g7,g2)
    c: Equal(g4,g5)
    c: Coincident(g4,g3)
    c: Coincident(g5,g3)
    c: Coincident(g4,g5)
    c: Equal(g5,g6)
    c: PointOnObject(g5,g0)
    c: PointOnObject(g6,g0)
    c: Coincident(g5,g6)
    c: Equal(g6,g7)
    c: PointOnObject(g6,g1)
    c: PointOnObject(g7,g1)
    c: Coincident(g6,g7)
    c: Equal(g3,g2)
    c: Equal(g2,g1)
    c: Equal(g1,g0)
    c: DistanceX(g3,g1) = 42.3
    c: DistanceX(g2) = -33.3
    c: DistanceY(g2) = 21.15
    c: DistanceX(g1) = 21.15
FEATURE [PartDesign::Pad] Pad002002021  label="bottom-slice003"
  Length = 9.6
  Length2 = 100
  Profile = -> Sketch128
  Type = 0
FEATURE [Sketcher::SketchObject] Sketch129  label="middle-part-sketch003"
  ExternalGeometry = -> [Pad002002021]
  MapMode = 5
  Placement = pos=(0,0,9.6) rot=(0,0,1;0rad)
  Support = -> [Pad002002021]
  sketch-geometry (9):
    g0: LineSegment StartX=-21 StartY=-13.75 StartZ=0 EndX=-21 EndY=13.75 EndZ=0
    g1: LineSegment StartX=-21 StartY=13.75 StartZ=0 EndX=-13.75 EndY=21 EndZ=0
    g2: LineSegment StartX=-13.75 StartY=21 StartZ=0 EndX=13.75 EndY=21 EndZ=0
    g3: LineSegment [constr] StartX=-21 StartY=13.75 StartZ=0 EndX=-9 EndY=13.75 EndZ=0
    g4: LineSegment StartX=13.75 StartY=21 StartZ=0 EndX=21 EndY=13.75 EndZ=0
    g5: LineSegment StartX=21 StartY=13.75 StartZ=0 EndX=21 EndY=-13.75 EndZ=0
    g6: LineSegment StartX=21 StartY=-13.75 StartZ=0 EndX=13.75 EndY=-21 EndZ=0
    g7: LineSegment StartX=13.75 StartY=-21 StartZ=0 EndX=-13.75 EndY=-21 EndZ=0
    g8: LineSegment StartX=-13.75 StartY=-21 StartZ=0 EndX=-21 EndY=-13.75 EndZ=0
  constraints (24):
    c: Coincident(g0,g1)
    c: Coincident(g1,g2)
    c: Horizontal(g2)
    c: Symmetric(g0,g0,g-1)
    c: Symmetric(g1,g2,g-2)
    c: Horizontal(g3)
    c: Coincident(g3,g0)
    c: DistanceX(g3) = 12
    c: Angle(g3,g1) = 0.785398
    c: DistanceY(g0) = 27.5
    c: Coincident(g4,g5)
    c: Vertical(g5)
    c: Coincident(g5,g6)
    c: Coincident(g6,g7)
    c: Horizontal(g7)
    c: Coincident(g7,g8)
    c: Coincident(g8,g0)
    c: Symmetric(g1,g7,g-1)
    c: Coincident(g4,g2)
    c: Symmetric(g4,g0,g-2)
    c: Symmetric(g0,g5,g-2)
    c: Symmetric(g6,g7,g-2)
    c: DistanceX(g-1,g0) = -21
    c: Equal(g0,g2)
FEATURE [PartDesign::Pad] Pad002002022  label="middle-slice003"
  Length = 22.75
  Length2 = 100
  Profile = -> Sketch129
  Type = 0
FEATURE [Sketcher::SketchObject] Sketch130  label="top-part-sketch003"
  MapMode = 5
  Placement = pos=(0,0,32.35) rot=(0,0,1;0rad)
  Support = -> [Pad002002022]
  sketch-geometry (8):
    g0: LineSegment StartX=-16.65 StartY=-21.15 StartZ=0 EndX=16.65 EndY=-21.15 EndZ=0
    g1: LineSegment StartX=21.15 StartY=-16.65 StartZ=0 EndX=21.15 EndY=16.65 EndZ=0
    g2: LineSegment StartX=16.65 StartY=21.15 StartZ=0 EndX=-16.65 EndY=21.15 EndZ=0
    g3: LineSegment StartX=-21.15 StartY=16.65 StartZ=0 EndX=-21.15 EndY=-16.65 EndZ=0
    g4: ArcOfCircle CenterX=0 CenterY=0 CenterZ=0 NormalX=0 NormalY=0 NormalZ=1 AngleXU=0 Radius=26.9174 StartAngle=2.2377 EndAngle=2.47468
    g5: ArcOfCircle CenterX=0 CenterY=0 CenterZ=0 NormalX=0 NormalY=0 NormalZ=1 AngleXU=0 Radius=26.9174 StartAngle=3.8085 EndAngle=4.04548
    g6: ArcOfCircle CenterX=0 CenterY=0 CenterZ=0 NormalX=0 NormalY=0 NormalZ=1 AngleXU=0 Radius=26.9174 StartAngle=5.3793 EndAngle=5.61628
    g7: ArcOfCircle CenterX=0 CenterY=0 CenterZ=0 NormalX=0 NormalY=0 NormalZ=1 AngleXU=0 Radius=26.9174 StartAngle=0.666908 EndAngle=0.903888
  constraints (29):
    c: Horizontal(g0)
    c: Horizontal(g2)
    c: Vertical(g1)
    c: Vertical(g3)
    c: PointOnObject(g0,g4)
    c: PointOnObject(g0,g4)
    c: PointOnObject(g1,g4)
    c: PointOnObject(g1,g4)
    c: Coincident(g4,g2)
    c: Coincident(g7,g2)
    c: Equal(g4,g5)
    c: Coincident(g4,g3)
    c: Coincident(g5,g3)
    c: Coincident(g4,g5)
    c: Equal(g5,g6)
    c: PointOnObject(g5,g0)
    c: PointOnObject(g6,g0)
    c: Coincident(g5,g6)
    c: Equal(g6,g7)
    c: PointOnObject(g6,g1)
    c: PointOnObject(g7,g1)
    c: Coincident(g6,g7)
    c: Equal(g3,g2)
    c: Equal(g2,g1)
    c: Equal(g1,g0)
    c: DistanceX(g3,g1) = 42.3
    c: DistanceX(g2) = -33.3
    c: DistanceY(g2) = 21.15
    c: DistanceX(g1) = 21.15
FEATURE [PartDesign::Pad] Pad002002023  label="top-slice003"
  Length = 7.75
  Length2 = 100
  Profile = -> Sketch130
  Type = 0
FEATURE [Sketcher::SketchObject] Sketch131  label="top-drills-sketch003"
  MapMode = 5
  Placement = pos=(0,0,40.1) rot=(0,0,1;0rad)
  Support = -> [Pad002002023]
  sketch-geometry (6):
    g0: LineSegment [constr] StartX=-15.5 StartY=15.5 StartZ=0 EndX=15.5 EndY=15.5 EndZ=0
    g1: LineSegment [constr] StartX=-15.5 StartY=15.5 StartZ=0 EndX=-15.5 EndY=-15.5 EndZ=0
    g2: Circle CenterX=-15.5 CenterY=15.5 CenterZ=0 NormalX=0 NormalY=0 NormalZ=1 AngleXU=0 Radius=1.225
    g3: Circle CenterX=15.5 CenterY=15.5 CenterZ=0 NormalX=0 NormalY=0 NormalZ=1 AngleXU=0 Radius=1.225
    g4: Circle CenterX=15.5 CenterY=-15.5 CenterZ=0 NormalX=0 NormalY=0 NormalZ=1 AngleXU=0 Radius=1.225
    g5: Circle CenterX=-15.5 CenterY=-15.5 CenterZ=0 NormalX=0 NormalY=0 NormalZ=1 AngleXU=0 Radius=1.225
  constraints (15):
    c: Horizontal(g0)
    c: Symmetric(g0,g0,g-2)
    c: Vertical(g1)
    c: Symmetric(g1,g1,g-1)
    c: Equal(g0,g1)
    c: DistanceX(g0) = 31
    c: Coincident(g1,g0)
    c: Radius(g2) = 1.225
    c: Coincident(g2,g0)
    c: Equal(g5,g4)
    c: Equal(g4,g3)
    c: Equal(g3,g2)
    c: Coincident(g3,g0)
    c: Coincident(g5,g1)
    c: Symmetric(g4,g1,g-2)
FEATURE [PartDesign::Pocket] Pocket021005005019001001001001004002028  label="top-drills003"
  Length = 4.5
  Length2 = 100
  Profile = -> Sketch131
  Type = 0
FEATURE [Sketcher::SketchObject] Sketch132  label="shaft-base-sketch003"
  MapMode = 5
  Placement = pos=(0,0,40.1) rot=(0,0,1;0rad)
  Support = -> [Pocket021005005019001001001001004002028]
  sketch-geometry (2):
    g0: Circle CenterX=0 CenterY=0 CenterZ=0 NormalX=0 NormalY=0 NormalZ=1 AngleXU=0 Radius=11
    g1: Circle CenterX=0 CenterY=0 CenterZ=0 NormalX=0 NormalY=0 NormalZ=1 AngleXU=0 Radius=5
  constraints (4):
    c: Coincident(g0,g-1)
    c: Radius(g0) = 11
    c: Coincident(g1,g-1)
    c: Radius(g1) = 5
FEATURE [PartDesign::Pad] Pad002002024  label="shaft-base003"
  Length = 2
  Length2 = 100
  Profile = -> Sketch132
  Type = 0
FEATURE [Sketcher::SketchObject] Sketch133  label="shaft-1-sketch003"
  MapMode = 5
  Placement = pos=(0,0,40.1) rot=(0,0,1;0rad)
  Support = -> [Pad002002024]
  sketch-geometry (1):
    g0: Circle CenterX=0 CenterY=0 CenterZ=0 NormalX=0 NormalY=0 NormalZ=1 AngleXU=0 Radius=2.5
  constraints (2):
    c: Coincident(g0,g-1)
    c: Radius(g0) = 2.5
FEATURE [PartDesign::Pad] Pad002002025  label="shaft-007"
  Length = 20
  Length2 = 100
  Profile = -> Sketch133
  Type = 0
FEATURE [Sketcher::SketchObject] Sketch134  label="shaft-2-sketch003"
  ExternalGeometry = -> [Pad002002025]
  MapMode = 5
  Placement = pos=(0,0,60.1) rot=(0,0,1;0rad)
  Support = -> [Pad002002025]
  sketch-geometry (4):
    g0: LineSegment StartX=-2 StartY=1.5 StartZ=0 EndX=-2 EndY=-1.5 EndZ=0
    g1: LineSegment StartX=-2 StartY=1.5 StartZ=0 EndX=-2.5 EndY=1.5 EndZ=0
    g2: LineSegment StartX=-2.5 StartY=1.5 StartZ=0 EndX=-2.5 EndY=-1.5 EndZ=0
    g3: LineSegment StartX=-2.5 StartY=-1.5 StartZ=0 EndX=-2 EndY=-1.5 EndZ=0
  constraints (12):
    c: Vertical(g0)
    c: Symmetric(g0,g0,g-1)
    c: PointOnObject(g0,g-3)
    c: Coincident(g1,g2)
    c: Coincident(g2,g3)
    c: Horizontal(g3)
    c: Horizontal(g1)
    c: Coincident(g1,g0)
    c: Coincident(g0,g3)
    c: Vertical(g2)
    c: Tangent(g2,g-3)
    c: DistanceX(g1) = -0.5
FEATURE [PartDesign::Pocket] Pocket021005005019001001001001004002029  label="shaft-008"
  Length = 17
  Length2 = 100
  Profile = -> Sketch134
  Type = 0
FEATURE [Sketcher::SketchObject] Sketch135  label="bottom-drills-sketch003"
  MapMode = 5
  Placement = pos=(0,0,0) rot=(1,0,0;3.14159rad)
  Support = -> [Pocket021005005019001001001001004002029]
  sketch-geometry (7):
    g0: LineSegment [constr] StartX=-15.5 StartY=15.5 StartZ=0 EndX=15.5 EndY=15.5 EndZ=0
    g1: LineSegment [constr] StartX=-15.5 StartY=15.5 StartZ=0 EndX=-15.5 EndY=-15.5 EndZ=0
    g2: Circle CenterX=-15.5 CenterY=15.5 CenterZ=0 NormalX=0 NormalY=0 NormalZ=1 AngleXU=0 Radius=1.5
    g3: Circle CenterX=15.5 CenterY=15.5 CenterZ=0 NormalX=0 NormalY=0 NormalZ=1 AngleXU=0 Radius=1.5
    g4: Circle CenterX=15.5 CenterY=-15.5 CenterZ=0 NormalX=0 NormalY=0 NormalZ=1 AngleXU=0 Radius=1.5
    g5: Circle CenterX=-15.5 CenterY=-15.5 CenterZ=0 NormalX=0 NormalY=0 NormalZ=1 AngleXU=0 Radius=1.5
    g6: Circle CenterX=0 CenterY=0 CenterZ=0 NormalX=0 NormalY=0 NormalZ=1 AngleXU=0 Radius=4.5
  constraints (17):
    c: Horizontal(g0)
    c: Vertical(g1)
    c: Coincident(g1,g0)
    c: Symmetric(g0,g0,g-2)
    c: Symmetric(g0,g1,g-1)
    c: Equal(g1,g0)
    c: DistanceX(g0) = 31
    c: Coincident(g2,g0)
    c: Radius(g2) = 1.5
    c: Coincident(g5,g1)
    c: Coincident(g0,g3)
    c: Equal(g3,g2)
    c: Equal(g2,g5)
    c: Equal(g5,g4)
    c: Symmetric(g4,g1,g-2)
    c: Coincident(g6,g-1)
    c: Radius(g6) = 4.5
FEATURE [PartDesign::Pocket] Pocket021005005019001001001001004002030  label="bottom-drills003"
  Length = 3
  Length2 = 100
  Profile = -> Sketch135
  Type = 0
FEATURE [Part::Chamfer] Chamfer003008001001020  label="motor-no-connector003"
  Base = -> Pocket021005005019001001001001004002030
  Edges = 1 edges r=0.4: [Edge102]
FEATURE [Sketcher::SketchObject] Sketch136  label="connector-support-sketch003"
  ExternalGeometry = -> [Chamfer003008001001020]
  MapMode = 5
  Placement = pos=(0,0,0) rot=(1,0,0;3.14159rad)
  Support = -> [Chamfer003008001001020]
  sketch-geometry (4):
    g0: LineSegment StartX=21.15 StartY=8.2 StartZ=0 EndX=25.45 EndY=8.2 EndZ=0
    g1: LineSegment StartX=25.45 StartY=8.2 StartZ=0 EndX=25.45 EndY=-8.2 EndZ=0
    g2: LineSegment StartX=25.45 StartY=-8.2 StartZ=0 EndX=21.15 EndY=-8.2 EndZ=0
    g3: LineSegment StartX=21.15 StartY=-8.2 StartZ=0 EndX=21.15 EndY=8.2 EndZ=0
  constraints (12):
    c: Coincident(g0,g1)
    c: Coincident(g1,g2)
    c: Coincident(g2,g3)
    c: Coincident(g3,g0)
    c: Horizontal(g0)
    c: Horizontal(g2)
    c: Vertical(g1)
    c: Vertical(g3)
    c: Symmetric(g0,g2,g-1)
    c: PointOnObject(g0,g-3)
    c: DistanceY(g1) = -16.4
    c: DistanceX(g0) = 4.3
FEATURE [PartDesign::Pad] Pad002002026  label="connector-motor003"
  Length = 3.6
  Length2 = 100
  Profile = -> Sketch136
  Reversed = true
  Type = 0
FEATURE [Sketcher::SketchObject] Sketch137  label="connector-slot-sketch003"
  ExternalGeometry = -> [Pad002002026]
  MapMode = 5
  Placement = pos=(21.15,0,0) rot=(0.57735,0.57735,0.57735;2.0944rad)
  Support = -> [Pad002002026]
  sketch-geometry (4):
    g0: LineSegment StartX=-8.2 StartY=9.6 StartZ=0 EndX=8.2 EndY=9.6 EndZ=0
    g1: LineSegment StartX=8.2 StartY=9.6 StartZ=0 EndX=8.2 EndY=3.6 EndZ=0
    g2: LineSegment StartX=8.2 StartY=3.6 StartZ=0 EndX=-8.2 EndY=3.6 EndZ=0
    g3: LineSegment StartX=-8.2 StartY=3.6 StartZ=0 EndX=-8.2 EndY=9.6 EndZ=0
  constraints (11):
    c: Coincident(g0,g1)
    c: Coincident(g1,g2)
    c: Coincident(g2,g3)
    c: Coincident(g3,g0)
    c: Horizontal(g0)
    c: Horizontal(g2)
    c: Vertical(g1)
    c: Vertical(g3)
    c: Coincident(g2,g-3)
    c: Coincident(g1,g-3)
    c: PointOnObject(g0,g-4)
FEATURE [PartDesign::Pocket] Pocket021005005019001001001001004002031  label="connector-slot003"
  Length = 1
  Length2 = 100
  Profile = -> Sketch137
  Type = 0
FEATURE [Sketcher::SketchObject] Sketch138  label="connector-main-body-sketch003"
  MapMode = 5
  Placement = pos=(0,0,0) rot=(0.57735,0.57735,0.57735;2.0944rad)
  sketch-geometry (4):
    g0: LineSegment StartX=-7.5 StartY=3.05 StartZ=0 EndX=7.5 EndY=3.05 EndZ=0
    g1: LineSegment StartX=7.5 StartY=3.05 StartZ=0 EndX=7.5 EndY=-3.05 EndZ=0
    g2: LineSegment StartX=7.5 StartY=-3.05 StartZ=0 EndX=-7.5 EndY=-3.05 EndZ=0
    g3: LineSegment StartX=-7.5 StartY=-3.05 StartZ=0 EndX=-7.5 EndY=3.05 EndZ=0
  constraints (11):
    c: Coincident(g0,g1)
    c: Coincident(g1,g2)
    c: Coincident(g2,g3)
    c: Coincident(g3,g0)
    c: Horizontal(g0)
    c: Horizontal(g2)
    c: Vertical(g1)
    c: Vertical(g3)
    c: Symmetric(g0,g1,g-1)
    c: DistanceX(g0) = 15
    c: DistanceY(g1) = -6.1
FEATURE [PartDesign::Pad] Pad002002027  label="connector-main-body003"
  Length = 6.7
  Length2 = 100
  Placement = pos=(0,0,0) rot=(0.57735,0.57735,0.57735;2.0944rad)
  Profile = -> Sketch138
  Type = 0
FEATURE [Sketcher::SketchObject] Sketch139  label="connector-cutout-1-sketch003"
  MapMode = 5
  Placement = pos=(6.7,0,0) rot=(0.57735,0.57735,0.57735;2.0944rad)
  Support = -> [Pad002002027]
  sketch-geometry (8):
    g0: LineSegment StartX=-6.5 StartY=1.85 StartZ=0 EndX=-3.22738 EndY=1.85 EndZ=0
    g1: LineSegment StartX=6.5 StartY=1.85 StartZ=0 EndX=6.5 EndY=-1.85 EndZ=0
    g2: LineSegment StartX=6.5 StartY=-1.85 StartZ=0 EndX=-6.5 EndY=-1.85 EndZ=0
    g3: LineSegment StartX=-6.5 StartY=-1.85 StartZ=0 EndX=-6.5 EndY=1.85 EndZ=0
    g4: LineSegment StartX=-3.22738 StartY=1.85 StartZ=0 EndX=-3.22738 EndY=3.85 EndZ=0
    g5: LineSegment StartX=-3.22738 StartY=3.85 StartZ=0 EndX=3.22738 EndY=3.85 EndZ=0
    g6: LineSegment StartX=3.22738 StartY=3.85 StartZ=0 EndX=3.22738 EndY=1.85 EndZ=0
    g7: LineSegment StartX=3.22738 StartY=1.85 StartZ=0 EndX=6.5 EndY=1.85 EndZ=0
  constraints (21):
    c: Coincident(g7,g1)
    c: Coincident(g1,g2)
    c: Coincident(g2,g3)
    c: Coincident(g3,g0)
    c: Horizontal(g0)
    c: Horizontal(g2)
    c: Vertical(g1)
    c: Vertical(g3)
    c: Symmetric(g0,g1,g-1)
    c: DistanceX(g2) = -13
    c: DistanceY(g1) = -3.7
    c: Vertical(g4)
    c: Coincident(g4,g5)
    c: Horizontal(g5)
    c: Coincident(g5,g6)
    c: Vertical(g6)
    c: Symmetric(g4,g5,g-2)
    c: Coincident(g0,g4)
    c: Coincident(g7,g6)
    c: Tangent(g0,g7)
    c: DistanceY(g6) = -2
FEATURE [PartDesign::Pocket] Pocket021005005019001001001001004002032  label="connector-cutout-004"
  Length = 4.6
  Length2 = 100
  Placement = pos=(0,0,0) rot=(0.57735,0.57735,0.57735;2.0944rad)
  Profile = -> Sketch139
  Type = 0
FEATURE [Part::Box] Box015001029  label="pin-master003"
  AttacherType = Attacher::AttachEngine3D
  Height = 0.5
  Length = 4
  Width = 0.5
FEATURE [Part::FeaturePython] Array003008004001001001002001001008  label="pins003"  # Draft array (typed FeaturePython)
  Angle = 360
  ArrayType = 0
  Axis = (0,0,1)
  Base = -> Box015001029
  Center = (0,0,0)
  IntervalX = (1,0,0)
  IntervalY = (0,2,0)
  IntervalZ = (0,0,1)
  NumberPolar = 1
  NumberX = 1
  NumberY = 6
  NumberZ = 1
  Placement = pos=(2,-5.3,0) rot=(0,0,1;0rad)
FEATURE [App::DocumentObjectGroup] Group032  label="connector-src003"
  Group = -> [Pad002002027,Pocket021005005019001001001001004002032,Array003008004001001001002001001008]
FEATURE [Part::MultiFuse] Fusion001015  label="connector003"
  Placement = pos=(20.15,1e-15,6.65) rot=(0,0,1;0rad)
  Shapes = -> [Pocket021005005019001001001001004002032,Array003008004001001001002001001008]
FEATURE [Part::MultiFuse] Fusion001016  label="Motor-with-connector003"
  Shapes = -> [Pocket021005005019001001001001004002031,Fusion001015]
FEATURE [Part::Feature] Fusion001017  label="Motor-with-connector-final003"
  Placement = pos=(11,133.5,428.4) rot=(0.707107,0.707107,0;3.14159rad)
  shape: bbox 42.3 x 48 x 60.1 mm, 110 faces (baked)
FEATURE [App::Part] Part061  label="Steppers_Z001"
  Group = -> [Compound062001001003001001014,Group032,Pad002002025,Fusion001015,Pocket021005005019001001001001004002029,Pocket021005005019001001001001004002031,Pad002002022,Box015001029,Pad002002024,Sketch135,Sketch136,Sketch132,Chamfer003008001001020,Pad002002026,Sketch131,Pad002002023,Pad002002021,Sketch139,Sketch137,Pad002002027,Sketch128,Sketch133,Sketch138,Sketch134,Pocket021005005019001001001001004002028,+7 more]
  License = CC BY 3.0
  LicenseURL = http://creativecommons.org/licenses/by/3.0/
  Origin = -> Origin074
FEATURE [Sketcher::SketchObject] Sketch140
  MapMode = 5
  sketch-geometry (9):
    g0: Circle [constr] CenterX=0 CenterY=0 CenterZ=0 NormalX=0 NormalY=0 NormalZ=1 AngleXU=0 Radius=3.95
    g1: LineSegment StartX=-3.90416 StartY=0.6 StartZ=0 EndX=-3.90416 EndY=-0.6 EndZ=0
    g2: LineSegment StartX=-3.90416 StartY=0.6 StartZ=0 EndX=-0.6 EndY=3.90416 EndZ=0
    g3: LineSegment StartX=-0.6 StartY=3.90416 StartZ=0 EndX=0.6 EndY=3.90416 EndZ=0
    g4: LineSegment StartX=0.6 StartY=3.90416 StartZ=0 EndX=3.90416 EndY=0.6 EndZ=0
    g5: LineSegment StartX=3.90416 StartY=0.6 StartZ=0 EndX=3.90416 EndY=-0.6 EndZ=0
    g6: LineSegment StartX=3.90416 StartY=-0.6 StartZ=0 EndX=0.6 EndY=-3.90416 EndZ=0
    g7: LineSegment StartX=0.6 StartY=-3.90416 StartZ=0 EndX=-0.6 EndY=-3.90416 EndZ=0
    g8: LineSegment StartX=-0.6 StartY=-3.90416 StartZ=0 EndX=-3.90416 EndY=-0.6 EndZ=0
  constraints (29):
    c: Coincident(g0,g-1)
    c: Radius(g0) = 3.95
    c: PointOnObject(g1,g0)
    c: PointOnObject(g1,g0)
    c: Vertical(g1)
    c: Coincident(g2,g1)
    c: PointOnObject(g2,g0)
    c: Coincident(g3,g2)
    c: PointOnObject(g3,g0)
    c: Horizontal(g3)
    c: Coincident(g3,g4)
    c: PointOnObject(g4,g0)
    c: Coincident(g4,g5)
    c: PointOnObject(g5,g0)
    c: Vertical(g5)
    c: Coincident(g5,g6)
    c: PointOnObject(g6,g0)
    c: Coincident(g6,g7)
    c: PointOnObject(g7,g0)
    c: Horizontal(g7)
    c: Coincident(g7,g8)
    c: Coincident(g8,g1)
    c: Equal(g3,g5)
    c: Equal(g5,g7)
    c: Equal(g7,g1)
    c: Equal(g2,g4)
    c: Equal(g4,g6)
    c: Equal(g6,g8)
    c: DistanceY(g5,g5) = 1.2
FEATURE [Part::Helix] Helix003
  Angle = 0
  AttacherType = Attacher::AttachEngine3D
  Height = 335
  LocalCoord = 0
  Pitch = 8
  Radius = 2
  Style = 1
FEATURE [Part::Sweep] Sweep003
  Frenet = true
  Sections = -> [Sketch140]
  Solid = true
  Spine = -> Helix003
  Transition = 1
FEATURE [Part::Cylinder] Cylinder012029001037
  Angle = 360
  AttacherType = Attacher::AttachEngine3D
  Height = 335
  Radius = 3.3
FEATURE [Part::MultiFuse] Fusion001018
  Shapes = -> [Cylinder012029001037,Sweep003]
FEATURE [App::Part] Part060  label="Thread001"
  Group = -> [Helix003,Sketch140,Cylinder012029001037,Sweep003,Fusion001018]
  License = CC BY 3.0
  LicenseURL = http://creativecommons.org/licenses/by/3.0/
  Origin = -> Origin072
  Placement = pos=(11,133.5,32) rot=(0,0,1;0rad)
FEATURE [Part::Feature] Part__Feature009022  label="SHF016"
  Placement = pos=(-6,0,0) rot=(0,0,1;0rad)
  shape: bbox 42 x 24 x 10 mm, 87 faces (baked)
FEATURE [Part::Feature] Part__Feature009023  label="SHF017"
  Placement = pos=(-8,0,0) rot=(0,0,1;0rad)
  shape: bbox 22.8 x 7.577 x 7.577 mm, 30 faces (baked)
FEATURE [App::Part] SHF012  label="SHF8_005"
  Group = -> [Part__Feature009022,Part__Feature009023]
  License = CC BY 3.0
  LicenseURL = http://creativecommons.org/licenses/by/3.0/
  Origin = -> Origin075
  Placement = pos=(0,44,25) rot=(0,0,-1;1.5708rad)
FEATURE [Part::Feature] Part__Feature009024  label="SHF018"
  Placement = pos=(-7,0,0) rot=(0,0,1;0rad)
  shape: bbox 22.8 x 7.577 x 7.577 mm, 30 faces (baked)
FEATURE [Part::Feature] Part__Feature009025  label="SHF019"
  Placement = pos=(-6,0,0) rot=(0,0,1;0rad)
  shape: bbox 42 x 24 x 10 mm, 87 faces (baked)
FEATURE [App::Part] SHF013  label="SHF8_006"
  Group = -> [Part__Feature009025,Part__Feature009024]
  License = CC BY 3.0
  LicenseURL = http://creativecommons.org/licenses/by/3.0/
  Origin = -> Origin076
  Placement = pos=(0,223,35) rot=(0.707107,0.707107,0;-3.14159rad)
FEATURE [Part::Feature] Part__Feature009026  label="SHF020"
  Placement = pos=(-7,0,0) rot=(0,0,1;0rad)
  shape: bbox 22.8 x 7.577 x 7.577 mm, 30 faces (baked)
FEATURE [Part::Feature] Part__Feature009027  label="SHF021"
  Placement = pos=(-6,0,0) rot=(0,0,1;0rad)
  shape: bbox 42 x 24 x 10 mm, 87 faces (baked)
FEATURE [App::Part] SHF014  label="SHF8_007"
  Group = -> [Part__Feature009027,Part__Feature009026]
  License = CC BY 3.0
  LicenseURL = http://creativecommons.org/licenses/by/3.0/
  Origin = -> Origin077
  Placement = pos=(0,223,430) rot=(0.707107,0.707107,0;-3.14159rad)
FEATURE [Part::Feature] Part__Feature009028  label="SHF022"
  Placement = pos=(-8,0,0) rot=(0,0,1;0rad)
  shape: bbox 22.8 x 7.577 x 7.577 mm, 30 faces (baked)
FEATURE [Part::Feature] Part__Feature009029  label="SHF023"
  Placement = pos=(-6,0,0) rot=(0,0,1;0rad)
  shape: bbox 42 x 24 x 10 mm, 87 faces (baked)
FEATURE [App::Part] SHF015  label="SHF8_008"
  Group = -> [Part__Feature009029,Part__Feature009028]
  License = CC BY 3.0
  LicenseURL = http://creativecommons.org/licenses/by/3.0/
  Origin = -> Origin078
  Placement = pos=(0,44,420) rot=(0,0,-1;1.5708rad)
FEATURE [Part::Cylinder] Cylinder012029001038
  Angle = 360
  AttacherType = Attacher::AttachEngine3D
  Height = 400
  Placement = pos=(0,50,28) rot=(0,0,1;0rad)
  Radius = 4
FEATURE [Part::Feature] Cylinder012029001039
  Placement = pos=(0,217,28) rot=(0,0,1;0rad)
  shape: bbox 8 x 8 x 400 mm, 3 faces (baked)
FEATURE [App::Part] Part063
  Group = -> [Cylinder012029001038,Cylinder012029001039]
  License = CC BY 3.0
  LicenseURL = http://creativecommons.org/licenses/by/3.0/
  Origin = -> Origin080
FEATURE [Part::FeaturePython] Screw005  label="M5x14-Screw001"  # Fasteners workbench fastener (typed FeaturePython)
  diameter = 6
  invert = false
  length = 3
  matchOuter = false
  offset = 0
  thread = false
  type = 15
FEATURE [Part::FeaturePython] Clone084  label="M5x14-Screw_009"  # Draft clone (typed FeaturePython)
  AttacherType = Attacher::AttachEngine3D
  Fuse = false
  Objects = -> [Screw005]
  Placement = pos=(0,6,0) rot=(0,0,1;0rad)
  Scale = (1,1,1)
FEATURE [Part::FeaturePython] Clone085  label="M5x14-Screw_010"  # Draft clone (typed FeaturePython)
  AttacherType = Attacher::AttachEngine3D
  Fuse = false
  Objects = -> [Screw005]
  Placement = pos=(0,173,0) rot=(0,0,1;0rad)
  Scale = (1,1,1)
FEATURE [Part::FeaturePython] Clone086  label="M5x14-Screw_011"  # Draft clone (typed FeaturePython)
  AttacherType = Attacher::AttachEngine3D
  Fuse = false
  Objects = -> [Screw005]
  Placement = pos=(0,205,0) rot=(0,0,1;0rad)
  Scale = (1,1,1)
FEATURE [Part::FeaturePython] Clone087  label="M5x14-Screw_012"  # Draft clone (typed FeaturePython)
  AttacherType = Attacher::AttachEngine3D
  Fuse = false
  Objects = -> [Screw005]
  Placement = pos=(0,205,385) rot=(0,1,0;3.14159rad)
  Scale = (1,1,1)
FEATURE [Part::FeaturePython] Clone088  label="M5x14-Screw_013"  # Draft clone (typed FeaturePython)
  AttacherType = Attacher::AttachEngine3D
  Fuse = false
  Objects = -> [Screw005]
  Placement = pos=(0,173,385) rot=(0,1,0;3.14159rad)
  Scale = (1,1,1)
FEATURE [Part::FeaturePython] Clone089  label="M5x14-Screw_014"  # Draft clone (typed FeaturePython)
  AttacherType = Attacher::AttachEngine3D
  Fuse = false
  Objects = -> [Screw005]
  Placement = pos=(0,38,0) rot=(0,0,1;0rad)
  Scale = (1,1,1)
FEATURE [Part::FeaturePython] Clone090  label="M5x14-Screw_015"  # Draft clone (typed FeaturePython)
  AttacherType = Attacher::AttachEngine3D
  Fuse = false
  Objects = -> [Screw005]
  Placement = pos=(0,37,385) rot=(0,1,0;3.14159rad)
  Scale = (1,1,1)
FEATURE [Part::FeaturePython] Clone091  label="M5x14-Screw_016"  # Draft clone (typed FeaturePython)
  AttacherType = Attacher::AttachEngine3D
  Fuse = false
  Objects = -> [Screw005]
  Placement = pos=(0,6,385) rot=(0,1,0;3.14159rad)
  Scale = (1,1,1)
FEATURE [App::Part] Part062
  Group = -> [Clone085,Screw005,Clone090,Clone089,Clone087,Clone088,Clone084,Clone086,Clone091]
  License = CC BY 3.0
  LicenseURL = http://creativecommons.org/licenses/by/3.0/
  Origin = -> Origin079
  Placement = pos=(0,28,35) rot=(0,0,1;0rad)
FEATURE [Part::Box] Box015001030  label="Cube026"
  AttacherType = Attacher::AttachEngine3D
  Height = 1.6
  Length = 40
  Placement = pos=(-20,105,429) rot=(0,0,1;0rad)
  Width = 57
FEATURE [App::Part] Part064  label="Rods_Left"
  Group = -> [Part063,Part059,Part060,Part061,SHF012,SHF013,SHF014,SHF015,Part062,Box015001030]
  Origin = -> Origin081
  Placement = pos=(-316,267,0) rot=(0,0,1;3.14159rad)
FEATURE [Part::Feature] Part__Feature009033  label="SC8LUU"
  Placement = pos=(58,12,19) rot=(0.707107,0,-0.707107;3.14159rad)
  shape: bbox 58 x 22 x 34 mm, 43 faces (baked)
FEATURE [Part::Cylinder] Cylinder012029001042  label="y_rod_left"
  Angle = 360
  AttacherType = Attacher::AttachEngine3D
  Height = 281
  Placement = pos=(-277,274,-14) rot=(1,0,0;1.5708rad)
  Radius = 4
FEATURE [Part::FeaturePython] Clone092  label="y_axis_SK8_left_front"  # WARN: FeaturePython — macro-defined, semantics opaque (R4)
  AttacherType = Attacher::AttachEngine3D
  Fuse = false
  Placement = pos=(-268,7,0) rot=(0,0.707107,-0.707107;3.14159rad)
  Scale = (1,1,1)
FEATURE [Part::FeaturePython] Clone093  label="y_axis_SK8_left_back"  # WARN: FeaturePython — macro-defined, semantics opaque (R4)
  AttacherType = Attacher::AttachEngine3D
  Fuse = false
  Placement = pos=(-268,274,0) rot=(0,0.707107,-0.707107;3.14159rad)
  Scale = (1,1,1)
FEATURE [Part::FeaturePython] Screw006  label="M3x10-Screw035"  # Fasteners workbench fastener (typed FeaturePython)
  Placement = pos=(9,4,4) rot=(0,1,0;3.14159rad)
  diameter = 4
  invert = false
  length = 3
  matchOuter = false
  offset = 0
  thread = false
  type = 15
FEATURE [Part::FeaturePython] Screw007  label="M3x10-Screw036"  # Fasteners workbench fastener (typed FeaturePython)
  Placement = pos=(9,55,4) rot=(0,1,0;3.14159rad)
  diameter = 4
  invert = false
  length = 3
  matchOuter = false
  offset = 0
  thread = false
  type = 15
FEATURE [Part::FeaturePython] Screw008  label="M3x30-Screw004"  # Fasteners workbench fastener (typed FeaturePython)
  Placement = pos=(4.5,14,6) rot=(0,1,0;0rad)
  diameter = 1
  invert = false
  length = 6
  matchOuter = false
  offset = 0
  thread = false
  type = 3
FEATURE [Part::FeaturePython] Screw009  label="M3x30-Screw005"  # Fasteners workbench fastener (typed FeaturePython)
  Placement = pos=(4.5,45,6) rot=(0,1,0;0rad)
  diameter = 1
  invert = false
  length = 6
  matchOuter = false
  offset = 0
  thread = false
  type = 3
FEATURE [Part::FeaturePython] Screw010  label="M3x30-Screw006"  # Fasteners workbench fastener (typed FeaturePython)
  Placement = pos=(35.5,14,6) rot=(0,1,0;0rad)
  diameter = 1
  invert = false
  length = 6
  matchOuter = false
  offset = 0
  thread = false
  type = 3
FEATURE [Part::FeaturePython] Screw011  label="M3x30-Screw"  # Fasteners workbench fastener (typed FeaturePython)
  Placement = pos=(35.5,45,6) rot=(0,1,0;0rad)
  diameter = 1
  invert = false
  length = 6
  matchOuter = false
  offset = 0
  thread = false
  type = 3
FEATURE [Part::Feature] Fillet004002001  label="Stepper_Z_Support_Right"
  shape: bbox 40 x 63 x 6 mm, 18 faces (baked)
FEATURE [App::Part] Part069  label="Support_Right"
  Group = -> [Screw006,Screw007,Screw008,Screw009,Screw010,Screw011,Fillet004002001]
  Origin = -> Origin088
  Placement = pos=(-9,104,424) rot=(0,0,1;0rad)
FEATURE [App::Part] Part058  label="Rods_Right"
  Group = -> [Part026,Part006,SHF8,SHF009,SHF010,SHF011,Part025,Part069,Compound061,Fusion001001]
  Origin = -> Origin071
FEATURE [App::Part] Part028  label="Rods"
  Group = -> [Part058,Part064]
  License = CC BY 3.0
  LicenseURL = http://creativecommons.org/licenses/by/3.0/
  Origin = -> Origin034
FEATURE [Part::Feature] Part__Feature009034  label="SC8UU"
  Placement = pos=(29,14,64) rot=(0,0,1;3.14159rad)
  shape: bbox 30 x 22 x 34 mm, 84 faces (baked)
FEATURE [Part::Box] Box015001037  label="Cube033"
  AttacherType = Attacher::AttachEngine3D
  Height = 80.5
  Length = 58
  Width = 3
FEATURE [Part::Box] Box015001038  label="Cube034"
  AttacherType = Attacher::AttachEngine3D
  Height = 3
  Length = 58
  Placement = pos=(0,-50.5,-3) rot=(0,0,1;0rad)
  Width = 53.5
FEATURE [Part::Box] Box015001039  label="Cube035"
  AttacherType = Attacher::AttachEngine3D
  Height = 15
  Length = 10
  Placement = pos=(-10,0,40.5) rot=(0,0,1;0rad)
  Width = 3
FEATURE [Part::Box] Box015001040  label="Cube036"
  AttacherType = Attacher::AttachEngine3D
  Height = 25
  Length = 14
  Placement = pos=(0,0,55.5) rot=(0,0,1;0rad)
  Width = 10
FEATURE [Part::Box] Box015001041  label="Cube037"
  AttacherType = Attacher::AttachEngine3D
  Height = 25
  Length = 14
  Placement = pos=(44,0,55.5) rot=(0,0,1;0rad)
  Width = 10
FEATURE [Part::Cut] Cut003047
  Base = -> Box015001037
  Tool = -> Box015001040
FEATURE [Part::Cut] Cut003048
  Base = -> Cut003047
  Tool = -> Box015001041
FEATURE [Part::MultiFuse] Fusion001019006
  Shapes = -> [Cut003048,Box015001039]
FEATURE [Part::MultiFuse] Fusion001019007
  Shapes = -> [Fusion001019006,Box015001038]
FEATURE [Part::Feature] Fusion001019007001  label="Fusion001019008"
  shape: bbox 68 x 53.5 x 83.5 mm, 14 faces (baked)
FEATURE [Part::Fillet] Fillet004002002
  Base = -> Fusion001019007001
  Edges = 9 edges r=2: [Edge2,Edge4,Edge9,Edge12,Edge14,Edge18,Edge26,Edge27,Edge33]
FEATURE [App::Part] Part071  label="Extruder_Carriage"
  Group = -> [Part__Feature009034,Part__Feature009033,Box015001037,Box015001038,Box015001039,Box015001040,Box015001041,Cut003047,Cut003048,Fusion001019006,Fusion001019007,Fusion001019007001,Fillet004002002]
  Origin = -> Origin090
  Placement = pos=(-288,250,-113) rot=(0,0,1;0rad)
FEATURE [Part::Cylinder] Cylinder012029001055  label="x_axis_up"
  Angle = 360
  AttacherType = Attacher::AttachEngine3D
  Height = 276
  Placement = pos=(0,0,0) rot=(0,1,0;1.5708rad)
  Radius = 4
FEATURE [Part::Cylinder] Cylinder012029001056  label="x_axis_down"
  Angle = 360
  AttacherType = Attacher::AttachEngine3D
  Height = 276
  Placement = pos=(0,0,-45) rot=(0,1,0;1.5708rad)
  Radius = 4
FEATURE [App::Part] Part072  label="x_rods001"
  Group = -> [Cylinder012029001055,Cylinder012029001056]
  Origin = -> Origin091
  Placement = pos=(-288,264,-49) rot=(0,0,1;0rad)
FEATURE [Part::Feature] Part__Feature009035  label="y_carriage_SC8LUU_left"
  Placement = pos=(-279,260,-14) rot=(0.57735,-0.57735,0.57735;2.0944rad)
  shape: bbox 22 x 58 x 34 mm, 43 faces (baked)
FEATURE [Part::Box] Box015001042  label="Cube038"
  AttacherType = Attacher::AttachEngine3D
  Height = 100
  Length = 3
  Placement = pos=(-279,0,0) rot=(0,0,1;0rad)
  Width = 58
FEATURE [Part::Box] Box015001044  label="Cube040"
  AttacherType = Attacher::AttachEngine3D
  Height = 106
  Length = 3
  Placement = pos=(-279,34,-16) rot=(0,0,1;0rad)
  Width = 39
FEATURE [Part::Box] Box015001045  label="Cube041"
  AttacherType = Attacher::AttachEngine3D
  Height = 27
  Length = 3
  Placement = pos=(-279,84,71) rot=(1,0,0;0.785398rad)
  Width = 12
FEATURE [Part::Box] Box015001046  label="Cube042"
  AttacherType = Attacher::AttachEngine3D
  Height = 76
  Length = 3
  Placement = pos=(-279,33,-35) rot=(1,0,0;0.785398rad)
  Width = 26
FEATURE [Part::MultiFuse] Fusion001019007002
  Shapes = -> [Box015001042,Box015001044]
FEATURE [Part::Cut] Cut003049
  Base = -> Fusion001019007002
  Tool = -> Box015001046
FEATURE [Part::Cylinder] Cylinder012029001057  label="Cylinder012029001047"
  Angle = 360
  AttacherType = Attacher::AttachEngine3D
  Height = 3
  Placement = pos=(-279,49.5,32) rot=(0,1,0;1.5708rad)
  Radius = 10
FEATURE [Part::Cut] Cut003050
  Base = -> Cut003049
  Tool = -> Box015001045
FEATURE [Part::Cut] Cut003051
  Base = -> Cut003050
  Tool = -> Cylinder012029001057
FEATURE [Part::Fillet] Fillet004002003
  Base = -> Cut003051
  Edges = 6 edges r=2: [Edge9,Edge19,Edge21,Edge28,Edge44,Edge45]
FEATURE [Part::Feature] Fillet004002003001  label="Fillet004002004"
  shape: bbox 3 x 73 x 116 mm, 17 faces (baked)
FEATURE [App::Part] Part073
  Group = -> [Box015001042,Box015001044,Box015001045,Box015001046,Fusion001019007002,Cut003049,Cut003050,Cylinder012029001057,Cut003051,Fillet004002003,Fillet004002003001]
  Origin = -> Origin092
  Placement = pos=(-12,202,-97) rot=(0,0,1;0rad)
FEATURE [App::Part] Part068  label="y_carriage"
  Group = -> [Part__Feature009008,Part__Feature009035,Part072,Part071,Part073]
  Origin = -> Origin087
FEATURE [Part::FeaturePython] Screw018  label="M5x10-Screw"  # Fasteners workbench fastener (typed FeaturePython)
  Placement = pos=(-292.75,0,0) rot=(1,0,0;3.14159rad)
  diameter = 6
  invert = false
  length = 1
  matchOuter = false
  offset = 0
  thread = false
  type = 15
FEATURE [App::DocumentObjectGroup] Group033  label="y_axis_rods"
  Group = -> [Cylinder012029001016,Clone004,Shape,Clone005,Cylinder012029001042,Clone092,Clone093,Screw018]
FEATURE [App::Part] Part066  label="y_axis"
  Group = -> [Cylinder012029001016,Clone004,Shape,Clone005,Cylinder012029001042,Clone092,Clone093,Group033,Part068,Screw018]
  Origin = -> Origin085
  Placement = pos=(-8,0,-26) rot=(0,0,1;0rad)
FEATURE [App::Part] Part034  label="CoreXY_"
  Group = -> [Part048,Part066]
  License = CC BY 3.0
  LicenseURL = http://creativecommons.org/licenses/by/3.0/
  Origin = -> Origin041
  Placement = pos=(0,0,450) rot=(0,0,1;0rad)
FEATURE [App::DocumentObjectGroup] Group036  label="CoreXY"
  Group = -> [Part034]
FEATURE [Part::Cylinder] Cylinder012029001058
  Angle = 360
  AttacherType = Attacher::AttachEngine3D
  Height = 6
  Placement = pos=(21.63,233.64,-2) rot=(0,0,1;0rad)
  Radius = 1.75
FEATURE [Part::Box] Box015001047  label="Cube043"
  AttacherType = Attacher::AttachEngine3D
  Height = 2
  Length = 230
  Width = 30
FEATURE [Part::Fillet] Fillet004002003002
  Base = -> Box015001047
  Edges = 4 edges r=2: [Edge1,Edge3,Edge5,Edge7]
  Placement = pos=(11,110.55,-1) rot=(0,0,1;0rad)
FEATURE [Part::Cylinder] Cylinder012029001059
  Angle = 360
  AttacherType = Attacher::AttachEngine3D
  Height = 2
  Placement = pos=(21.63,233.64,-2) rot=(0,0,1;0rad)
  Radius = 6.88
FEATURE [Part::Box] Box015001048  label="Cube044"
  AttacherType = Attacher::AttachEngine3D
  Height = 14.95
  Length = 50
  Placement = pos=(0,0,3.75) rot=(0,0,1;0rad)
  Width = 246
FEATURE [Part::Box] Box015001049  label="Cube001"
  AttacherType = Attacher::AttachEngine3D
  Height = 3.75
  Length = 50
  Width = 246
FEATURE [Part::Cylinder] Cylinder012029001060
  Angle = 360
  AttacherType = Attacher::AttachEngine3D
  Height = 6
  Placement = pos=(21.63,26.63,-2) rot=(0,0,1;0rad)
  Radius = 1.75
FEATURE [Part::Box] Box015001050  label="Cube003"
  AttacherType = Attacher::AttachEngine3D
  Height = 14.95
  Length = 37.15
  Placement = pos=(12.85,0,3.75) rot=(0,0,1;0rad)
  Width = 242.75
FEATURE [Part::Cut] Cut003052
  Base = -> Box015001048
  Tool = -> Box015001050
FEATURE [Part::Box] Box015001051  label="Cube045"
  AttacherType = Attacher::AttachEngine3D
  Height = 28
  Length = 20
  Placement = pos=(0,-14.1422,17.8921) rot=(-1,0,0;0.785398rad)
  Width = 20
FEATURE [Part::Cut] Cut003053
  Base = -> Cut003052
  Tool = -> Box015001051
FEATURE [Part::MultiFuse] Fusion001019007005
  Shapes = -> [Box015001049,Cut003053]
FEATURE [Part::Cylinder] Cylinder012029001061
  Angle = 360
  AttacherType = Attacher::AttachEngine3D
  Height = 2
  Placement = pos=(21.63,26.63,-2) rot=(0,0,1;0rad)
  Radius = 6.88
FEATURE [Part::MultiFuse] Fusion001019007004
  Shapes = -> [Cylinder012029001061,Fusion001019007005]
FEATURE [Part::Cut] Cut003054
  Base = -> Fusion001019007004
  Tool = -> Cylinder012029001060
FEATURE [Part::MultiFuse] Fusion001019007003
  Shapes = -> [Cut003054,Cylinder012029001059]
FEATURE [Part::Cut] Cut003
  Base = -> Fusion001019007003
  Tool = -> Cylinder012029001058
FEATURE [Part::Mirroring] Part__Mirroring  label="Cut003 (Mirror #1)"
  Base = (126,0,0)
  Normal = (1,0,0)
  Source = -> Cut003
FEATURE [App::Part] Part074  label="Anet_A8_removable_heat_bed_support"
  Group = -> [Cut003052,Cut003053,Fusion001019007003,Cylinder012029001058,Cut003,Cut003054,Cylinder012029001059,Box015001048,Box015001049,Cylinder012029001060,Box015001050,Fusion001019007004,Fusion001019007005,Box015001051,Cylinder012029001061,Part__Mirroring,Box015001047,Fillet004002003002]
  Origin = -> Origin093
  Placement = pos=(54,0,4) rot=(0,0,1;0rad)
FEATURE [App::Part] Part076  label="Carriage_right_Screews"
  Group = -> [Part033,Part049]
  Origin = -> Origin095
FEATURE [App::Part] Part078  label="TR8_right_Nuts"
  Group = -> [Compound062001001003,Compound062001001003001,Compound062001001003001001,Compound062001001003001001001]
  Origin = -> Origin097
FEATURE [App::Part] Part079  label="LMH8UU_right_Nuts"
  Group = -> [Compound062001,Compound062001001,Compound062001001001,Compound062001001002]
  Origin = -> Origin098
FEATURE [App::Part] Part077  label="Carriage_right_Nuts"
  Group = -> [Part078,Part079]
  Origin = -> Origin096
  Placement = pos=(0,0,-7) rot=(0,0,1;0rad)
FEATURE [App::Part] Part031  label="Carriage_right_Fasteners"
  Group = -> [Part076,Part077]
  License = CC BY 3.0
  LicenseURL = http://creativecommons.org/licenses/by/3.0/
  Origin = -> Origin037
  Placement = pos=(338,19,7) rot=(0,0,1;0rad)
FEATURE [Part::FeaturePython] Clone014003  label="LMH8UU_004"  # Draft clone (typed FeaturePython)
  AttacherType = Attacher::AttachEngine3D
  Fuse = false
  Objects = -> [Clone]
  Placement = pos=(336,218,0) rot=(-1,0,0;1.5708rad)
  Scale = (1,1,1)
FEATURE [Part::FeaturePython] Clone014004  label="LMH8UU_003"  # Draft clone (typed FeaturePython)
  AttacherType = Attacher::AttachEngine3D
  Fuse = false
  Objects = -> [Part__Feature009]
  Placement = pos=(336,51,0) rot=(-1,0,0;1.5708rad)
  Scale = (1,1,1)
FEATURE [App::Part] Part080  label="LMH8UU"
  Group = -> [Part__Feature009,Clone001,Clone014003,Clone014004,Clone]
  Origin = -> Origin099
  Placement = pos=(2,-14,7) rot=(0,0,1;0rad)
FEATURE [Part::Feature] Part__Feature009036  label="nakretka tr009"
  Placement = pos=(0,0,0) rot=(-1,0,0;1.5708rad)
  shape: bbox 21.75 x 21.75 x 14.8 mm, 17 faces (baked)
FEATURE [Part::Feature] Part__Feature009037  label="napinacz nakretki tr009"
  Placement = pos=(0,0,23.8) rot=(0,0.707107,-0.707107;3.14159rad)
  shape: bbox 13.75 x 13.75 x 15 mm, 13 faces (baked)
FEATURE [Part::Feature] Part__Feature009038  label="sprezyna nakretka tr 009"
  Placement = pos=(0,0,1.3) rot=(0,0,1;0rad)
  shape: bbox 11.8 x 11.79 x 19.8 mm, 5 faces (baked)
FEATURE [App::Part] TR009  label="TR08_002"
  Group = -> [Part__Feature009036,Part__Feature009037,Part__Feature009038]
  License = CC BY 3.0
  LicenseURL = http://creativecommons.org/licenses/by/3.0/
  Origin = -> Origin100
  Placement = pos=(349,120.5,2) rot=(1,0,0;-3.14159rad)
FEATURE [Part::Feature] Compound062001001003001001016  label="Nyloc-nut-M-017"
  Placement = pos=(0,6,0) rot=(0,1,0;3.14159rad)
  shape: bbox 6.35 x 6.35 x 3.86 mm, 36 faces, 2 solids (baked)
FEATURE [Part::Feature] Compound062001001003001001017  label="Nyloc-nut-M-018"
  Placement = pos=(0,30,0) rot=(0,1,0;3.14159rad)
  shape: bbox 6.35 x 6.35 x 3.86 mm, 36 faces, 2 solids (baked)
FEATURE [Part::Feature] Compound062001001003001001018  label="Nyloc-nut-M-019"
  Placement = pos=(0,173,0) rot=(0,1,0;3.14159rad)
  shape: bbox 6.35 x 6.35 x 3.86 mm, 36 faces, 2 solids (baked)
FEATURE [Part::Feature] Compound062001001003001001019  label="Nyloc-nut-M-020"
  Placement = pos=(0,197,0) rot=(0,1,0;3.14159rad)
  shape: bbox 6.35 x 6.35 x 3.86 mm, 36 faces, 2 solids (baked)
FEATURE [Part::Feature] Compound062001001003001001020  label="Nyloc-nut-M-021"
  Placement = pos=(11,93.5,0) rot=(0.965926,0.258819,0;3.14159rad)
  shape: bbox 6.35 x 6.35 x 3.86 mm, 36 faces, 2 solids (baked)
FEATURE [Part::Feature] Compound062001001003001001021  label="Nyloc-nut-M-022"
  Placement = pos=(11,109.5,0) rot=(0.965926,0.258819,0;3.14159rad)
  shape: bbox 6.35 x 6.35 x 3.86 mm, 36 faces, 2 solids (baked)
FEATURE [Part::Feature] Compound062001001003001001022  label="Nyloc-nut-M-023"
  Placement = pos=(19,101.5,0) rot=(1,0,0;3.14159rad)
  shape: bbox 6.35 x 6.35 x 3.86 mm, 36 faces, 2 solids (baked)
FEATURE [Part::Feature] Compound062001001003001001023  label="Nyloc-nut-M-024"
  Placement = pos=(3,101.5,0) rot=(1,0,0;3.14159rad)
  shape: bbox 6.35 x 6.35 x 3.86 mm, 36 faces, 2 solids (baked)
FEATURE [Part::FeaturePython] Screw019  label="M3x12-Screw002"  # Fasteners workbench fastener (typed FeaturePython)
  diameter = 4
  invert = false
  length = 4
  matchOuter = false
  offset = 0
  thread = false
  type = 15
FEATURE [Part::FeaturePython] Clone014005  label="M3x10-Screw_009"  # Draft clone (typed FeaturePython)
  AttacherType = Attacher::AttachEngine3D
  Fuse = false
  Objects = -> [Screw019]
  Placement = pos=(11,0,0) rot=(0,0,1;0rad)
  Scale = (1,1,1)
FEATURE [Part::FeaturePython] Clone014006  label="M3x10-Screw_010"  # Draft clone (typed FeaturePython)
  AttacherType = Attacher::AttachEngine3D
  Fuse = false
  Objects = -> [Screw019]
  Placement = pos=(11,16,0) rot=(0,0,1;0rad)
  Scale = (1,1,1)
FEATURE [Part::FeaturePython] Clone014007  label="M3x10-Screw_011"  # Draft clone (typed FeaturePython)
  AttacherType = Attacher::AttachEngine3D
  Fuse = false
  Objects = -> [Screw019]
  Placement = pos=(19,8,0) rot=(0,0,1;0rad)
  Scale = (1,1,1)
FEATURE [Part::FeaturePython] Clone014008  label="M3x10-Screw_012"  # Draft clone (typed FeaturePython)
  AttacherType = Attacher::AttachEngine3D
  Fuse = false
  Objects = -> [Screw019]
  Placement = pos=(3,8,0) rot=(0,0,1;0rad)
  Scale = (1,1,1)
FEATURE [App::Part] Part082  label="TR8_left_Screews"
  Group = -> [Clone014006,Clone014005,Screw019,Clone014007,Clone014008]
  License = CC BY 3.0
  LicenseURL = http://creativecommons.org/licenses/by/3.0/
  Origin = -> Origin102
  Placement = pos=(-22,93.5,-1) rot=(0,0,1;0rad)
FEATURE [Part::FeaturePython] Screw020  label="M3x10-Screw037"  # Fasteners workbench fastener (typed FeaturePython)
  diameter = 4
  invert = false
  length = 3
  matchOuter = false
  offset = 0
  thread = false
  type = 15
FEATURE [Part::FeaturePython] Clone014009  label="M3x8-Screw_009"  # Draft clone (typed FeaturePython)
  AttacherType = Attacher::AttachEngine3D
  Fuse = false
  Objects = -> [Screw020]
  Placement = pos=(0,6,0) rot=(0,0,1;0rad)
  Scale = (1,1,1)
FEATURE [Part::FeaturePython] Clone014010  label="M3x8-Screw_010"  # Draft clone (typed FeaturePython)
  AttacherType = Attacher::AttachEngine3D
  Fuse = false
  Objects = -> [Screw020]
  Placement = pos=(0,30,0) rot=(0,0,1;0rad)
  Scale = (1,1,1)
FEATURE [Part::FeaturePython] Clone014011  label="M3x8-Screw_011"  # Draft clone (typed FeaturePython)
  AttacherType = Attacher::AttachEngine3D
  Fuse = false
  Objects = -> [Screw020]
  Placement = pos=(0,173,0) rot=(0,0,1;0rad)
  Scale = (1,1,1)
FEATURE [Part::FeaturePython] Clone014012  label="M3x8-Screw_012"  # Draft clone (typed FeaturePython)
  AttacherType = Attacher::AttachEngine3D
  Fuse = false
  Objects = -> [Screw020]
  Placement = pos=(0,197,0) rot=(0,0,1;0rad)
  Scale = (1,1,1)
FEATURE [App::Part] Part083  label="LMH8UU_left_Screews"
  Group = -> [Clone014011,Clone014010,Clone014012,Screw020,Clone014009]
  License = CC BY 3.0
  LicenseURL = http://creativecommons.org/licenses/by/3.0/
  Origin = -> Origin103
  Placement = pos=(0,0,-3) rot=(0,0,1;0rad)
FEATURE [App::Part] Part084  label="Carriage_left_Screews"
  Group = -> [Part082,Part083]
  Origin = -> Origin106
FEATURE [App::Part] Part085  label="TR8_left_Nuts"
  Group = -> [Compound062001001003001001020,Compound062001001003001001021,Compound062001001003001001022,Compound062001001003001001023]
  Origin = -> Origin104
  Placement = pos=(-22,0,0) rot=(0,0,1;0rad)
FEATURE [App::Part] Part087  label="LMH8UU_left_Nuts"
  Group = -> [Compound062001001003001001016,Compound062001001003001001017,Compound062001001003001001018,Compound062001001003001001019]
  Origin = -> Origin107
FEATURE [App::Part] Part086  label="Carriage_left_Nuts"
  Group = -> [Part085,Part087]
  Origin = -> Origin105
  Placement = pos=(0,0,-7) rot=(0,0,1;0rad)
FEATURE [App::Part] Part081  label="Carriage_left_Fasteners"
  Group = -> [Part084,Part086]
  License = CC BY 3.0
  LicenseURL = http://creativecommons.org/licenses/by/3.0/
  Origin = -> Origin101
  Placement = pos=(22,19,7) rot=(0,0,1;0rad)
FEATURE [Part::Box] Box015001052  label="Carriage_frame_basic"
  AttacherType = Attacher::AttachEngine3D
  Height = 4
  Length = 368
  Placement = pos=(-4,0,0) rot=(0,0,1;0rad)
  Width = 241
FEATURE [Part::Cylinder] Cylinder012029001062  label="Cylinder012029001066"
  Angle = 360
  AttacherType = Attacher::AttachEngine3D
  Height = 10
  Placement = pos=(338,204,-1) rot=(0,0,1;0rad)
  Radius = 7.6
FEATURE [Part::Cylinder] Cylinder012029001063
  Angle = 360
  AttacherType = Attacher::AttachEngine3D
  Height = 10
  Placement = pos=(22,204,-1) rot=(0,0,1;0rad)
  Radius = 7.6
FEATURE [Part::Cylinder] Cylinder012029001064
  Angle = 360
  AttacherType = Attacher::AttachEngine3D
  Height = 10
  Placement = pos=(22,37,-1) rot=(0,0,1;0rad)
  Radius = 7.6
FEATURE [Part::Cut] Cut003058
  Base = -> Box015001052
  Tool = -> Cylinder012029001064
FEATURE [Part::Cut] Cut003055
  Base = -> Cut003058
  Tool = -> Cylinder012029001063
FEATURE [Part::Cylinder] Cylinder012029001065
  Angle = 360
  AttacherType = Attacher::AttachEngine3D
  Height = 10
  Placement = pos=(338,37,-1) rot=(0,0,1;0rad)
  Radius = 7.6
FEATURE [Part::Cut] Cut003057
  Base = -> Cut003055
  Tool = -> Cylinder012029001065
FEATURE [Part::Cut] Cut003056
  Base = -> Cut003057
  Tool = -> Cylinder012029001062
FEATURE [Part::Cylinder] Cylinder012029001066  label="Cylinder012029001067"
  Angle = 360
  AttacherType = Attacher::AttachEngine3D
  Height = 10
  Placement = pos=(22,25,-1) rot=(0,0,1;0rad)
  Radius = 1.6
FEATURE [Part::Cut] Cut004
  Base = -> Cut003056
  Tool = -> Cylinder012029001066
FEATURE [Part::Cylinder] Cylinder012029001067  label="Cylinder012029001068"
  Angle = 360
  AttacherType = Attacher::AttachEngine3D
  Height = 10
  Placement = pos=(22,49,-1) rot=(0,0,1;0rad)
  Radius = 1.6
FEATURE [Part::Cut] Cut005
  Base = -> Cut004
  Tool = -> Cylinder012029001067
FEATURE [Part::Cylinder] Cylinder012029001068  label="Cylinder012029001069"
  Angle = 360
  AttacherType = Attacher::AttachEngine3D
  Height = 10
  Placement = pos=(22,192,-1) rot=(0,0,1;0rad)
  Radius = 1.6
FEATURE [Part::Cut] Cut006
  Base = -> Cut005
  Tool = -> Cylinder012029001068
FEATURE [Part::Cylinder] Cylinder012029001069  label="Cylinder012029001070"
  Angle = 360
  AttacherType = Attacher::AttachEngine3D
  Height = 10
  Placement = pos=(22,216,-1) rot=(0,0,1;0rad)
  Radius = 1.6
FEATURE [Part::Cylinder] Cylinder012029001070  label="Cylinder012029001071"
  Angle = 360
  AttacherType = Attacher::AttachEngine3D
  Height = 10
  Placement = pos=(11,112.5,-1) rot=(0,0,1;0rad)
  Radius = 1.6
FEATURE [Part::Cylinder] Cylinder012029001071  label="Cylinder012029001072"
  Angle = 360
  AttacherType = Attacher::AttachEngine3D
  Height = 10
  Placement = pos=(19,120.5,-1) rot=(0,0,1;0rad)
  Radius = 1.6
FEATURE [Part::Cylinder] Cylinder012029001072  label="Cylinder012029001073"
  Angle = 360
  AttacherType = Attacher::AttachEngine3D
  Height = 10
  Placement = pos=(11,128.5,-1) rot=(0,0,1;0rad)
  Radius = 1.6
FEATURE [Part::Cylinder] Cylinder012029001073  label="Cylinder012029001074"
  Angle = 360
  AttacherType = Attacher::AttachEngine3D
  Height = 10
  Placement = pos=(3,120.5,-1) rot=(0,0,1;0rad)
  Radius = 1.6
FEATURE [Part::Cylinder] Cylinder012029001074  label="Cylinder012029001075"
  Angle = 360
  AttacherType = Attacher::AttachEngine3D
  Height = 10
  Placement = pos=(11,120.5,-1) rot=(0,0,1;0rad)
  Radius = 5.6
FEATURE [Part::Cut] Cut007
  Base = -> Cut006
  Tool = -> Cylinder012029001074
FEATURE [Part::Cut] Cut008
  Base = -> Cut007
  Tool = -> Cylinder012029001073
FEATURE [Part::Cylinder] Cylinder013  label="Cylinder012029001076"
  Angle = 360
  AttacherType = Attacher::AttachEngine3D
  Height = 10
  Placement = pos=(349,120.5,-1) rot=(0,0,1;0rad)
  Radius = 5.6
FEATURE [Part::Cylinder] Cylinder014  label="Cylinder012029001077"
  Angle = 360
  AttacherType = Attacher::AttachEngine3D
  Height = 10
  Placement = pos=(341,120.5,-1) rot=(0,0,1;0rad)
  Radius = 1.6
FEATURE [Part::Cut] Cut009
  Base = -> Cut008
  Tool = -> Cylinder012029001072
FEATURE [Part::Cut] Cut010
  Base = -> Cut009
  Tool = -> Cylinder012029001071
FEATURE [Part::Cut] Cut011
  Base = -> Cut010
  Tool = -> Cylinder012029001070
FEATURE [Part::Cut] Cut012
  Base = -> Cut011
  Tool = -> Cylinder012029001069
FEATURE [Part::Cylinder] Cylinder016  label="Cylinder012029001078"
  Angle = 360
  AttacherType = Attacher::AttachEngine3D
  Height = 10
  Placement = pos=(349,112.5,-1) rot=(0,0,1;0rad)
  Radius = 1.6
FEATURE [Part::Cylinder] Cylinder017  label="Cylinder018"
  Angle = 360
  AttacherType = Attacher::AttachEngine3D
  Height = 10
  Placement = pos=(349,128.5,-1) rot=(0,0,1;0rad)
  Radius = 1.6
FEATURE [Part::Cylinder] Cylinder018  label="Cylinder019"
  Angle = 360
  AttacherType = Attacher::AttachEngine3D
  Height = 10
  Placement = pos=(338,216,-1) rot=(0,0,1;0rad)
  Radius = 1.6
FEATURE [Part::Cylinder] Cylinder015  label="Cylinder012029001079"
  Angle = 360
  AttacherType = Attacher::AttachEngine3D
  Height = 10
  Placement = pos=(357,120.5,-1) rot=(0,0,1;0rad)
  Radius = 1.6
FEATURE [Part::Cylinder] Cylinder020  label="Cylinder021"
  Angle = 360
  AttacherType = Attacher::AttachEngine3D
  Height = 10
  Placement = pos=(338,49,-1) rot=(0,0,1;0rad)
  Radius = 1.6
FEATURE [Part::Cylinder] Cylinder021  label="Cylinder022"
  Angle = 360
  AttacherType = Attacher::AttachEngine3D
  Height = 10
  Placement = pos=(338,25,-1) rot=(0,0,1;0rad)
  Radius = 1.6
FEATURE [Part::Cylinder] Cylinder019  label="Cylinder020"
  Angle = 360
  AttacherType = Attacher::AttachEngine3D
  Height = 10
  Placement = pos=(338,192,-1) rot=(0,0,1;0rad)
  Radius = 1.6
FEATURE [Part::Cut] Cut013
  Base = -> Cut012
  Tool = -> Cylinder013
FEATURE [Part::Cut] Cut014
  Base = -> Cut013
  Tool = -> Cylinder014
FEATURE [Part::Cut] Cut015
  Base = -> Cut014
  Tool = -> Cylinder015
FEATURE [Part::Cut] Cut016
  Base = -> Cut015
  Tool = -> Cylinder016
FEATURE [Part::Cut] Cut017
  Base = -> Cut016
  Tool = -> Cylinder017
FEATURE [Part::Cut] Cut018
  Base = -> Cut017
  Tool = -> Cylinder018
FEATURE [Part::Cut] Cut019
  Base = -> Cut018
  Tool = -> Cylinder019
FEATURE [Part::Cut] Cut020
  Base = -> Cut019
  Tool = -> Cylinder020
FEATURE [Part::Cut] Cut021  label="Carriage_frame"
  Base = -> Cut020
  Tool = -> Cylinder021
FEATURE [Part::Feature] Compound062001001003001001024001  label="xc_support_SK6_001"
  Placement = pos=(0,0,0) rot=(0.57735,0.57735,-0.57735;2.0944rad)
  shape: bbox 14 x 33 x 42 mm, 49 faces, 3 solids (baked)
FEATURE [Part::Feature] Compound062001001003001001024002  label="xc_support_SK6_002"
  Placement = pos=(-316,0,0) rot=(0.57735,0.57735,-0.57735;2.0944rad)
  shape: bbox 14 x 33 x 42 mm, 49 faces, 3 solids (baked)
FEATURE [Part::Cylinder] Cylinder012029001075  label="xc_support_roll_6mm"
  Angle = 360
  AttacherType = Attacher::AttachEngine3D
  Height = 330
  Placement = pos=(14,14,-9) rot=(0,-1,0;1.5708rad)
  Radius = 3
FEATURE [Part::Feature] Shape001  label="xc_support_SK8_001"
  Placement = pos=(14,0,-60) rot=(0,-1,0;1.5708rad)
  shape: bbox 14 x 33 x 42 mm, 45 faces, 2 solids (baked)
FEATURE [Part::Feature] Shape002  label="xc_support_SK8_002"
  Placement = pos=(-302,0,-60) rot=(0,-1,0;1.5708rad)
  shape: bbox 14 x 33 x 42 mm, 45 faces, 2 solids (baked)
FEATURE [Part::Cylinder] Cylinder012029001076  label="xc_support_roll_8mm"
  Angle = 360
  AttacherType = Attacher::AttachEngine3D
  Height = 330
  Placement = pos=(14,14,-51) rot=(0,-1,0;1.5708rad)
  Radius = 4
FEATURE [App::Part] Part088  label="xc_support"
  Group = -> [Compound062001001003001001024001,Compound062001001003001001024002,Cylinder012029001075,Shape001,Shape002,Cylinder012029001076]
  Origin = -> Origin108
  Placement = pos=(-7,283,417) rot=(0,0,1;0rad)
FEATURE [App::DocumentObjectGroup] Group005  label="Frame"
  Group = -> [Part011,Part088]
FEATURE [Part::Cylinder] Cylinder012029001077  label="Cylinder012029001080"
  Angle = 360
  AttacherType = Attacher::AttachEngine3D
  Height = 4
  Placement = pos=(75.63,26.63,0) rot=(0,0,1;0rad)
  Radius = 1.75
FEATURE [Part::Cylinder] Cylinder012029001080  label="Cylinder012029001083"
  Angle = 360
  AttacherType = Attacher::AttachEngine3D
  Height = 4
  Placement = pos=(284.37,26.63,0) rot=(0,0,1;0rad)
  Radius = 1.75
FEATURE [Part::Cylinder] Cylinder012029001079  label="Cylinder012029001082"
  Angle = 360
  AttacherType = Attacher::AttachEngine3D
  Height = 4
  Placement = pos=(284.37,233.64,0) rot=(0,0,1;0rad)
  Radius = 1.75
FEATURE [Part::Cylinder] Cylinder012029001078  label="Cylinder012029001081"
  Angle = 360
  AttacherType = Attacher::AttachEngine3D
  Height = 4
  Placement = pos=(75.63,233.64,0) rot=(0,0,1;0rad)
  Radius = 1.75
FEATURE [Part::MultiFuse] Fusion001019007006
  Shapes = -> [Cylinder012029001077,Cylinder012029001078,Cylinder012029001079,Cylinder012029001080]
FEATURE [Part::Cut] Cut003059
  Base = -> Cut021
  Tool = -> Fusion001019007006
FEATURE [App::Part] Part075  label="Carriage"
  Group = -> [Part074,TR08,Part031,Part080,TR009,Part081,Cut012,Cut003055,Cut006,Cylinder013,Cut014,Cut005,Cylinder012029001065,Cylinder014,Cylinder012029001072,Cylinder012029001073,Box015001052,Cut003057,Cylinder012029001074,Cylinder012029001066,Cylinder018,Cylinder016,Cut010,Cut015,Cylinder021,Cylinder019,Cut020,Cut003056,Cut011,Cut019,Cut016,Cut007,Cut008,Cut013,Cylinder017,Cylinder020,Cut018,+20 more]
  Origin = -> Origin094
  Placement = pos=(-338,13,51) rot=(0,0,1;0rad)
FEATURE [App::DocumentObjectGroup] Group006  label="Elevator"
  Group = -> [Part028,Part075]
FEATURE [App::DocumentObjectGroup] Group004  label="Mechanics"
  Group = -> [Group005,Group006,Group020,Group036]
FEATURE [Drawing::FeatureViewPart] Ortho  label="Ortho_0_0"
  Direction = (0,1,0)
  HiddenWidth = 0.15
  LineWidth = 0.35
  Rotation = 90
  ShowHiddenLines = false
  ShowSmoothLines = false
  Source = -> Cut003059
  Tolerance = 0.05
  ViewResult = <g id="Ortho_0_0"\n   transform="rotate(90,122,314.333) translate(122,314.333) scale(1,1)"\n  >\n<g   fill="none"\n   stroke="rgb(0, 0, 0)"\n   stroke-linecap="butt"\n   stroke-linejoin="miter"\n   stroke-width="0.350000"\n   transform="scale(1,-1)"\n  >\n<path id= "1" d=" M 0 -4 L 4 -4 " />\n<path id= "2" d=" M 4 -4 L 4 364 " />\n<path id= "3" d=" M 0 -4 L 0 364 " />\n<path id= "4" d=" M 0 364 L 4 364 " />\n</g>\n</g>
  Visible = false
  X = 122
  Y = 314.333
FEATURE [Drawing::FeatureViewPart] Ortho003  label="Ortho_0_1"
  Direction = (0,0,1)
  HiddenWidth = 0.15
  LineWidth = 0.35
  Rotation = 0
  ShowHiddenLines = false
  ShowSmoothLines = false
  Source = -> Cut003059
  Tolerance = 0.05
  ViewResult = <g id="Ortho_0_1"\n   transform="rotate(0,122,282.667) translate(122,282.667) scale(1,1)"\n  >\n<g   fill="none"\n   stroke="rgb(0, 0, 0)"\n   stroke-linecap="butt"\n   stroke-linejoin="miter"\n   stroke-width="0.350000"\n   transform="scale(1,-1)"\n  >\n<path id= "1" d=" M -4 0 L -4 241 " />\n<path id= "2" d=" M -4 0 L 364 0 " />\n<path id= "3" d=" M -4 241 L 364 241 " />\n<path id= "4" d=" M 364 0 L 364 241 " />\n<circle cx ="22" cy ="216" r ="1.6" /><circle cx ="22" cy ="204" r ="7.6" /><circle cx ="22" cy ="192" r ="1.6" /><circle cx ="19" cy ="120.5" r ="1.6" /><circle cx ="11" cy ="120.5" r ="5.6" /><circle cx ="349" cy ="120.5" r ="5.6" /><circle cx ="341" cy ="120.5" r ="1.6" /><circle cx ="349" cy ="128.5" r ="1.6" /><circle cx ="338" cy ="192" r ="1.6" /><circle cx ="338" cy ="204" r ="7.6" /><circle cx ="338" cy ="216" r ="1.6" /><circle cx ="349" cy ="112.5" r ="1.6" /><circle cx ="11" cy ="112.5" r ="1.6" /><circle cx ="11" cy ="128.5" r ="1.6" /><circle cx ="22" cy ="37" r ="7.6" /><circle cx ="22" cy ="49" r ="1.6" /><circle cx ="338" cy ="49" r ="1.6" /><circle cx ="338" cy ="37" r ="7.6" /><circle cx ="22" cy ="25" r ="1.6" /><circle cx ="75.63" cy ="26.63" r ="1.75" /><circle cx ="338" cy ="25" r ="1.6" /><circle cx ="284.37" cy ="26.63" r ="1.75" /><circle cx ="3" cy ="120.5" r ="1.6" /><circle cx ="75.63" cy ="233.64" r ="1.75" /><circle cx ="284.37" cy ="233.64" r ="1.75" /><circle cx ="357" cy ="120.5" r ="1.6" /></g>\n</g>
  Visible = false
  X = 122
  Y = 282.667
FEATURE [Drawing::FeaturePage] Page
  EditableTexts = AUTHOR NAME | DRAWING TITLE | FreeCAD DRAWING | A2 | X / Y | SCALE | PN | DN | DD/MM/YYYY | REV A
  Group = -> [Ortho,Ortho003]
  Template = <path>
note: 1 file-system path scrubbed to <path> (originals preserved in the JSON sidecar)
